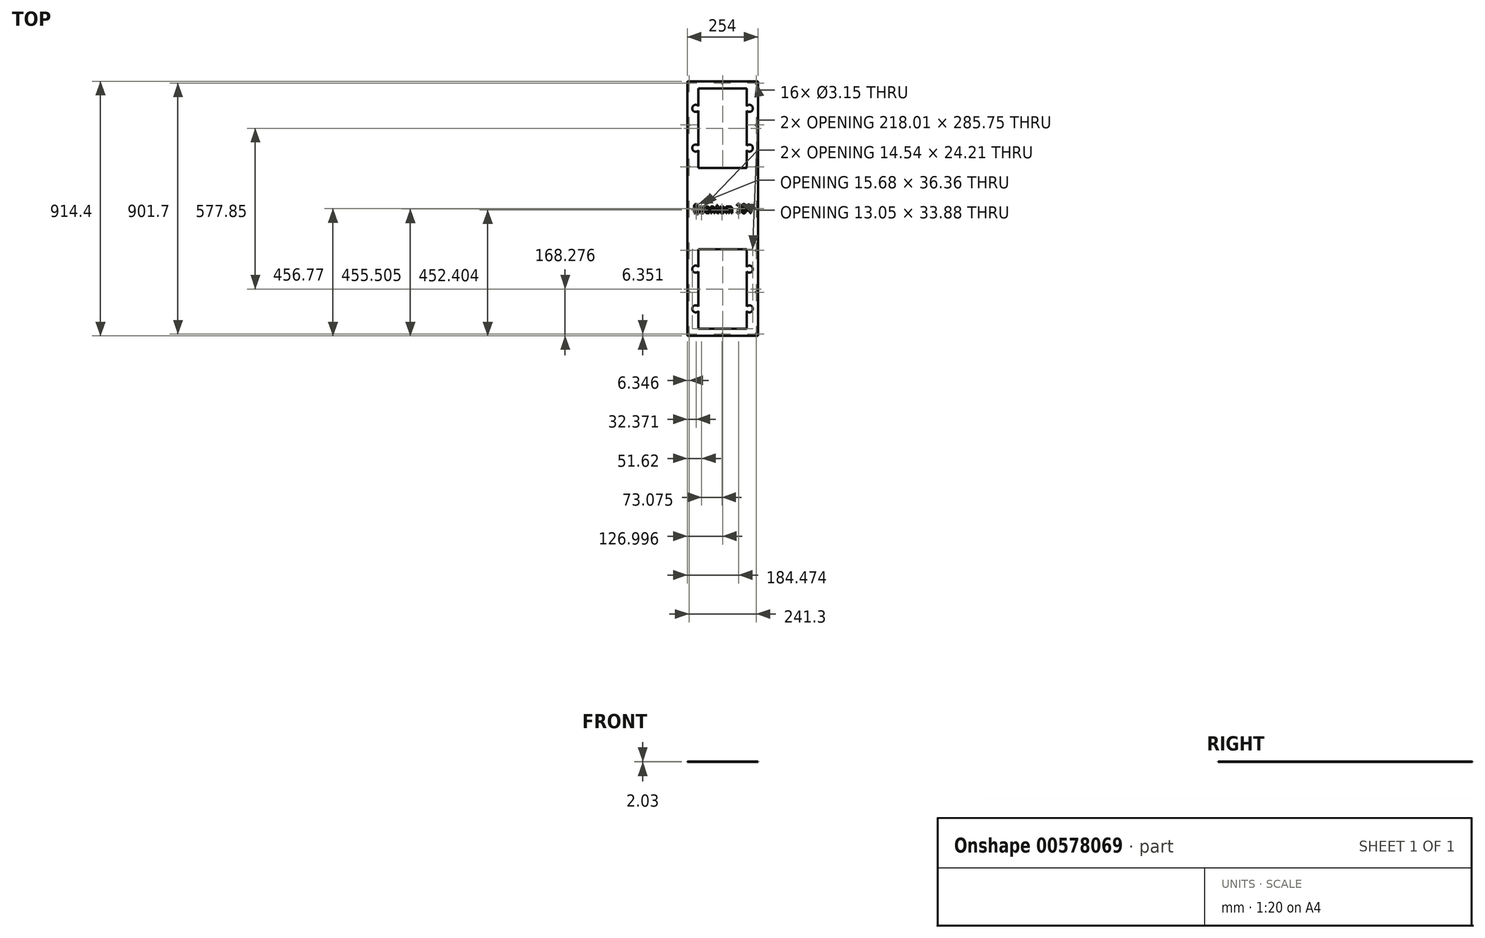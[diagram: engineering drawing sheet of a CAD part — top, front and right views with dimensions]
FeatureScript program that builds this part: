
annotation { "Feature Type Name" : "Feature", "Feature Type Description" : "" }
export const myFeature = defineFeature(function(context is Context, id is Id, definition is map)
    precondition{}
    {
        {
            var Q0;
            Q0=qCreatedBy(makeId("Top.planeOp"),FACE);
            var sketch = newSketch(context, id + "F0", { "sketchPlane" : qUnion([Q0])});
            skLineSegment(sketch, "E0.bottom", {"start": v(-485.77, 470.81) * mm, "end": v(-231.77, 470.81) * mm});
            skLineSegment(sketch, "E0.top", {"start": v(-485.77, -443.59) * mm, "end": v(-231.77, -443.59) * mm});
            skLineSegment(sketch, "E0.left", {"start": v(-485.77, 470.81) * mm, "end": v(-485.77, -443.59) * mm});
            skLineSegment(sketch, "E0.right", {"start": v(-231.77, 470.81) * mm, "end": v(-231.77, -443.59) * mm});
            skLineSegment(sketch, "E1.bottom", {"start": v(-445.55, 445.41) * mm, "end": v(-272, 445.41) * mm});
            skLineSegment(sketch, "E1.top", {"start": v(-445.55, 159.66) * mm, "end": v(-272, 159.66) * mm});
            skLineSegment(sketch, "E1.left", {"start": v(-445.55, 445.41) * mm, "end": v(-445.55, 382.37) * mm});
            skLineSegment(sketch, "E1.right", {"start": v(-272, 445.41) * mm, "end": v(-272, 382.37) * mm});
            skLineSegment(sketch, "E2.bottom", {"start": v(-445.55, -132.44) * mm, "end": v(-272, -132.44) * mm});
            skLineSegment(sketch, "E2.top", {"start": v(-445.55, -418.19) * mm, "end": v(-272, -418.19) * mm});
            skLineSegment(sketch, "E2.left", {"start": v(-445.55, -132.44) * mm, "end": v(-445.55, -195.48) * mm});
            skLineSegment(sketch, "E2.right", {"start": v(-272, -132.44) * mm, "end": v(-272, -195.48) * mm});
            skLineSegment(sketch, "E3", {"start": v(-358.77, 470.81) * mm, "end": v(-358.77, -443.59) * mm, "construction": true});
            skLineSegment(sketch, "E4.0", {"start": v(-479.42, 464.46) * mm, "end": v(-479.42, -437.24) * mm, "construction": true});
            skLineSegment(sketch, "E4.1", {"start": v(-479.42, 464.46) * mm, "end": v(-238.12, 464.46) * mm, "construction": true});
            skLineSegment(sketch, "E4.2", {"start": v(-238.12, 464.46) * mm, "end": v(-238.12, -437.24) * mm, "construction": true});
            skLineSegment(sketch, "E4.3", {"start": v(-479.42, -437.24) * mm, "end": v(-238.12, -437.24) * mm, "construction": true});
            skCircle(sketch, "E5", {"center": v(-479.42, 464.46) * mm, "radius": 1.57 * mm});
            skCircle(sketch, "E6", {"center": v(-479.42, -437.24) * mm, "radius": 1.57 * mm});
            skCircle(sketch, "E7", {"center": v(-238.12, -437.24) * mm, "radius": 1.57 * mm});
            skCircle(sketch, "E8", {"center": v(-238.12, 464.46) * mm, "radius": 1.57 * mm});
            skCircle(sketch, "E9", {"center": v(-358.77, 464.46) * mm, "radius": 1.57 * mm});
            skCircle(sketch, "E10", {"center": v(-358.77, -437.24) * mm, "radius": 1.57 * mm});
            skCircle(sketch, "E11", {"center": v(-479.42, 13.61) * mm, "radius": 1.57 * mm});
            skCircle(sketch, "E12", {"center": v(-238.12, 13.61) * mm, "radius": 1.57 * mm});
            skCircle(sketch, "E13", {"center": v(-479.42, 314.18) * mm, "radius": 1.57 * mm});
            skCircle(sketch, "E14", {"center": v(-479.42, 163.9) * mm, "radius": 1.57 * mm});
            skCircle(sketch, "E15", {"center": v(-238.12, 314.18) * mm, "radius": 1.57 * mm});
            skCircle(sketch, "E16", {"center": v(-238.12, 163.9) * mm, "radius": 1.57 * mm});
            skCircle(sketch, "E17.MirrorC", {"center": v(-479.42, -136.67) * mm, "radius": 1.57 * mm});
            skCircle(sketch, "E18.MirrorC", {"center": v(-238.12, -136.67) * mm, "radius": 1.57 * mm});
            skCircle(sketch, "E19.MirrorC", {"center": v(-238.12, -286.96) * mm, "radius": 1.57 * mm});
            skCircle(sketch, "E20.MirrorC", {"center": v(-479.42, -286.96) * mm, "radius": 1.57 * mm});
            skLineSegment(sketch, "E21.right", {"start": v(-485.77, 373.97) * mm, "end": v(-485.77, 373.97) * mm});
            skArc(sketch, "E22", {"start": v(-445.55, 382.37) * mm, "mid": v(-467.78, 373.97) * mm, "end": v(-445.55, 365.57) * mm});
            skArc(sketch, "E23", {"start": v(-272, 365.57) * mm, "mid": v(-249.77, 373.97) * mm, "end": v(-272, 382.37) * mm});
            skArc(sketch, "E24.MirrorC", {"start": v(-445.55, 222.7) * mm, "mid": v(-467.78, 231.1) * mm, "end": v(-445.55, 239.5) * mm});
            skArc(sketch, "E25.MirrorC", {"start": v(-272, 239.5) * mm, "mid": v(-249.77, 231.1) * mm, "end": v(-272, 222.7) * mm});
            skLineSegment(sketch, "E26.trimOffspring", {"start": v(-272, 365.57) * mm, "end": v(-272, 239.5) * mm});
            skLineSegment(sketch, "E27.trimOffspring", {"start": v(-445.55, 365.57) * mm, "end": v(-445.55, 239.5) * mm});
            skLineSegment(sketch, "E28.trimOffspring", {"start": v(-445.55, 222.7) * mm, "end": v(-445.55, 159.66) * mm});
            skLineSegment(sketch, "E29.trimOffspring", {"start": v(-272, 222.7) * mm, "end": v(-272, 159.66) * mm});
            skLineSegment(sketch, "E30", {"start": v(-485.77, 13.61) * mm, "end": v(-231.77, 13.61) * mm, "construction": true});
            skArc(sketch, "E31.MirrorCS", {"start": v(-445.55, -195.48) * mm, "mid": v(-467.78, -203.88) * mm, "end": v(-445.55, -212.28) * mm});
            skArc(sketch, "E32.MirrorCS", {"start": v(-445.55, -355.15) * mm, "mid": v(-467.78, -346.75) * mm, "end": v(-445.55, -338.35) * mm});
            skArc(sketch, "E33.MirrorCS", {"start": v(-272, -338.35) * mm, "mid": v(-249.77, -346.75) * mm, "end": v(-272, -355.15) * mm});
            skArc(sketch, "E34.MirrorCS", {"start": v(-272, -212.28) * mm, "mid": v(-249.77, -203.88) * mm, "end": v(-272, -195.48) * mm});
            skLineSegment(sketch, "E35.trimOffspring", {"start": v(-272, -212.28) * mm, "end": v(-272, -338.35) * mm});
            skLineSegment(sketch, "E36.trimOffspring", {"start": v(-272, -355.15) * mm, "end": v(-272, -418.19) * mm});
            skLineSegment(sketch, "E37.trimOffspring", {"start": v(-445.55, -355.15) * mm, "end": v(-445.55, -418.19) * mm});
            skLineSegment(sketch, "E38.trimOffspring", {"start": v(-445.55, -212.28) * mm, "end": v(-445.55, -338.35) * mm});
            skLineSegment(sketch, "E39", {"start": v(-461.21, 23.57) * mm, "end": v(-461.11, 24.3) * mm});
            skLineSegment(sketch, "E40", {"start": v(-461.11, 24.3) * mm, "end": v(-460.94, 24.96) * mm});
            skLineSegment(sketch, "E41", {"start": v(-460.94, 24.96) * mm, "end": v(-460.72, 25.63) * mm});
            skLineSegment(sketch, "E42", {"start": v(-460.72, 25.63) * mm, "end": v(-460.4, 26.25) * mm});
            skLineSegment(sketch, "E43", {"start": v(-460.4, 26.25) * mm, "end": v(-460.05, 26.85) * mm});
            skLineSegment(sketch, "E44", {"start": v(-460.05, 26.85) * mm, "end": v(-459.6, 27.42) * mm});
            skLineSegment(sketch, "E45", {"start": v(-459.6, 27.42) * mm, "end": v(-459.1, 27.96) * mm});
            skLineSegment(sketch, "E46", {"start": v(-459.1, 27.96) * mm, "end": v(-458.56, 28.46) * mm});
            skLineSegment(sketch, "E47", {"start": v(-458.56, 28.46) * mm, "end": v(-457.99, 28.9) * mm});
            skLineSegment(sketch, "E48", {"start": v(-457.99, 28.9) * mm, "end": v(-457.4, 29.25) * mm});
            skLineSegment(sketch, "E49", {"start": v(-457.4, 29.25) * mm, "end": v(-456.77, 29.58) * mm});
            skLineSegment(sketch, "E50", {"start": v(-456.77, 29.58) * mm, "end": v(-456.1, 29.8) * mm});
            skLineSegment(sketch, "E51", {"start": v(-456.1, 29.8) * mm, "end": v(-455.43, 29.97) * mm});
            skLineSegment(sketch, "E52", {"start": v(-455.43, 29.97) * mm, "end": v(-454.71, 30.07) * mm});
            skLineSegment(sketch, "E53", {"start": v(-454.71, 30.07) * mm, "end": v(-453.97, 30.1) * mm});
            skLineSegment(sketch, "E54", {"start": v(-453.97, 30.1) * mm, "end": v(-453.25, 30.07) * mm});
            skLineSegment(sketch, "E55", {"start": v(-453.25, 30.07) * mm, "end": v(-452.53, 29.97) * mm});
            skLineSegment(sketch, "E56", {"start": v(-452.53, 29.97) * mm, "end": v(-451.86, 29.8) * mm});
            skLineSegment(sketch, "E57", {"start": v(-451.86, 29.8) * mm, "end": v(-451.2, 29.58) * mm});
            skLineSegment(sketch, "E58", {"start": v(-451.2, 29.58) * mm, "end": v(-450.57, 29.25) * mm});
            skLineSegment(sketch, "E59", {"start": v(-450.57, 29.25) * mm, "end": v(-449.98, 28.9) * mm});
            skLineSegment(sketch, "E60", {"start": v(-449.98, 28.9) * mm, "end": v(-449.4, 28.46) * mm});
            skLineSegment(sketch, "E61", {"start": v(-449.4, 28.46) * mm, "end": v(-448.86, 27.96) * mm});
            skLineSegment(sketch, "E62", {"start": v(-448.86, 27.96) * mm, "end": v(-448.36, 27.42) * mm});
            skLineSegment(sketch, "E63", {"start": v(-448.36, 27.42) * mm, "end": v(-447.92, 26.85) * mm});
            skLineSegment(sketch, "E64", {"start": v(-447.92, 26.85) * mm, "end": v(-447.57, 26.25) * mm});
            skLineSegment(sketch, "E65", {"start": v(-447.57, 26.25) * mm, "end": v(-447.25, 25.63) * mm});
            skLineSegment(sketch, "E66", {"start": v(-447.25, 25.63) * mm, "end": v(-447.02, 24.96) * mm});
            skLineSegment(sketch, "E67", {"start": v(-447.02, 24.96) * mm, "end": v(-446.85, 24.3) * mm});
            skLineSegment(sketch, "E68", {"start": v(-446.85, 24.3) * mm, "end": v(-446.75, 23.57) * mm});
            skLineSegment(sketch, "E69", {"start": v(-446.75, 23.57) * mm, "end": v(-446.73, 22.85) * mm});
            skLineSegment(sketch, "E70", {"start": v(-446.73, 22.85) * mm, "end": v(-446.73, 3.5) * mm});
            skLineSegment(sketch, "E71", {"start": v(-446.73, 3.5) * mm, "end": v(-446.73, 3.28) * mm});
            skLineSegment(sketch, "E72", {"start": v(-446.73, 3.28) * mm, "end": v(-446.73, 3.06) * mm});
            skLineSegment(sketch, "E73", {"start": v(-446.73, 3.06) * mm, "end": v(-446.75, 2.84) * mm});
            skLineSegment(sketch, "E74", {"start": v(-446.75, 2.84) * mm, "end": v(-446.78, 2.61) * mm});
            skLineSegment(sketch, "E75", {"start": v(-446.78, 2.61) * mm, "end": v(-446.8, 2.41) * mm});
            skLineSegment(sketch, "E76", {"start": v(-446.8, 2.41) * mm, "end": v(-446.83, 2.2) * mm});
            skLineSegment(sketch, "E77", {"start": v(-446.83, 2.2) * mm, "end": v(-446.85, 2) * mm});
            skLineSegment(sketch, "E78", {"start": v(-446.85, 2) * mm, "end": v(-446.9, 1.77) * mm});
            skLineSegment(sketch, "E79", {"start": v(-446.9, 1.77) * mm, "end": v(-446.92, 1.65) * mm});
            skLineSegment(sketch, "E80", {"start": v(-446.92, 1.65) * mm, "end": v(-446.97, 1.5) * mm});
            skLineSegment(sketch, "E81", {"start": v(-446.97, 1.5) * mm, "end": v(-447.02, 1.37) * mm});
            skLineSegment(sketch, "E82", {"start": v(-447.02, 1.37) * mm, "end": v(-447.07, 1.25) * mm});
            skLineSegment(sketch, "E83", {"start": v(-447.07, 1.25) * mm, "end": v(-447.15, 1.15) * mm});
            skLineSegment(sketch, "E84", {"start": v(-447.15, 1.15) * mm, "end": v(-447.22, 1.03) * mm});
            skLineSegment(sketch, "E85", {"start": v(-447.22, 1.03) * mm, "end": v(-447.32, 0.93) * mm});
            skLineSegment(sketch, "E86", {"start": v(-447.32, 0.93) * mm, "end": v(-447.42, 0.8) * mm});
            skLineSegment(sketch, "E87", {"start": v(-447.42, 0.8) * mm, "end": v(-447.57, 0.68) * mm});
            skLineSegment(sketch, "E88", {"start": v(-447.57, 0.68) * mm, "end": v(-447.74, 0.55) * mm});
            skLineSegment(sketch, "E89", {"start": v(-447.74, 0.55) * mm, "end": v(-447.9, 0.46) * mm});
            skLineSegment(sketch, "E90", {"start": v(-447.9, 0.46) * mm, "end": v(-448.07, 0.38) * mm});
            skLineSegment(sketch, "E91", {"start": v(-448.07, 0.38) * mm, "end": v(-448.24, 0.3) * mm});
            skLineSegment(sketch, "E92", {"start": v(-448.24, 0.3) * mm, "end": v(-448.41, 0.26) * mm});
            skLineSegment(sketch, "E93", {"start": v(-448.41, 0.26) * mm, "end": v(-448.61, 0.23) * mm});
            skLineSegment(sketch, "E94", {"start": v(-448.61, 0.23) * mm, "end": v(-448.8, 0.23) * mm});
            skLineSegment(sketch, "E95", {"start": v(-448.8, 0.23) * mm, "end": v(-449, 0.23) * mm});
            skLineSegment(sketch, "E96", {"start": v(-449, 0.23) * mm, "end": v(-449.18, 0.26) * mm});
            skLineSegment(sketch, "E97", {"start": v(-449.18, 0.26) * mm, "end": v(-449.38, 0.3) * mm});
            skLineSegment(sketch, "E98", {"start": v(-449.38, 0.3) * mm, "end": v(-449.55, 0.38) * mm});
            skLineSegment(sketch, "E99", {"start": v(-449.55, 0.38) * mm, "end": v(-449.7, 0.46) * mm});
            skLineSegment(sketch, "E100", {"start": v(-449.7, 0.46) * mm, "end": v(-449.88, 0.55) * mm});
            skLineSegment(sketch, "E101", {"start": v(-449.88, 0.55) * mm, "end": v(-450.03, 0.65) * mm});
            skLineSegment(sketch, "E102", {"start": v(-450.03, 0.65) * mm, "end": v(-450.17, 0.8) * mm});
            skLineSegment(sketch, "E103", {"start": v(-450.17, 0.8) * mm, "end": v(-450.3, 0.95) * mm});
            skLineSegment(sketch, "E104", {"start": v(-450.3, 0.95) * mm, "end": v(-450.42, 1.1) * mm});
            skLineSegment(sketch, "E105", {"start": v(-450.42, 1.1) * mm, "end": v(-450.52, 1.25) * mm});
            skLineSegment(sketch, "E106", {"start": v(-450.52, 1.25) * mm, "end": v(-450.6, 1.42) * mm});
            skLineSegment(sketch, "E107", {"start": v(-450.6, 1.42) * mm, "end": v(-450.67, 1.6) * mm});
            skLineSegment(sketch, "E108", {"start": v(-450.67, 1.6) * mm, "end": v(-450.7, 1.77) * mm});
            skLineSegment(sketch, "E109", {"start": v(-450.7, 1.77) * mm, "end": v(-450.72, 1.97) * mm});
            skLineSegment(sketch, "E110", {"start": v(-450.72, 1.97) * mm, "end": v(-450.74, 2.17) * mm});
            skLineSegment(sketch, "E111", {"start": v(-450.74, 2.17) * mm, "end": v(-450.74, 2.22) * mm});
            skLineSegment(sketch, "E112", {"start": v(-450.74, 2.22) * mm, "end": v(-450.74, 2.27) * mm});
            skLineSegment(sketch, "E113", {"start": v(-450.74, 2.27) * mm, "end": v(-450.74, 2.32) * mm});
            skLineSegment(sketch, "E114", {"start": v(-450.74, 2.32) * mm, "end": v(-450.74, 2.36) * mm});
            skLineSegment(sketch, "E115", {"start": v(-450.74, 2.36) * mm, "end": v(-450.72, 2.41) * mm});
            skLineSegment(sketch, "E116", {"start": v(-450.72, 2.41) * mm, "end": v(-450.72, 2.49) * mm});
            skLineSegment(sketch, "E117", {"start": v(-450.72, 2.49) * mm, "end": v(-450.72, 2.54) * mm});
            skLineSegment(sketch, "E118", {"start": v(-450.72, 2.54) * mm, "end": v(-450.72, 2.59) * mm});
            skLineSegment(sketch, "E119", {"start": v(-450.72, 2.59) * mm, "end": v(-450.7, 2.71) * mm});
            skLineSegment(sketch, "E120", {"start": v(-450.7, 2.71) * mm, "end": v(-450.67, 2.81) * mm});
            skLineSegment(sketch, "E121", {"start": v(-450.67, 2.81) * mm, "end": v(-450.65, 2.94) * mm});
            skLineSegment(sketch, "E122", {"start": v(-450.65, 2.94) * mm, "end": v(-450.62, 3.03) * mm});
            skLineSegment(sketch, "E123", {"start": v(-450.62, 3.03) * mm, "end": v(-450.62, 3.16) * mm});
            skLineSegment(sketch, "E124", {"start": v(-450.62, 3.16) * mm, "end": v(-450.6, 3.26) * mm});
            skLineSegment(sketch, "E125", {"start": v(-450.6, 3.26) * mm, "end": v(-450.6, 3.38) * mm});
            skLineSegment(sketch, "E126", {"start": v(-450.6, 3.38) * mm, "end": v(-450.6, 3.5) * mm});
            skLineSegment(sketch, "E127", {"start": v(-450.6, 3.5) * mm, "end": v(-450.6, 22.85) * mm});
            skLineSegment(sketch, "E128", {"start": v(-450.6, 22.85) * mm, "end": v(-450.62, 23.18) * mm});
            skLineSegment(sketch, "E129", {"start": v(-450.62, 23.18) * mm, "end": v(-450.65, 23.52) * mm});
            skLineSegment(sketch, "E130", {"start": v(-450.65, 23.52) * mm, "end": v(-450.74, 23.85) * mm});
            skLineSegment(sketch, "E131", {"start": v(-450.74, 23.85) * mm, "end": v(-450.84, 24.14) * mm});
            skLineSegment(sketch, "E132", {"start": v(-450.84, 24.14) * mm, "end": v(-451, 24.44) * mm});
            skLineSegment(sketch, "E133", {"start": v(-451, 24.44) * mm, "end": v(-451.14, 24.71) * mm});
            skLineSegment(sketch, "E134", {"start": v(-451.14, 24.71) * mm, "end": v(-451.36, 24.99) * mm});
            skLineSegment(sketch, "E135", {"start": v(-451.36, 24.99) * mm, "end": v(-451.59, 25.23) * mm});
            skLineSegment(sketch, "E136", {"start": v(-451.59, 25.23) * mm, "end": v(-451.84, 25.46) * mm});
            skLineSegment(sketch, "E137", {"start": v(-451.84, 25.46) * mm, "end": v(-452.1, 25.68) * mm});
            skLineSegment(sketch, "E138", {"start": v(-452.1, 25.68) * mm, "end": v(-452.38, 25.83) * mm});
            skLineSegment(sketch, "E139", {"start": v(-452.38, 25.83) * mm, "end": v(-452.68, 25.98) * mm});
            skLineSegment(sketch, "E140", {"start": v(-452.68, 25.98) * mm, "end": v(-452.98, 26.08) * mm});
            skLineSegment(sketch, "E141", {"start": v(-452.98, 26.08) * mm, "end": v(-453.3, 26.18) * mm});
            skLineSegment(sketch, "E142", {"start": v(-453.3, 26.18) * mm, "end": v(-453.65, 26.2) * mm});
            skLineSegment(sketch, "E143", {"start": v(-453.65, 26.2) * mm, "end": v(-453.97, 26.23) * mm});
            skLineSegment(sketch, "E144", {"start": v(-453.97, 26.23) * mm, "end": v(-454.32, 26.2) * mm});
            skLineSegment(sketch, "E145", {"start": v(-454.32, 26.2) * mm, "end": v(-454.66, 26.18) * mm});
            skLineSegment(sketch, "E146", {"start": v(-454.66, 26.18) * mm, "end": v(-454.99, 26.08) * mm});
            skLineSegment(sketch, "E147", {"start": v(-454.99, 26.08) * mm, "end": v(-455.28, 25.98) * mm});
            skLineSegment(sketch, "E148", {"start": v(-455.28, 25.98) * mm, "end": v(-455.58, 25.83) * mm});
            skLineSegment(sketch, "E149", {"start": v(-455.58, 25.83) * mm, "end": v(-455.85, 25.68) * mm});
            skLineSegment(sketch, "E150", {"start": v(-455.85, 25.68) * mm, "end": v(-456.13, 25.46) * mm});
            skLineSegment(sketch, "E151", {"start": v(-456.13, 25.46) * mm, "end": v(-456.38, 25.23) * mm});
            skLineSegment(sketch, "E152", {"start": v(-456.38, 25.23) * mm, "end": v(-456.6, 24.99) * mm});
            skLineSegment(sketch, "E153", {"start": v(-456.6, 24.99) * mm, "end": v(-456.82, 24.71) * mm});
            skLineSegment(sketch, "E154", {"start": v(-456.82, 24.71) * mm, "end": v(-456.97, 24.44) * mm});
            skLineSegment(sketch, "E155", {"start": v(-456.97, 24.44) * mm, "end": v(-457.12, 24.14) * mm});
            skLineSegment(sketch, "E156", {"start": v(-457.12, 24.14) * mm, "end": v(-457.22, 23.85) * mm});
            skLineSegment(sketch, "E157", {"start": v(-457.22, 23.85) * mm, "end": v(-457.32, 23.52) * mm});
            skLineSegment(sketch, "E158", {"start": v(-457.32, 23.52) * mm, "end": v(-457.34, 23.18) * mm});
            skLineSegment(sketch, "E159", {"start": v(-457.34, 23.18) * mm, "end": v(-457.37, 22.85) * mm});
            skLineSegment(sketch, "E160", {"start": v(-457.37, 22.85) * mm, "end": v(-457.37, 3.5) * mm});
            skLineSegment(sketch, "E161", {"start": v(-457.37, 3.5) * mm, "end": v(-457.34, 3.16) * mm});
            skLineSegment(sketch, "E162", {"start": v(-457.34, 3.16) * mm, "end": v(-457.32, 2.84) * mm});
            skLineSegment(sketch, "E163", {"start": v(-457.32, 2.84) * mm, "end": v(-457.24, 2.54) * mm});
            skLineSegment(sketch, "E164", {"start": v(-457.24, 2.54) * mm, "end": v(-457.14, 2.24) * mm});
            skLineSegment(sketch, "E165", {"start": v(-457.14, 2.24) * mm, "end": v(-457, 1.97) * mm});
            skLineSegment(sketch, "E166", {"start": v(-457, 1.97) * mm, "end": v(-456.85, 1.72) * mm});
            skLineSegment(sketch, "E167", {"start": v(-456.85, 1.72) * mm, "end": v(-456.65, 1.47) * mm});
            skLineSegment(sketch, "E168", {"start": v(-456.65, 1.47) * mm, "end": v(-456.43, 1.25) * mm});
            skLineSegment(sketch, "E169", {"start": v(-456.43, 1.25) * mm, "end": v(-456.2, 1.05) * mm});
            skLineSegment(sketch, "E170", {"start": v(-456.2, 1.05) * mm, "end": v(-455.95, 0.85) * mm});
            skLineSegment(sketch, "E171", {"start": v(-455.95, 0.85) * mm, "end": v(-455.7, 0.68) * mm});
            skLineSegment(sketch, "E172", {"start": v(-455.7, 0.68) * mm, "end": v(-455.43, 0.53) * mm});
            skLineSegment(sketch, "E173", {"start": v(-455.43, 0.53) * mm, "end": v(-455.18, 0.4) * mm});
            skLineSegment(sketch, "E174", {"start": v(-455.18, 0.4) * mm, "end": v(-454.89, 0.28) * mm});
            skLineSegment(sketch, "E175", {"start": v(-454.89, 0.28) * mm, "end": v(-454.61, 0.18) * mm});
            skLineSegment(sketch, "E176", {"start": v(-454.61, 0.18) * mm, "end": v(-454.32, 0.08) * mm});
            skLineSegment(sketch, "E177", {"start": v(-454.32, 0.08) * mm, "end": v(-446.9, -2.5) * mm});
            skLineSegment(sketch, "E178", {"start": v(-446.9, -2.5) * mm, "end": v(-446.7, -2.57) * mm});
            skLineSegment(sketch, "E179", {"start": v(-446.7, -2.57) * mm, "end": v(-446.53, -2.67) * mm});
            skLineSegment(sketch, "E180", {"start": v(-446.53, -2.67) * mm, "end": v(-446.38, -2.77) * mm});
            skLineSegment(sketch, "E181", {"start": v(-446.38, -2.77) * mm, "end": v(-446.23, -2.9) * mm});
            skLineSegment(sketch, "E182", {"start": v(-446.23, -2.9) * mm, "end": v(-446.08, -3.02) * mm});
            skLineSegment(sketch, "E183", {"start": v(-446.08, -3.02) * mm, "end": v(-445.96, -3.17) * mm});
            skLineSegment(sketch, "E184", {"start": v(-445.96, -3.17) * mm, "end": v(-445.86, -3.32) * mm});
            skLineSegment(sketch, "E185", {"start": v(-445.86, -3.32) * mm, "end": v(-445.76, -3.49) * mm});
            skLineSegment(sketch, "E186", {"start": v(-445.76, -3.49) * mm, "end": v(-445.7, -3.61) * mm});
            skLineSegment(sketch, "E187", {"start": v(-445.7, -3.61) * mm, "end": v(-445.68, -3.71) * mm});
            skLineSegment(sketch, "E188", {"start": v(-445.68, -3.71) * mm, "end": v(-445.63, -3.81) * mm});
            skLineSegment(sketch, "E189", {"start": v(-445.63, -3.81) * mm, "end": v(-445.61, -3.94) * mm});
            skLineSegment(sketch, "E190", {"start": v(-445.61, -3.94) * mm, "end": v(-445.59, -4.03) * mm});
            skLineSegment(sketch, "E191", {"start": v(-445.59, -4.03) * mm, "end": v(-445.59, -4.13) * mm});
            skLineSegment(sketch, "E192", {"start": v(-445.59, -4.13) * mm, "end": v(-445.56, -4.23) * mm});
            skLineSegment(sketch, "E193", {"start": v(-445.56, -4.23) * mm, "end": v(-445.56, -4.33) * mm});
            skLineSegment(sketch, "E194", {"start": v(-445.56, -4.33) * mm, "end": v(-445.56, -4.4) * mm});
            skLineSegment(sketch, "E195", {"start": v(-445.56, -4.4) * mm, "end": v(-445.56, -4.48) * mm});
            skLineSegment(sketch, "E196", {"start": v(-445.56, -4.48) * mm, "end": v(-445.59, -4.56) * mm});
            skLineSegment(sketch, "E197", {"start": v(-445.59, -4.56) * mm, "end": v(-445.59, -4.63) * mm});
            skLineSegment(sketch, "E198", {"start": v(-445.59, -4.63) * mm, "end": v(-445.61, -4.7) * mm});
            skLineSegment(sketch, "E199", {"start": v(-445.61, -4.7) * mm, "end": v(-445.61, -4.78) * mm});
            skLineSegment(sketch, "E200", {"start": v(-445.61, -4.78) * mm, "end": v(-445.63, -4.88) * mm});
            skLineSegment(sketch, "E201", {"start": v(-445.63, -4.88) * mm, "end": v(-445.66, -4.95) * mm});
            skLineSegment(sketch, "E202", {"start": v(-445.66, -4.95) * mm, "end": v(-445.73, -5.13) * mm});
            skLineSegment(sketch, "E203", {"start": v(-445.73, -5.13) * mm, "end": v(-445.83, -5.3) * mm});
            skLineSegment(sketch, "E204", {"start": v(-445.83, -5.3) * mm, "end": v(-445.93, -5.47) * mm});
            skLineSegment(sketch, "E205", {"start": v(-445.93, -5.47) * mm, "end": v(-446.03, -5.62) * mm});
            skLineSegment(sketch, "E206", {"start": v(-446.03, -5.62) * mm, "end": v(-446.18, -5.75) * mm});
            skLineSegment(sketch, "E207", {"start": v(-446.18, -5.75) * mm, "end": v(-446.33, -5.87) * mm});
            skLineSegment(sketch, "E208", {"start": v(-446.33, -5.87) * mm, "end": v(-446.48, -6) * mm});
            skLineSegment(sketch, "E209", {"start": v(-446.48, -6) * mm, "end": v(-446.65, -6.1) * mm});
            skLineSegment(sketch, "E210", {"start": v(-446.65, -6.1) * mm, "end": v(-446.75, -6.12) * mm});
            skLineSegment(sketch, "E211", {"start": v(-446.75, -6.12) * mm, "end": v(-446.88, -6.17) * mm});
            skLineSegment(sketch, "E212", {"start": v(-446.88, -6.17) * mm, "end": v(-446.97, -6.2) * mm});
            skLineSegment(sketch, "E213", {"start": v(-446.97, -6.2) * mm, "end": v(-447.07, -6.22) * mm});
            skLineSegment(sketch, "E214", {"start": v(-447.07, -6.22) * mm, "end": v(-447.2, -6.24) * mm});
            skLineSegment(sketch, "E215", {"start": v(-447.2, -6.24) * mm, "end": v(-447.3, -6.27) * mm});
            skLineSegment(sketch, "E216", {"start": v(-447.3, -6.27) * mm, "end": v(-447.4, -6.27) * mm});
            skLineSegment(sketch, "E217", {"start": v(-447.4, -6.27) * mm, "end": v(-447.5, -6.27) * mm});
            skLineSegment(sketch, "E218", {"start": v(-447.5, -6.27) * mm, "end": v(-447.57, -6.27) * mm});
            skLineSegment(sketch, "E219", {"start": v(-447.57, -6.27) * mm, "end": v(-447.67, -6.27) * mm});
            skLineSegment(sketch, "E220", {"start": v(-447.67, -6.27) * mm, "end": v(-447.74, -6.27) * mm});
            skLineSegment(sketch, "E221", {"start": v(-447.74, -6.27) * mm, "end": v(-447.82, -6.24) * mm});
            skLineSegment(sketch, "E222", {"start": v(-447.82, -6.24) * mm, "end": v(-447.9, -6.24) * mm});
            skLineSegment(sketch, "E223", {"start": v(-447.9, -6.24) * mm, "end": v(-447.97, -6.22) * mm});
            skLineSegment(sketch, "E224", {"start": v(-447.97, -6.22) * mm, "end": v(-448.04, -6.2) * mm});
            skLineSegment(sketch, "E225", {"start": v(-448.04, -6.2) * mm, "end": v(-448.14, -6.17) * mm});
            skLineSegment(sketch, "E226", {"start": v(-448.14, -6.17) * mm, "end": v(-455.9, -3.51) * mm});
            skLineSegment(sketch, "E227", {"start": v(-455.9, -3.51) * mm, "end": v(-456.4, -3.34) * mm});
            skLineSegment(sketch, "E228", {"start": v(-456.4, -3.34) * mm, "end": v(-456.85, -3.14) * mm});
            skLineSegment(sketch, "E229", {"start": v(-456.85, -3.14) * mm, "end": v(-457.3, -2.92) * mm});
            skLineSegment(sketch, "E230", {"start": v(-457.3, -2.92) * mm, "end": v(-457.7, -2.7) * mm});
            skLineSegment(sketch, "E231", {"start": v(-457.7, -2.7) * mm, "end": v(-458.09, -2.45) * mm});
            skLineSegment(sketch, "E232", {"start": v(-458.09, -2.45) * mm, "end": v(-458.46, -2.2) * mm});
            skLineSegment(sketch, "E233", {"start": v(-458.46, -2.2) * mm, "end": v(-458.78, -1.93) * mm});
            skLineSegment(sketch, "E234", {"start": v(-458.78, -1.93) * mm, "end": v(-459.1, -1.63) * mm});
            skLineSegment(sketch, "E235", {"start": v(-459.1, -1.63) * mm, "end": v(-459.6, -1.08) * mm});
            skLineSegment(sketch, "E236", {"start": v(-459.6, -1.08) * mm, "end": v(-460.05, -0.51) * mm});
            skLineSegment(sketch, "E237", {"start": v(-460.05, -0.51) * mm, "end": v(-460.4, 0.08) * mm});
            skLineSegment(sketch, "E238", {"start": v(-460.4, 0.08) * mm, "end": v(-460.72, 0.7) * mm});
            skLineSegment(sketch, "E239", {"start": v(-460.72, 0.7) * mm, "end": v(-460.94, 1.37) * mm});
            skLineSegment(sketch, "E240", {"start": v(-460.94, 1.37) * mm, "end": v(-461.11, 2.04) * mm});
            skLineSegment(sketch, "E241", {"start": v(-461.11, 2.04) * mm, "end": v(-461.21, 2.76) * mm});
            skLineSegment(sketch, "E242", {"start": v(-461.21, 2.76) * mm, "end": v(-461.24, 3.5) * mm});
            skLineSegment(sketch, "E243", {"start": v(-461.24, 3.5) * mm, "end": v(-461.24, 22.85) * mm});
            skLineSegment(sketch, "E244", {"start": v(-461.24, 22.85) * mm, "end": v(-461.21, 23.57) * mm});
            skLineSegment(sketch, "E245", {"start": v(-441.37, 3.23) * mm, "end": v(-441.42, 3.98) * mm});
            skLineSegment(sketch, "E246", {"start": v(-441.42, 3.98) * mm, "end": v(-441.42, 18.98) * mm});
            skLineSegment(sketch, "E247", {"start": v(-441.42, 18.98) * mm, "end": v(-441.4, 19.16) * mm});
            skLineSegment(sketch, "E248", {"start": v(-441.4, 19.16) * mm, "end": v(-441.37, 19.36) * mm});
            skLineSegment(sketch, "E249", {"start": v(-441.37, 19.36) * mm, "end": v(-441.32, 19.53) * mm});
            skLineSegment(sketch, "E250", {"start": v(-441.32, 19.53) * mm, "end": v(-441.27, 19.7) * mm});
            skLineSegment(sketch, "E251", {"start": v(-441.27, 19.7) * mm, "end": v(-441.2, 19.88) * mm});
            skLineSegment(sketch, "E252", {"start": v(-441.2, 19.88) * mm, "end": v(-441.1, 20.05) * mm});
            skLineSegment(sketch, "E253", {"start": v(-441.1, 20.05) * mm, "end": v(-440.97, 20.2) * mm});
            skLineSegment(sketch, "E254", {"start": v(-440.97, 20.2) * mm, "end": v(-440.85, 20.35) * mm});
            skLineSegment(sketch, "E255", {"start": v(-440.85, 20.35) * mm, "end": v(-440.7, 20.47) * mm});
            skLineSegment(sketch, "E256", {"start": v(-440.7, 20.47) * mm, "end": v(-440.55, 20.6) * mm});
            skLineSegment(sketch, "E257", {"start": v(-440.55, 20.6) * mm, "end": v(-440.38, 20.7) * mm});
            skLineSegment(sketch, "E258", {"start": v(-440.38, 20.7) * mm, "end": v(-440.2, 20.77) * mm});
            skLineSegment(sketch, "E259", {"start": v(-440.2, 20.77) * mm, "end": v(-440.03, 20.82) * mm});
            skLineSegment(sketch, "E260", {"start": v(-440.03, 20.82) * mm, "end": v(-439.86, 20.87) * mm});
            skLineSegment(sketch, "E261", {"start": v(-439.86, 20.87) * mm, "end": v(-439.66, 20.9) * mm});
            skLineSegment(sketch, "E262", {"start": v(-439.66, 20.9) * mm, "end": v(-439.48, 20.92) * mm});
            skLineSegment(sketch, "E263", {"start": v(-439.48, 20.92) * mm, "end": v(-439.28, 20.9) * mm});
            skLineSegment(sketch, "E264", {"start": v(-439.28, 20.9) * mm, "end": v(-439.09, 20.87) * mm});
            skLineSegment(sketch, "E265", {"start": v(-439.09, 20.87) * mm, "end": v(-438.91, 20.82) * mm});
            skLineSegment(sketch, "E266", {"start": v(-438.91, 20.82) * mm, "end": v(-438.74, 20.77) * mm});
            skLineSegment(sketch, "E267", {"start": v(-438.74, 20.77) * mm, "end": v(-438.57, 20.7) * mm});
            skLineSegment(sketch, "E268", {"start": v(-438.57, 20.7) * mm, "end": v(-438.4, 20.6) * mm});
            skLineSegment(sketch, "E269", {"start": v(-438.4, 20.6) * mm, "end": v(-438.24, 20.47) * mm});
            skLineSegment(sketch, "E270", {"start": v(-438.24, 20.47) * mm, "end": v(-438.1, 20.35) * mm});
            skLineSegment(sketch, "E271", {"start": v(-438.1, 20.35) * mm, "end": v(-437.97, 20.2) * mm});
            skLineSegment(sketch, "E272", {"start": v(-437.97, 20.2) * mm, "end": v(-437.85, 20.05) * mm});
            skLineSegment(sketch, "E273", {"start": v(-437.85, 20.05) * mm, "end": v(-437.75, 19.88) * mm});
            skLineSegment(sketch, "E274", {"start": v(-437.75, 19.88) * mm, "end": v(-437.67, 19.7) * mm});
            skLineSegment(sketch, "E275", {"start": v(-437.67, 19.7) * mm, "end": v(-437.62, 19.53) * mm});
            skLineSegment(sketch, "E276", {"start": v(-437.62, 19.53) * mm, "end": v(-437.57, 19.36) * mm});
            skLineSegment(sketch, "E277", {"start": v(-437.57, 19.36) * mm, "end": v(-437.55, 19.16) * mm});
            skLineSegment(sketch, "E278", {"start": v(-437.55, 19.16) * mm, "end": v(-437.55, 18.98) * mm});
            skLineSegment(sketch, "E279", {"start": v(-437.55, 18.98) * mm, "end": v(-437.55, 3.98) * mm});
            skLineSegment(sketch, "E280", {"start": v(-437.55, 3.98) * mm, "end": v(-437.52, 3.63) * mm});
            skLineSegment(sketch, "E281", {"start": v(-437.52, 3.63) * mm, "end": v(-437.47, 3.3) * mm});
            skLineSegment(sketch, "E282", {"start": v(-437.47, 3.3) * mm, "end": v(-437.4, 2.99) * mm});
            skLineSegment(sketch, "E283", {"start": v(-437.4, 2.99) * mm, "end": v(-437.3, 2.69) * mm});
            skLineSegment(sketch, "E284", {"start": v(-437.3, 2.69) * mm, "end": v(-437.15, 2.39) * mm});
            skLineSegment(sketch, "E285", {"start": v(-437.15, 2.39) * mm, "end": v(-436.98, 2.12) * mm});
            skLineSegment(sketch, "E286", {"start": v(-436.98, 2.12) * mm, "end": v(-436.78, 1.84) * mm});
            skLineSegment(sketch, "E287", {"start": v(-436.78, 1.84) * mm, "end": v(-436.56, 1.57) * mm});
            skLineSegment(sketch, "E288", {"start": v(-436.56, 1.57) * mm, "end": v(-436.28, 1.35) * mm});
            skLineSegment(sketch, "E289", {"start": v(-436.28, 1.35) * mm, "end": v(-436.01, 1.15) * mm});
            skLineSegment(sketch, "E290", {"start": v(-436.01, 1.15) * mm, "end": v(-435.74, 0.98) * mm});
            skLineSegment(sketch, "E291", {"start": v(-435.74, 0.98) * mm, "end": v(-435.44, 0.83) * mm});
            skLineSegment(sketch, "E292", {"start": v(-435.44, 0.83) * mm, "end": v(-435.14, 0.73) * mm});
            skLineSegment(sketch, "E293", {"start": v(-435.14, 0.73) * mm, "end": v(-434.82, 0.65) * mm});
            skLineSegment(sketch, "E294", {"start": v(-434.82, 0.65) * mm, "end": v(-434.5, 0.6) * mm});
            skLineSegment(sketch, "E295", {"start": v(-434.5, 0.6) * mm, "end": v(-434.15, 0.58) * mm});
            skLineSegment(sketch, "E296", {"start": v(-434.15, 0.58) * mm, "end": v(-430.75, 0.58) * mm});
            skLineSegment(sketch, "E297", {"start": v(-430.75, 0.58) * mm, "end": v(-430.75, 18.98) * mm});
            skLineSegment(sketch, "E298", {"start": v(-430.75, 18.98) * mm, "end": v(-430.75, 19.16) * mm});
            skLineSegment(sketch, "E299", {"start": v(-430.75, 19.16) * mm, "end": v(-430.73, 19.36) * mm});
            skLineSegment(sketch, "E300", {"start": v(-430.73, 19.36) * mm, "end": v(-430.68, 19.53) * mm});
            skLineSegment(sketch, "E301", {"start": v(-430.68, 19.53) * mm, "end": v(-430.63, 19.7) * mm});
            skLineSegment(sketch, "E302", {"start": v(-430.63, 19.7) * mm, "end": v(-430.55, 19.88) * mm});
            skLineSegment(sketch, "E303", {"start": v(-430.55, 19.88) * mm, "end": v(-430.45, 20.05) * mm});
            skLineSegment(sketch, "E304", {"start": v(-430.45, 20.05) * mm, "end": v(-430.33, 20.2) * mm});
            skLineSegment(sketch, "E305", {"start": v(-430.33, 20.2) * mm, "end": v(-430.2, 20.35) * mm});
            skLineSegment(sketch, "E306", {"start": v(-430.2, 20.35) * mm, "end": v(-430.06, 20.47) * mm});
            skLineSegment(sketch, "E307", {"start": v(-430.06, 20.47) * mm, "end": v(-429.9, 20.6) * mm});
            skLineSegment(sketch, "E308", {"start": v(-429.9, 20.6) * mm, "end": v(-429.74, 20.7) * mm});
            skLineSegment(sketch, "E309", {"start": v(-429.74, 20.7) * mm, "end": v(-429.56, 20.77) * mm});
            skLineSegment(sketch, "E310", {"start": v(-429.56, 20.77) * mm, "end": v(-429.39, 20.82) * mm});
            skLineSegment(sketch, "E311", {"start": v(-429.39, 20.82) * mm, "end": v(-429.21, 20.87) * mm});
            skLineSegment(sketch, "E312", {"start": v(-429.21, 20.87) * mm, "end": v(-429.02, 20.9) * mm});
            skLineSegment(sketch, "E313", {"start": v(-429.02, 20.9) * mm, "end": v(-428.82, 20.92) * mm});
            skLineSegment(sketch, "E314", {"start": v(-428.82, 20.92) * mm, "end": v(-428.64, 20.9) * mm});
            skLineSegment(sketch, "E315", {"start": v(-428.64, 20.9) * mm, "end": v(-428.45, 20.87) * mm});
            skLineSegment(sketch, "E316", {"start": v(-428.45, 20.87) * mm, "end": v(-428.27, 20.82) * mm});
            skLineSegment(sketch, "E317", {"start": v(-428.27, 20.82) * mm, "end": v(-428.1, 20.77) * mm});
            skLineSegment(sketch, "E318", {"start": v(-428.1, 20.77) * mm, "end": v(-427.92, 20.7) * mm});
            skLineSegment(sketch, "E319", {"start": v(-427.92, 20.7) * mm, "end": v(-427.75, 20.6) * mm});
            skLineSegment(sketch, "E320", {"start": v(-427.75, 20.6) * mm, "end": v(-427.6, 20.47) * mm});
            skLineSegment(sketch, "E321", {"start": v(-427.6, 20.47) * mm, "end": v(-427.45, 20.35) * mm});
            skLineSegment(sketch, "E322", {"start": v(-427.45, 20.35) * mm, "end": v(-427.33, 20.2) * mm});
            skLineSegment(sketch, "E323", {"start": v(-427.33, 20.2) * mm, "end": v(-427.2, 20.05) * mm});
            skLineSegment(sketch, "E324", {"start": v(-427.2, 20.05) * mm, "end": v(-427.1, 19.88) * mm});
            skLineSegment(sketch, "E325", {"start": v(-427.1, 19.88) * mm, "end": v(-427.03, 19.7) * mm});
            skLineSegment(sketch, "E326", {"start": v(-427.03, 19.7) * mm, "end": v(-426.98, 19.53) * mm});
            skLineSegment(sketch, "E327", {"start": v(-426.98, 19.53) * mm, "end": v(-426.93, 19.36) * mm});
            skLineSegment(sketch, "E328", {"start": v(-426.93, 19.36) * mm, "end": v(-426.9, 19.16) * mm});
            skLineSegment(sketch, "E329", {"start": v(-426.9, 19.16) * mm, "end": v(-426.88, 18.98) * mm});
            skLineSegment(sketch, "E330", {"start": v(-426.88, 18.98) * mm, "end": v(-426.88, -1.36) * mm});
            skLineSegment(sketch, "E331", {"start": v(-426.88, -1.36) * mm, "end": v(-426.9, -1.53) * mm});
            skLineSegment(sketch, "E332", {"start": v(-426.9, -1.53) * mm, "end": v(-426.93, -1.73) * mm});
            skLineSegment(sketch, "E333", {"start": v(-426.93, -1.73) * mm, "end": v(-426.98, -1.9) * mm});
            skLineSegment(sketch, "E334", {"start": v(-426.98, -1.9) * mm, "end": v(-427.03, -2.08) * mm});
            skLineSegment(sketch, "E335", {"start": v(-427.03, -2.08) * mm, "end": v(-427.1, -2.25) * mm});
            skLineSegment(sketch, "E336", {"start": v(-427.1, -2.25) * mm, "end": v(-427.2, -2.42) * mm});
            skLineSegment(sketch, "E337", {"start": v(-427.2, -2.42) * mm, "end": v(-427.33, -2.57) * mm});
            skLineSegment(sketch, "E338", {"start": v(-427.33, -2.57) * mm, "end": v(-427.45, -2.72) * mm});
            skLineSegment(sketch, "E339", {"start": v(-427.45, -2.72) * mm, "end": v(-427.6, -2.84) * mm});
            skLineSegment(sketch, "E340", {"start": v(-427.6, -2.84) * mm, "end": v(-427.75, -2.97) * mm});
            skLineSegment(sketch, "E341", {"start": v(-427.75, -2.97) * mm, "end": v(-427.92, -3.07) * mm});
            skLineSegment(sketch, "E342", {"start": v(-427.92, -3.07) * mm, "end": v(-428.1, -3.14) * mm});
            skLineSegment(sketch, "E343", {"start": v(-428.1, -3.14) * mm, "end": v(-428.27, -3.2) * mm});
            skLineSegment(sketch, "E344", {"start": v(-428.27, -3.2) * mm, "end": v(-428.45, -3.24) * mm});
            skLineSegment(sketch, "E345", {"start": v(-428.45, -3.24) * mm, "end": v(-428.64, -3.27) * mm});
            skLineSegment(sketch, "E346", {"start": v(-428.64, -3.27) * mm, "end": v(-428.82, -3.3) * mm});
            skLineSegment(sketch, "E347", {"start": v(-428.82, -3.3) * mm, "end": v(-434.15, -3.3) * mm});
            skLineSegment(sketch, "E348", {"start": v(-434.15, -3.3) * mm, "end": v(-434.9, -3.24) * mm});
            skLineSegment(sketch, "E349", {"start": v(-434.9, -3.24) * mm, "end": v(-435.59, -3.14) * mm});
            skLineSegment(sketch, "E350", {"start": v(-435.59, -3.14) * mm, "end": v(-436.28, -2.97) * mm});
            skLineSegment(sketch, "E351", {"start": v(-436.28, -2.97) * mm, "end": v(-436.93, -2.74) * mm});
            skLineSegment(sketch, "E352", {"start": v(-436.93, -2.74) * mm, "end": v(-437.55, -2.45) * mm});
            skLineSegment(sketch, "E353", {"start": v(-437.55, -2.45) * mm, "end": v(-438.17, -2.08) * mm});
            skLineSegment(sketch, "E354", {"start": v(-438.17, -2.08) * mm, "end": v(-438.74, -1.65) * mm});
            skLineSegment(sketch, "E355", {"start": v(-438.74, -1.65) * mm, "end": v(-439.28, -1.16) * mm});
            skLineSegment(sketch, "E356", {"start": v(-439.28, -1.16) * mm, "end": v(-439.78, -0.61) * mm});
            skLineSegment(sketch, "E357", {"start": v(-439.78, -0.61) * mm, "end": v(-440.2, -0.04) * mm});
            skLineSegment(sketch, "E358", {"start": v(-440.2, -0.04) * mm, "end": v(-440.57, 0.58) * mm});
            skLineSegment(sketch, "E359", {"start": v(-440.57, 0.58) * mm, "end": v(-440.87, 1.2) * mm});
            skLineSegment(sketch, "E360", {"start": v(-440.87, 1.2) * mm, "end": v(-441.1, 1.84) * mm});
            skLineSegment(sketch, "E361", {"start": v(-441.1, 1.84) * mm, "end": v(-441.27, 2.54) * mm});
            skLineSegment(sketch, "E362", {"start": v(-441.27, 2.54) * mm, "end": v(-441.37, 3.23) * mm});
            skLineSegment(sketch, "E363", {"start": v(-421.05, 6.68) * mm, "end": v(-420.95, 7.38) * mm});
            skLineSegment(sketch, "E364", {"start": v(-420.95, 7.38) * mm, "end": v(-420.78, 8.07) * mm});
            skLineSegment(sketch, "E365", {"start": v(-420.78, 8.07) * mm, "end": v(-420.56, 8.71) * mm});
            skLineSegment(sketch, "E366", {"start": v(-420.56, 8.71) * mm, "end": v(-420.23, 9.34) * mm});
            skLineSegment(sketch, "E367", {"start": v(-420.23, 9.34) * mm, "end": v(-419.89, 9.96) * mm});
            skLineSegment(sketch, "E368", {"start": v(-419.89, 9.96) * mm, "end": v(-419.44, 10.53) * mm});
            skLineSegment(sketch, "E369", {"start": v(-419.44, 10.53) * mm, "end": v(-418.95, 11.07) * mm});
            skLineSegment(sketch, "E370", {"start": v(-418.95, 11.07) * mm, "end": v(-418.47, 11.52) * mm});
            skLineSegment(sketch, "E371", {"start": v(-418.47, 11.52) * mm, "end": v(-417.95, 11.89) * mm});
            skLineSegment(sketch, "E372", {"start": v(-417.95, 11.89) * mm, "end": v(-417.43, 12.24) * mm});
            skLineSegment(sketch, "E373", {"start": v(-417.43, 12.24) * mm, "end": v(-416.89, 12.53) * mm});
            skLineSegment(sketch, "E374", {"start": v(-416.89, 12.53) * mm, "end": v(-416.32, 12.76) * mm});
            skLineSegment(sketch, "E375", {"start": v(-416.32, 12.76) * mm, "end": v(-415.72, 12.96) * mm});
            skLineSegment(sketch, "E376", {"start": v(-415.72, 12.96) * mm, "end": v(-415.1, 13.08) * mm});
            skLineSegment(sketch, "E377", {"start": v(-415.1, 13.08) * mm, "end": v(-414.48, 13.18) * mm});
            skLineSegment(sketch, "E378", {"start": v(-414.48, 13.18) * mm, "end": v(-414.23, 13.16) * mm});
            skLineSegment(sketch, "E379", {"start": v(-414.23, 13.16) * mm, "end": v(-414, 13.13) * mm});
            skLineSegment(sketch, "E380", {"start": v(-414, 13.13) * mm, "end": v(-413.81, 13.08) * mm});
            skLineSegment(sketch, "E381", {"start": v(-413.81, 13.08) * mm, "end": v(-413.61, 13.03) * mm});
            skLineSegment(sketch, "E382", {"start": v(-413.61, 13.03) * mm, "end": v(-413.41, 12.93) * mm});
            skLineSegment(sketch, "E383", {"start": v(-413.41, 12.93) * mm, "end": v(-413.24, 12.83) * mm});
            skLineSegment(sketch, "E384", {"start": v(-413.24, 12.83) * mm, "end": v(-413.1, 12.73) * mm});
            skLineSegment(sketch, "E385", {"start": v(-413.1, 12.73) * mm, "end": v(-412.94, 12.58) * mm});
            skLineSegment(sketch, "E386", {"start": v(-412.94, 12.58) * mm, "end": v(-412.82, 12.44) * mm});
            skLineSegment(sketch, "E387", {"start": v(-412.82, 12.44) * mm, "end": v(-412.7, 12.29) * mm});
            skLineSegment(sketch, "E388", {"start": v(-412.7, 12.29) * mm, "end": v(-412.6, 12.11) * mm});
            skLineSegment(sketch, "E389", {"start": v(-412.6, 12.11) * mm, "end": v(-412.52, 11.96) * mm});
            skLineSegment(sketch, "E390", {"start": v(-412.52, 11.96) * mm, "end": v(-412.45, 11.8) * mm});
            skLineSegment(sketch, "E391", {"start": v(-412.45, 11.8) * mm, "end": v(-412.4, 11.62) * mm});
            skLineSegment(sketch, "E392", {"start": v(-412.4, 11.62) * mm, "end": v(-412.37, 11.42) * mm});
            skLineSegment(sketch, "E393", {"start": v(-412.37, 11.42) * mm, "end": v(-412.37, 11.25) * mm});
            skLineSegment(sketch, "E394", {"start": v(-412.37, 11.25) * mm, "end": v(-412.37, 11.05) * mm});
            skLineSegment(sketch, "E395", {"start": v(-412.37, 11.05) * mm, "end": v(-412.4, 10.85) * mm});
            skLineSegment(sketch, "E396", {"start": v(-412.4, 10.85) * mm, "end": v(-412.45, 10.67) * mm});
            skLineSegment(sketch, "E397", {"start": v(-412.45, 10.67) * mm, "end": v(-412.52, 10.5) * mm});
            skLineSegment(sketch, "E398", {"start": v(-412.52, 10.5) * mm, "end": v(-412.6, 10.33) * mm});
            skLineSegment(sketch, "E399", {"start": v(-412.6, 10.33) * mm, "end": v(-412.7, 10.18) * mm});
            skLineSegment(sketch, "E400", {"start": v(-412.7, 10.18) * mm, "end": v(-412.8, 10.03) * mm});
            skLineSegment(sketch, "E401", {"start": v(-412.8, 10.03) * mm, "end": v(-412.92, 9.88) * mm});
            skLineSegment(sketch, "E402", {"start": v(-412.92, 9.88) * mm, "end": v(-413.07, 9.76) * mm});
            skLineSegment(sketch, "E403", {"start": v(-413.07, 9.76) * mm, "end": v(-413.2, 9.66) * mm});
            skLineSegment(sketch, "E404", {"start": v(-413.2, 9.66) * mm, "end": v(-413.34, 9.56) * mm});
            skLineSegment(sketch, "E405", {"start": v(-413.34, 9.56) * mm, "end": v(-413.49, 9.48) * mm});
            skLineSegment(sketch, "E406", {"start": v(-413.49, 9.48) * mm, "end": v(-413.64, 9.4) * mm});
            skLineSegment(sketch, "E407", {"start": v(-413.64, 9.4) * mm, "end": v(-413.79, 9.36) * mm});
            skLineSegment(sketch, "E408", {"start": v(-413.79, 9.36) * mm, "end": v(-413.93, 9.34) * mm});
            skLineSegment(sketch, "E409", {"start": v(-413.93, 9.34) * mm, "end": v(-414.1, 9.31) * mm});
            skLineSegment(sketch, "E410", {"start": v(-414.1, 9.31) * mm, "end": v(-414.4, 9.26) * mm});
            skLineSegment(sketch, "E411", {"start": v(-414.4, 9.26) * mm, "end": v(-414.7, 9.21) * mm});
            skLineSegment(sketch, "E412", {"start": v(-414.7, 9.21) * mm, "end": v(-414.98, 9.14) * mm});
            skLineSegment(sketch, "E413", {"start": v(-414.98, 9.14) * mm, "end": v(-415.25, 9.01) * mm});
            skLineSegment(sketch, "E414", {"start": v(-415.25, 9.01) * mm, "end": v(-415.5, 8.89) * mm});
            skLineSegment(sketch, "E415", {"start": v(-415.5, 8.89) * mm, "end": v(-415.75, 8.71) * mm});
            skLineSegment(sketch, "E416", {"start": v(-415.75, 8.71) * mm, "end": v(-416, 8.54) * mm});
            skLineSegment(sketch, "E417", {"start": v(-416, 8.54) * mm, "end": v(-416.22, 8.32) * mm});
            skLineSegment(sketch, "E418", {"start": v(-416.22, 8.32) * mm, "end": v(-416.44, 8.07) * mm});
            skLineSegment(sketch, "E419", {"start": v(-416.44, 8.07) * mm, "end": v(-416.66, 7.8) * mm});
            skLineSegment(sketch, "E420", {"start": v(-416.66, 7.8) * mm, "end": v(-416.81, 7.52) * mm});
            skLineSegment(sketch, "E421", {"start": v(-416.81, 7.52) * mm, "end": v(-416.96, 7.23) * mm});
            skLineSegment(sketch, "E422", {"start": v(-416.96, 7.23) * mm, "end": v(-417.06, 6.93) * mm});
            skLineSegment(sketch, "E423", {"start": v(-417.06, 6.93) * mm, "end": v(-417.16, 6.6) * mm});
            skLineSegment(sketch, "E424", {"start": v(-417.16, 6.6) * mm, "end": v(-417.18, 6.28) * mm});
            skLineSegment(sketch, "E425", {"start": v(-417.18, 6.28) * mm, "end": v(-417.2, 5.94) * mm});
            skLineSegment(sketch, "E426", {"start": v(-417.2, 5.94) * mm, "end": v(-417.2, 3.98) * mm});
            skLineSegment(sketch, "E427", {"start": v(-417.2, 3.98) * mm, "end": v(-417.18, 3.63) * mm});
            skLineSegment(sketch, "E428", {"start": v(-417.18, 3.63) * mm, "end": v(-417.16, 3.3) * mm});
            skLineSegment(sketch, "E429", {"start": v(-417.16, 3.3) * mm, "end": v(-417.06, 2.99) * mm});
            skLineSegment(sketch, "E430", {"start": v(-417.06, 2.99) * mm, "end": v(-416.96, 2.69) * mm});
            skLineSegment(sketch, "E431", {"start": v(-416.96, 2.69) * mm, "end": v(-416.81, 2.39) * mm});
            skLineSegment(sketch, "E432", {"start": v(-416.81, 2.39) * mm, "end": v(-416.66, 2.12) * mm});
            skLineSegment(sketch, "E433", {"start": v(-416.66, 2.12) * mm, "end": v(-416.44, 1.84) * mm});
            skLineSegment(sketch, "E434", {"start": v(-416.44, 1.84) * mm, "end": v(-416.22, 1.57) * mm});
            skLineSegment(sketch, "E435", {"start": v(-416.22, 1.57) * mm, "end": v(-415.97, 1.35) * mm});
            skLineSegment(sketch, "E436", {"start": v(-415.97, 1.35) * mm, "end": v(-415.7, 1.15) * mm});
            skLineSegment(sketch, "E437", {"start": v(-415.7, 1.15) * mm, "end": v(-415.42, 0.98) * mm});
            skLineSegment(sketch, "E438", {"start": v(-415.42, 0.98) * mm, "end": v(-415.13, 0.83) * mm});
            skLineSegment(sketch, "E439", {"start": v(-415.13, 0.83) * mm, "end": v(-414.83, 0.73) * mm});
            skLineSegment(sketch, "E440", {"start": v(-414.83, 0.73) * mm, "end": v(-414.5, 0.65) * mm});
            skLineSegment(sketch, "E441", {"start": v(-414.5, 0.65) * mm, "end": v(-414.16, 0.6) * mm});
            skLineSegment(sketch, "E442", {"start": v(-414.16, 0.6) * mm, "end": v(-413.81, 0.58) * mm});
            skLineSegment(sketch, "E443", {"start": v(-413.81, 0.58) * mm, "end": v(-410.44, 0.58) * mm});
            skLineSegment(sketch, "E444", {"start": v(-410.44, 0.58) * mm, "end": v(-410.44, 14.12) * mm});
            skLineSegment(sketch, "E445", {"start": v(-410.44, 14.12) * mm, "end": v(-410.46, 14.44) * mm});
            skLineSegment(sketch, "E446", {"start": v(-410.46, 14.44) * mm, "end": v(-410.51, 14.8) * mm});
            skLineSegment(sketch, "E447", {"start": v(-410.51, 14.8) * mm, "end": v(-410.59, 15.11) * mm});
            skLineSegment(sketch, "E448", {"start": v(-410.59, 15.11) * mm, "end": v(-410.7, 15.41) * mm});
            skLineSegment(sketch, "E449", {"start": v(-410.7, 15.41) * mm, "end": v(-410.83, 15.7) * mm});
            skLineSegment(sketch, "E450", {"start": v(-410.83, 15.7) * mm, "end": v(-411, 15.98) * mm});
            skLineSegment(sketch, "E451", {"start": v(-411, 15.98) * mm, "end": v(-411.2, 16.26) * mm});
            skLineSegment(sketch, "E452", {"start": v(-411.2, 16.26) * mm, "end": v(-411.43, 16.5) * mm});
            skLineSegment(sketch, "E453", {"start": v(-411.43, 16.5) * mm, "end": v(-411.7, 16.73) * mm});
            skLineSegment(sketch, "E454", {"start": v(-411.7, 16.73) * mm, "end": v(-411.95, 16.95) * mm});
            skLineSegment(sketch, "E455", {"start": v(-411.95, 16.95) * mm, "end": v(-412.25, 17.1) * mm});
            skLineSegment(sketch, "E456", {"start": v(-412.25, 17.1) * mm, "end": v(-412.52, 17.25) * mm});
            skLineSegment(sketch, "E457", {"start": v(-412.52, 17.25) * mm, "end": v(-412.84, 17.35) * mm});
            skLineSegment(sketch, "E458", {"start": v(-412.84, 17.35) * mm, "end": v(-413.17, 17.45) * mm});
            skLineSegment(sketch, "E459", {"start": v(-413.17, 17.45) * mm, "end": v(-413.49, 17.47) * mm});
            skLineSegment(sketch, "E460", {"start": v(-413.49, 17.47) * mm, "end": v(-413.84, 17.5) * mm});
            skLineSegment(sketch, "E461", {"start": v(-413.84, 17.5) * mm, "end": v(-414.18, 17.47) * mm});
            skLineSegment(sketch, "E462", {"start": v(-414.18, 17.47) * mm, "end": v(-414.53, 17.42) * mm});
            skLineSegment(sketch, "E463", {"start": v(-414.53, 17.42) * mm, "end": v(-414.85, 17.35) * mm});
            skLineSegment(sketch, "E464", {"start": v(-414.85, 17.35) * mm, "end": v(-415.15, 17.25) * mm});
            skLineSegment(sketch, "E465", {"start": v(-415.15, 17.25) * mm, "end": v(-415.45, 17.1) * mm});
            skLineSegment(sketch, "E466", {"start": v(-415.45, 17.1) * mm, "end": v(-415.75, 16.93) * mm});
            skLineSegment(sketch, "E467", {"start": v(-415.75, 16.93) * mm, "end": v(-416.02, 16.73) * mm});
            skLineSegment(sketch, "E468", {"start": v(-416.02, 16.73) * mm, "end": v(-416.3, 16.48) * mm});
            skLineSegment(sketch, "E469", {"start": v(-416.3, 16.48) * mm, "end": v(-416.42, 16.35) * mm});
            skLineSegment(sketch, "E470", {"start": v(-416.42, 16.35) * mm, "end": v(-416.56, 16.23) * mm});
            skLineSegment(sketch, "E471", {"start": v(-416.56, 16.23) * mm, "end": v(-416.74, 16.13) * mm});
            skLineSegment(sketch, "E472", {"start": v(-416.74, 16.13) * mm, "end": v(-416.89, 16.06) * mm});
            skLineSegment(sketch, "E473", {"start": v(-416.89, 16.06) * mm, "end": v(-417.06, 15.98) * mm});
            skLineSegment(sketch, "E474", {"start": v(-417.06, 15.98) * mm, "end": v(-417.26, 15.93) * mm});
            skLineSegment(sketch, "E475", {"start": v(-417.26, 15.93) * mm, "end": v(-417.43, 15.9) * mm});
            skLineSegment(sketch, "E476", {"start": v(-417.43, 15.9) * mm, "end": v(-417.66, 15.9) * mm});
            skLineSegment(sketch, "E477", {"start": v(-417.66, 15.9) * mm, "end": v(-417.83, 15.9) * mm});
            skLineSegment(sketch, "E478", {"start": v(-417.83, 15.9) * mm, "end": v(-418.03, 15.93) * mm});
            skLineSegment(sketch, "E479", {"start": v(-418.03, 15.93) * mm, "end": v(-418.2, 15.98) * mm});
            skLineSegment(sketch, "E480", {"start": v(-418.2, 15.98) * mm, "end": v(-418.37, 16.03) * mm});
            skLineSegment(sketch, "E481", {"start": v(-418.37, 16.03) * mm, "end": v(-418.55, 16.13) * mm});
            skLineSegment(sketch, "E482", {"start": v(-418.55, 16.13) * mm, "end": v(-418.72, 16.23) * mm});
            skLineSegment(sketch, "E483", {"start": v(-418.72, 16.23) * mm, "end": v(-418.87, 16.33) * mm});
            skLineSegment(sketch, "E484", {"start": v(-418.87, 16.33) * mm, "end": v(-419.02, 16.48) * mm});
            skLineSegment(sketch, "E485", {"start": v(-419.02, 16.48) * mm, "end": v(-419.14, 16.6) * mm});
            skLineSegment(sketch, "E486", {"start": v(-419.14, 16.6) * mm, "end": v(-419.27, 16.78) * mm});
            skLineSegment(sketch, "E487", {"start": v(-419.27, 16.78) * mm, "end": v(-419.37, 16.93) * mm});
            skLineSegment(sketch, "E488", {"start": v(-419.37, 16.93) * mm, "end": v(-419.44, 17.1) * mm});
            skLineSegment(sketch, "E489", {"start": v(-419.44, 17.1) * mm, "end": v(-419.5, 17.27) * mm});
            skLineSegment(sketch, "E490", {"start": v(-419.5, 17.27) * mm, "end": v(-419.54, 17.45) * mm});
            skLineSegment(sketch, "E491", {"start": v(-419.54, 17.45) * mm, "end": v(-419.57, 17.64) * mm});
            skLineSegment(sketch, "E492", {"start": v(-419.57, 17.64) * mm, "end": v(-419.6, 17.84) * mm});
            skLineSegment(sketch, "E493", {"start": v(-419.6, 17.84) * mm, "end": v(-419.57, 18.02) * mm});
            skLineSegment(sketch, "E494", {"start": v(-419.57, 18.02) * mm, "end": v(-419.54, 18.22) * mm});
            skLineSegment(sketch, "E495", {"start": v(-419.54, 18.22) * mm, "end": v(-419.5, 18.39) * mm});
            skLineSegment(sketch, "E496", {"start": v(-419.5, 18.39) * mm, "end": v(-419.44, 18.56) * mm});
            skLineSegment(sketch, "E497", {"start": v(-419.44, 18.56) * mm, "end": v(-419.37, 18.74) * mm});
            skLineSegment(sketch, "E498", {"start": v(-419.37, 18.74) * mm, "end": v(-419.27, 18.88) * mm});
            skLineSegment(sketch, "E499", {"start": v(-419.27, 18.88) * mm, "end": v(-419.14, 19.03) * mm});
            skLineSegment(sketch, "E500", {"start": v(-419.14, 19.03) * mm, "end": v(-419.02, 19.18) * mm});
            skLineSegment(sketch, "E501", {"start": v(-419.02, 19.18) * mm, "end": v(-418.47, 19.7) * mm});
            skLineSegment(sketch, "E502", {"start": v(-418.47, 19.7) * mm, "end": v(-417.88, 20.15) * mm});
            skLineSegment(sketch, "E503", {"start": v(-417.88, 20.15) * mm, "end": v(-417.28, 20.52) * mm});
            skLineSegment(sketch, "E504", {"start": v(-417.28, 20.52) * mm, "end": v(-416.64, 20.84) * mm});
            skLineSegment(sketch, "E505", {"start": v(-416.64, 20.84) * mm, "end": v(-415.97, 21.1) * mm});
            skLineSegment(sketch, "E506", {"start": v(-415.97, 21.1) * mm, "end": v(-415.3, 21.24) * mm});
            skLineSegment(sketch, "E507", {"start": v(-415.3, 21.24) * mm, "end": v(-414.58, 21.37) * mm});
            skLineSegment(sketch, "E508", {"start": v(-414.58, 21.37) * mm, "end": v(-413.84, 21.4) * mm});
            skLineSegment(sketch, "E509", {"start": v(-413.84, 21.4) * mm, "end": v(-413.12, 21.37) * mm});
            skLineSegment(sketch, "E510", {"start": v(-413.12, 21.37) * mm, "end": v(-412.4, 21.27) * mm});
            skLineSegment(sketch, "E511", {"start": v(-412.4, 21.27) * mm, "end": v(-411.73, 21.1) * mm});
            skLineSegment(sketch, "E512", {"start": v(-411.73, 21.1) * mm, "end": v(-411.06, 20.87) * mm});
            skLineSegment(sketch, "E513", {"start": v(-411.06, 20.87) * mm, "end": v(-410.44, 20.55) * mm});
            skLineSegment(sketch, "E514", {"start": v(-410.44, 20.55) * mm, "end": v(-409.84, 20.2) * mm});
            skLineSegment(sketch, "E515", {"start": v(-409.84, 20.2) * mm, "end": v(-409.27, 19.75) * mm});
            skLineSegment(sketch, "E516", {"start": v(-409.27, 19.75) * mm, "end": v(-408.73, 19.26) * mm});
            skLineSegment(sketch, "E517", {"start": v(-408.73, 19.26) * mm, "end": v(-408.23, 18.71) * mm});
            skLineSegment(sketch, "E518", {"start": v(-408.23, 18.71) * mm, "end": v(-407.78, 18.14) * mm});
            skLineSegment(sketch, "E519", {"start": v(-407.78, 18.14) * mm, "end": v(-407.41, 17.55) * mm});
            skLineSegment(sketch, "E520", {"start": v(-407.41, 17.55) * mm, "end": v(-407.11, 16.9) * mm});
            skLineSegment(sketch, "E521", {"start": v(-407.11, 16.9) * mm, "end": v(-406.9, 16.26) * mm});
            skLineSegment(sketch, "E522", {"start": v(-406.9, 16.26) * mm, "end": v(-406.72, 15.56) * mm});
            skLineSegment(sketch, "E523", {"start": v(-406.72, 15.56) * mm, "end": v(-406.62, 14.84) * mm});
            skLineSegment(sketch, "E524", {"start": v(-406.62, 14.84) * mm, "end": v(-406.57, 14.12) * mm});
            skLineSegment(sketch, "E525", {"start": v(-406.57, 14.12) * mm, "end": v(-406.57, -1.36) * mm});
            skLineSegment(sketch, "E526", {"start": v(-406.57, -1.36) * mm, "end": v(-406.57, -1.53) * mm});
            skLineSegment(sketch, "E527", {"start": v(-406.57, -1.53) * mm, "end": v(-406.6, -1.73) * mm});
            skLineSegment(sketch, "E528", {"start": v(-406.6, -1.73) * mm, "end": v(-406.64, -1.9) * mm});
            skLineSegment(sketch, "E529", {"start": v(-406.64, -1.9) * mm, "end": v(-406.72, -2.08) * mm});
            skLineSegment(sketch, "E530", {"start": v(-406.72, -2.08) * mm, "end": v(-406.8, -2.25) * mm});
            skLineSegment(sketch, "E531", {"start": v(-406.8, -2.25) * mm, "end": v(-406.9, -2.42) * mm});
            skLineSegment(sketch, "E532", {"start": v(-406.9, -2.42) * mm, "end": v(-407.01, -2.57) * mm});
            skLineSegment(sketch, "E533", {"start": v(-407.01, -2.57) * mm, "end": v(-407.14, -2.72) * mm});
            skLineSegment(sketch, "E534", {"start": v(-407.14, -2.72) * mm, "end": v(-407.29, -2.84) * mm});
            skLineSegment(sketch, "E535", {"start": v(-407.29, -2.84) * mm, "end": v(-407.44, -2.97) * mm});
            skLineSegment(sketch, "E536", {"start": v(-407.44, -2.97) * mm, "end": v(-407.58, -3.07) * mm});
            skLineSegment(sketch, "E537", {"start": v(-407.58, -3.07) * mm, "end": v(-407.76, -3.14) * mm});
            skLineSegment(sketch, "E538", {"start": v(-407.76, -3.14) * mm, "end": v(-407.93, -3.2) * mm});
            skLineSegment(sketch, "E539", {"start": v(-407.93, -3.2) * mm, "end": v(-408.1, -3.24) * mm});
            skLineSegment(sketch, "E540", {"start": v(-408.1, -3.24) * mm, "end": v(-408.3, -3.27) * mm});
            skLineSegment(sketch, "E541", {"start": v(-408.3, -3.27) * mm, "end": v(-408.5, -3.3) * mm});
            skLineSegment(sketch, "E542", {"start": v(-408.5, -3.3) * mm, "end": v(-413.81, -3.3) * mm});
            skLineSegment(sketch, "E543", {"start": v(-413.81, -3.3) * mm, "end": v(-414.55, -3.24) * mm});
            skLineSegment(sketch, "E544", {"start": v(-414.55, -3.24) * mm, "end": v(-415.27, -3.14) * mm});
            skLineSegment(sketch, "E545", {"start": v(-415.27, -3.14) * mm, "end": v(-415.94, -2.97) * mm});
            skLineSegment(sketch, "E546", {"start": v(-415.94, -2.97) * mm, "end": v(-416.61, -2.74) * mm});
            skLineSegment(sketch, "E547", {"start": v(-416.61, -2.74) * mm, "end": v(-417.23, -2.45) * mm});
            skLineSegment(sketch, "E548", {"start": v(-417.23, -2.45) * mm, "end": v(-417.83, -2.08) * mm});
            skLineSegment(sketch, "E549", {"start": v(-417.83, -2.08) * mm, "end": v(-418.4, -1.65) * mm});
            skLineSegment(sketch, "E550", {"start": v(-418.4, -1.65) * mm, "end": v(-418.95, -1.16) * mm});
            skLineSegment(sketch, "E551", {"start": v(-418.95, -1.16) * mm, "end": v(-419.44, -0.61) * mm});
            skLineSegment(sketch, "E552", {"start": v(-419.44, -0.61) * mm, "end": v(-419.89, -0.04) * mm});
            skLineSegment(sketch, "E553", {"start": v(-419.89, -0.04) * mm, "end": v(-420.23, 0.58) * mm});
            skLineSegment(sketch, "E554", {"start": v(-420.23, 0.58) * mm, "end": v(-420.56, 1.2) * mm});
            skLineSegment(sketch, "E555", {"start": v(-420.56, 1.2) * mm, "end": v(-420.78, 1.84) * mm});
            skLineSegment(sketch, "E556", {"start": v(-420.78, 1.84) * mm, "end": v(-420.95, 2.54) * mm});
            skLineSegment(sketch, "E557", {"start": v(-420.95, 2.54) * mm, "end": v(-421.05, 3.23) * mm});
            skLineSegment(sketch, "E558", {"start": v(-421.05, 3.23) * mm, "end": v(-421.08, 3.98) * mm});
            skLineSegment(sketch, "E559", {"start": v(-421.08, 3.98) * mm, "end": v(-421.08, 5.94) * mm});
            skLineSegment(sketch, "E560", {"start": v(-421.08, 5.94) * mm, "end": v(-421.05, 6.68) * mm});
            skLineSegment(sketch, "E561", {"start": v(-401.2, -1.73) * mm, "end": v(-401.23, -1.53) * mm});
            skLineSegment(sketch, "E562", {"start": v(-401.23, -1.53) * mm, "end": v(-401.23, -1.36) * mm});
            skLineSegment(sketch, "E563", {"start": v(-401.23, -1.36) * mm, "end": v(-401.23, 18.98) * mm});
            skLineSegment(sketch, "E564", {"start": v(-401.23, 18.98) * mm, "end": v(-401.23, 19.16) * mm});
            skLineSegment(sketch, "E565", {"start": v(-401.23, 19.16) * mm, "end": v(-401.2, 19.36) * mm});
            skLineSegment(sketch, "E566", {"start": v(-401.2, 19.36) * mm, "end": v(-401.16, 19.53) * mm});
            skLineSegment(sketch, "E567", {"start": v(-401.16, 19.53) * mm, "end": v(-401.09, 19.7) * mm});
            skLineSegment(sketch, "E568", {"start": v(-401.09, 19.7) * mm, "end": v(-401.01, 19.88) * mm});
            skLineSegment(sketch, "E569", {"start": v(-401.01, 19.88) * mm, "end": v(-400.91, 20.05) * mm});
            skLineSegment(sketch, "E570", {"start": v(-400.91, 20.05) * mm, "end": v(-400.79, 20.2) * mm});
            skLineSegment(sketch, "E571", {"start": v(-400.79, 20.2) * mm, "end": v(-400.66, 20.35) * mm});
            skLineSegment(sketch, "E572", {"start": v(-400.66, 20.35) * mm, "end": v(-400.52, 20.47) * mm});
            skLineSegment(sketch, "E573", {"start": v(-400.52, 20.47) * mm, "end": v(-400.37, 20.6) * mm});
            skLineSegment(sketch, "E574", {"start": v(-400.37, 20.6) * mm, "end": v(-400.22, 20.7) * mm});
            skLineSegment(sketch, "E575", {"start": v(-400.22, 20.7) * mm, "end": v(-400.04, 20.77) * mm});
            skLineSegment(sketch, "E576", {"start": v(-400.04, 20.77) * mm, "end": v(-399.87, 20.82) * mm});
            skLineSegment(sketch, "E577", {"start": v(-399.87, 20.82) * mm, "end": v(-399.7, 20.87) * mm});
            skLineSegment(sketch, "E578", {"start": v(-399.7, 20.87) * mm, "end": v(-399.5, 20.9) * mm});
            skLineSegment(sketch, "E579", {"start": v(-399.5, 20.9) * mm, "end": v(-399.3, 20.92) * mm});
            skLineSegment(sketch, "E580", {"start": v(-399.3, 20.92) * mm, "end": v(-394, 20.92) * mm});
            skLineSegment(sketch, "E581", {"start": v(-394, 20.92) * mm, "end": v(-393.25, 20.87) * mm});
            skLineSegment(sketch, "E582", {"start": v(-393.25, 20.87) * mm, "end": v(-392.53, 20.77) * mm});
            skLineSegment(sketch, "E583", {"start": v(-392.53, 20.77) * mm, "end": v(-391.86, 20.6) * mm});
            skLineSegment(sketch, "E584", {"start": v(-391.86, 20.6) * mm, "end": v(-391.19, 20.37) * mm});
            skLineSegment(sketch, "E585", {"start": v(-391.19, 20.37) * mm, "end": v(-390.57, 20.08) * mm});
            skLineSegment(sketch, "E586", {"start": v(-390.57, 20.08) * mm, "end": v(-389.97, 19.7) * mm});
            skLineSegment(sketch, "E587", {"start": v(-389.97, 19.7) * mm, "end": v(-389.4, 19.28) * mm});
            skLineSegment(sketch, "E588", {"start": v(-389.4, 19.28) * mm, "end": v(-388.86, 18.79) * mm});
            skLineSegment(sketch, "E589", {"start": v(-388.86, 18.79) * mm, "end": v(-388.36, 18.24) * mm});
            skLineSegment(sketch, "E590", {"start": v(-388.36, 18.24) * mm, "end": v(-387.91, 17.67) * mm});
            skLineSegment(sketch, "E591", {"start": v(-387.91, 17.67) * mm, "end": v(-387.57, 17.05) * mm});
            skLineSegment(sketch, "E592", {"start": v(-387.57, 17.05) * mm, "end": v(-387.24, 16.43) * mm});
            skLineSegment(sketch, "E593", {"start": v(-387.24, 16.43) * mm, "end": v(-387.02, 15.78) * mm});
            skLineSegment(sketch, "E594", {"start": v(-387.02, 15.78) * mm, "end": v(-386.85, 15.09) * mm});
            skLineSegment(sketch, "E595", {"start": v(-386.85, 15.09) * mm, "end": v(-386.75, 14.4) * mm});
            skLineSegment(sketch, "E596", {"start": v(-386.75, 14.4) * mm, "end": v(-386.72, 13.65) * mm});
            skLineSegment(sketch, "E597", {"start": v(-386.72, 13.65) * mm, "end": v(-386.72, -1.36) * mm});
            skLineSegment(sketch, "E598", {"start": v(-386.72, -1.36) * mm, "end": v(-386.72, -1.53) * mm});
            skLineSegment(sketch, "E599", {"start": v(-386.72, -1.53) * mm, "end": v(-386.75, -1.73) * mm});
            skLineSegment(sketch, "E600", {"start": v(-386.75, -1.73) * mm, "end": v(-386.8, -1.9) * mm});
            skLineSegment(sketch, "E601", {"start": v(-386.8, -1.9) * mm, "end": v(-386.87, -2.08) * mm});
            skLineSegment(sketch, "E602", {"start": v(-386.87, -2.08) * mm, "end": v(-386.95, -2.25) * mm});
            skLineSegment(sketch, "E603", {"start": v(-386.95, -2.25) * mm, "end": v(-387.05, -2.42) * mm});
            skLineSegment(sketch, "E604", {"start": v(-387.05, -2.42) * mm, "end": v(-387.17, -2.57) * mm});
            skLineSegment(sketch, "E605", {"start": v(-387.17, -2.57) * mm, "end": v(-387.3, -2.72) * mm});
            skLineSegment(sketch, "E606", {"start": v(-387.3, -2.72) * mm, "end": v(-387.44, -2.84) * mm});
            skLineSegment(sketch, "E607", {"start": v(-387.44, -2.84) * mm, "end": v(-387.6, -2.97) * mm});
            skLineSegment(sketch, "E608", {"start": v(-387.6, -2.97) * mm, "end": v(-387.74, -3.07) * mm});
            skLineSegment(sketch, "E609", {"start": v(-387.74, -3.07) * mm, "end": v(-387.91, -3.14) * mm});
            skLineSegment(sketch, "E610", {"start": v(-387.91, -3.14) * mm, "end": v(-388.09, -3.2) * mm});
            skLineSegment(sketch, "E611", {"start": v(-388.09, -3.2) * mm, "end": v(-388.26, -3.24) * mm});
            skLineSegment(sketch, "E612", {"start": v(-388.26, -3.24) * mm, "end": v(-388.46, -3.27) * mm});
            skLineSegment(sketch, "E613", {"start": v(-388.46, -3.27) * mm, "end": v(-388.66, -3.3) * mm});
            skLineSegment(sketch, "E614", {"start": v(-388.66, -3.3) * mm, "end": v(-388.86, -3.27) * mm});
            skLineSegment(sketch, "E615", {"start": v(-388.86, -3.27) * mm, "end": v(-389.06, -3.24) * mm});
            skLineSegment(sketch, "E616", {"start": v(-389.06, -3.24) * mm, "end": v(-389.23, -3.2) * mm});
            skLineSegment(sketch, "E617", {"start": v(-389.23, -3.2) * mm, "end": v(-389.4, -3.14) * mm});
            skLineSegment(sketch, "E618", {"start": v(-389.4, -3.14) * mm, "end": v(-389.58, -3.07) * mm});
            skLineSegment(sketch, "E619", {"start": v(-389.58, -3.07) * mm, "end": v(-389.73, -2.97) * mm});
            skLineSegment(sketch, "E620", {"start": v(-389.73, -2.97) * mm, "end": v(-389.87, -2.84) * mm});
            skLineSegment(sketch, "E621", {"start": v(-389.87, -2.84) * mm, "end": v(-390.02, -2.72) * mm});
            skLineSegment(sketch, "E622", {"start": v(-390.02, -2.72) * mm, "end": v(-390.15, -2.57) * mm});
            skLineSegment(sketch, "E623", {"start": v(-390.15, -2.57) * mm, "end": v(-390.27, -2.42) * mm});
            skLineSegment(sketch, "E624", {"start": v(-390.27, -2.42) * mm, "end": v(-390.37, -2.25) * mm});
            skLineSegment(sketch, "E625", {"start": v(-390.37, -2.25) * mm, "end": v(-390.44, -2.08) * mm});
            skLineSegment(sketch, "E626", {"start": v(-390.44, -2.08) * mm, "end": v(-390.52, -1.9) * mm});
            skLineSegment(sketch, "E627", {"start": v(-390.52, -1.9) * mm, "end": v(-390.57, -1.73) * mm});
            skLineSegment(sketch, "E628", {"start": v(-390.57, -1.73) * mm, "end": v(-390.6, -1.53) * mm});
            skLineSegment(sketch, "E629", {"start": v(-390.6, -1.53) * mm, "end": v(-390.6, -1.36) * mm});
            skLineSegment(sketch, "E630", {"start": v(-390.6, -1.36) * mm, "end": v(-390.6, 13.65) * mm});
            skLineSegment(sketch, "E631", {"start": v(-390.6, 13.65) * mm, "end": v(-390.62, 14) * mm});
            skLineSegment(sketch, "E632", {"start": v(-390.62, 14) * mm, "end": v(-390.64, 14.32) * mm});
            skLineSegment(sketch, "E633", {"start": v(-390.64, 14.32) * mm, "end": v(-390.74, 14.64) * mm});
            skLineSegment(sketch, "E634", {"start": v(-390.74, 14.64) * mm, "end": v(-390.84, 14.94) * mm});
            skLineSegment(sketch, "E635", {"start": v(-390.84, 14.94) * mm, "end": v(-391, 15.24) * mm});
            skLineSegment(sketch, "E636", {"start": v(-391, 15.24) * mm, "end": v(-391.14, 15.51) * mm});
            skLineSegment(sketch, "E637", {"start": v(-391.14, 15.51) * mm, "end": v(-391.36, 15.78) * mm});
            skLineSegment(sketch, "E638", {"start": v(-391.36, 15.78) * mm, "end": v(-391.59, 16.06) * mm});
            skLineSegment(sketch, "E639", {"start": v(-391.59, 16.06) * mm, "end": v(-391.83, 16.28) * mm});
            skLineSegment(sketch, "E640", {"start": v(-391.83, 16.28) * mm, "end": v(-392.1, 16.48) * mm});
            skLineSegment(sketch, "E641", {"start": v(-392.1, 16.48) * mm, "end": v(-392.38, 16.65) * mm});
            skLineSegment(sketch, "E642", {"start": v(-392.38, 16.65) * mm, "end": v(-392.68, 16.8) * mm});
            skLineSegment(sketch, "E643", {"start": v(-392.68, 16.8) * mm, "end": v(-392.97, 16.9) * mm});
            skLineSegment(sketch, "E644", {"start": v(-392.97, 16.9) * mm, "end": v(-393.3, 16.97) * mm});
            skLineSegment(sketch, "E645", {"start": v(-393.3, 16.97) * mm, "end": v(-393.64, 17.02) * mm});
            skLineSegment(sketch, "E646", {"start": v(-393.64, 17.02) * mm, "end": v(-394, 17.05) * mm});
            skLineSegment(sketch, "E647", {"start": v(-394, 17.05) * mm, "end": v(-397.37, 17.05) * mm});
            skLineSegment(sketch, "E648", {"start": v(-397.37, 17.05) * mm, "end": v(-397.37, -1.36) * mm});
            skLineSegment(sketch, "E649", {"start": v(-397.37, -1.36) * mm, "end": v(-397.37, -1.53) * mm});
            skLineSegment(sketch, "E650", {"start": v(-397.37, -1.53) * mm, "end": v(-397.39, -1.73) * mm});
            skLineSegment(sketch, "E651", {"start": v(-397.39, -1.73) * mm, "end": v(-397.44, -1.9) * mm});
            skLineSegment(sketch, "E652", {"start": v(-397.44, -1.9) * mm, "end": v(-397.51, -2.08) * mm});
            skLineSegment(sketch, "E653", {"start": v(-397.51, -2.08) * mm, "end": v(-397.59, -2.25) * mm});
            skLineSegment(sketch, "E654", {"start": v(-397.59, -2.25) * mm, "end": v(-397.69, -2.42) * mm});
            skLineSegment(sketch, "E655", {"start": v(-397.69, -2.42) * mm, "end": v(-397.81, -2.57) * mm});
            skLineSegment(sketch, "E656", {"start": v(-397.81, -2.57) * mm, "end": v(-397.94, -2.72) * mm});
            skLineSegment(sketch, "E657", {"start": v(-397.94, -2.72) * mm, "end": v(-398.08, -2.84) * mm});
            skLineSegment(sketch, "E658", {"start": v(-398.08, -2.84) * mm, "end": v(-398.23, -2.97) * mm});
            skLineSegment(sketch, "E659", {"start": v(-398.23, -2.97) * mm, "end": v(-398.38, -3.07) * mm});
            skLineSegment(sketch, "E660", {"start": v(-398.38, -3.07) * mm, "end": v(-398.56, -3.14) * mm});
            skLineSegment(sketch, "E661", {"start": v(-398.56, -3.14) * mm, "end": v(-398.73, -3.2) * mm});
            skLineSegment(sketch, "E662", {"start": v(-398.73, -3.2) * mm, "end": v(-398.9, -3.24) * mm});
            skLineSegment(sketch, "E663", {"start": v(-398.9, -3.24) * mm, "end": v(-399.1, -3.27) * mm});
            skLineSegment(sketch, "E664", {"start": v(-399.1, -3.27) * mm, "end": v(-399.3, -3.3) * mm});
            skLineSegment(sketch, "E665", {"start": v(-399.3, -3.3) * mm, "end": v(-399.5, -3.27) * mm});
            skLineSegment(sketch, "E666", {"start": v(-399.5, -3.27) * mm, "end": v(-399.7, -3.24) * mm});
            skLineSegment(sketch, "E667", {"start": v(-399.7, -3.24) * mm, "end": v(-399.87, -3.2) * mm});
            skLineSegment(sketch, "E668", {"start": v(-399.87, -3.2) * mm, "end": v(-400.04, -3.14) * mm});
            skLineSegment(sketch, "E669", {"start": v(-400.04, -3.14) * mm, "end": v(-400.22, -3.07) * mm});
            skLineSegment(sketch, "E670", {"start": v(-400.22, -3.07) * mm, "end": v(-400.37, -2.97) * mm});
            skLineSegment(sketch, "E671", {"start": v(-400.37, -2.97) * mm, "end": v(-400.52, -2.84) * mm});
            skLineSegment(sketch, "E672", {"start": v(-400.52, -2.84) * mm, "end": v(-400.66, -2.72) * mm});
            skLineSegment(sketch, "E673", {"start": v(-400.66, -2.72) * mm, "end": v(-400.79, -2.57) * mm});
            skLineSegment(sketch, "E674", {"start": v(-400.79, -2.57) * mm, "end": v(-400.91, -2.42) * mm});
            skLineSegment(sketch, "E675", {"start": v(-400.91, -2.42) * mm, "end": v(-401.01, -2.25) * mm});
            skLineSegment(sketch, "E676", {"start": v(-401.01, -2.25) * mm, "end": v(-401.09, -2.08) * mm});
            skLineSegment(sketch, "E677", {"start": v(-401.09, -2.08) * mm, "end": v(-401.16, -1.9) * mm});
            skLineSegment(sketch, "E678", {"start": v(-401.16, -1.9) * mm, "end": v(-401.2, -1.73) * mm});
            skLineSegment(sketch, "E679", {"start": v(-381.86, 18.59) * mm, "end": v(-381.89, 18.79) * mm});
            skLineSegment(sketch, "E680", {"start": v(-381.89, 18.79) * mm, "end": v(-381.89, 18.98) * mm});
            skLineSegment(sketch, "E681", {"start": v(-381.89, 18.98) * mm, "end": v(-381.89, 19.16) * mm});
            skLineSegment(sketch, "E682", {"start": v(-381.89, 19.16) * mm, "end": v(-381.86, 19.36) * mm});
            skLineSegment(sketch, "E683", {"start": v(-381.86, 19.36) * mm, "end": v(-381.81, 19.53) * mm});
            skLineSegment(sketch, "E684", {"start": v(-381.81, 19.53) * mm, "end": v(-381.76, 19.7) * mm});
            skLineSegment(sketch, "E685", {"start": v(-381.76, 19.7) * mm, "end": v(-381.66, 19.88) * mm});
            skLineSegment(sketch, "E686", {"start": v(-381.66, 19.88) * mm, "end": v(-381.56, 20.05) * mm});
            skLineSegment(sketch, "E687", {"start": v(-381.56, 20.05) * mm, "end": v(-381.47, 20.2) * mm});
            skLineSegment(sketch, "E688", {"start": v(-381.47, 20.2) * mm, "end": v(-381.32, 20.35) * mm});
            skLineSegment(sketch, "E689", {"start": v(-381.32, 20.35) * mm, "end": v(-381.22, 20.45) * mm});
            skLineSegment(sketch, "E690", {"start": v(-381.22, 20.45) * mm, "end": v(-381.12, 20.52) * mm});
            skLineSegment(sketch, "E691", {"start": v(-381.12, 20.52) * mm, "end": v(-381.02, 20.6) * mm});
            skLineSegment(sketch, "E692", {"start": v(-381.02, 20.6) * mm, "end": v(-380.9, 20.67) * mm});
            skLineSegment(sketch, "E693", {"start": v(-380.9, 20.67) * mm, "end": v(-380.8, 20.72) * mm});
            skLineSegment(sketch, "E694", {"start": v(-380.8, 20.72) * mm, "end": v(-380.67, 20.77) * mm});
            skLineSegment(sketch, "E695", {"start": v(-380.67, 20.77) * mm, "end": v(-380.55, 20.82) * mm});
            skLineSegment(sketch, "E696", {"start": v(-380.55, 20.82) * mm, "end": v(-380.42, 20.87) * mm});
            skLineSegment(sketch, "E697", {"start": v(-380.42, 20.87) * mm, "end": v(-380.42, 24.76) * mm});
            skLineSegment(sketch, "E698", {"start": v(-380.42, 24.76) * mm, "end": v(-380.42, 24.94) * mm});
            skLineSegment(sketch, "E699", {"start": v(-380.42, 24.94) * mm, "end": v(-380.4, 25.14) * mm});
            skLineSegment(sketch, "E700", {"start": v(-380.4, 25.14) * mm, "end": v(-380.35, 25.3) * mm});
            skLineSegment(sketch, "E701", {"start": v(-380.35, 25.3) * mm, "end": v(-380.27, 25.48) * mm});
            skLineSegment(sketch, "E702", {"start": v(-380.27, 25.48) * mm, "end": v(-380.2, 25.66) * mm});
            skLineSegment(sketch, "E703", {"start": v(-380.2, 25.66) * mm, "end": v(-380.1, 25.83) * mm});
            skLineSegment(sketch, "E704", {"start": v(-380.1, 25.83) * mm, "end": v(-379.98, 25.98) * mm});
            skLineSegment(sketch, "E705", {"start": v(-379.98, 25.98) * mm, "end": v(-379.85, 26.13) * mm});
            skLineSegment(sketch, "E706", {"start": v(-379.85, 26.13) * mm, "end": v(-379.7, 26.25) * mm});
            skLineSegment(sketch, "E707", {"start": v(-379.7, 26.25) * mm, "end": v(-379.53, 26.38) * mm});
            skLineSegment(sketch, "E708", {"start": v(-379.53, 26.38) * mm, "end": v(-379.38, 26.48) * mm});
            skLineSegment(sketch, "E709", {"start": v(-379.38, 26.48) * mm, "end": v(-379.2, 26.55) * mm});
            skLineSegment(sketch, "E710", {"start": v(-379.2, 26.55) * mm, "end": v(-379.03, 26.6) * mm});
            skLineSegment(sketch, "E711", {"start": v(-379.03, 26.6) * mm, "end": v(-378.86, 26.65) * mm});
            skLineSegment(sketch, "E712", {"start": v(-378.86, 26.65) * mm, "end": v(-378.69, 26.67) * mm});
            skLineSegment(sketch, "E713", {"start": v(-378.69, 26.67) * mm, "end": v(-378.49, 26.7) * mm});
            skLineSegment(sketch, "E714", {"start": v(-378.49, 26.7) * mm, "end": v(-378.3, 26.67) * mm});
            skLineSegment(sketch, "E715", {"start": v(-378.3, 26.67) * mm, "end": v(-378.1, 26.65) * mm});
            skLineSegment(sketch, "E716", {"start": v(-378.1, 26.65) * mm, "end": v(-377.92, 26.6) * mm});
            skLineSegment(sketch, "E717", {"start": v(-377.92, 26.6) * mm, "end": v(-377.74, 26.55) * mm});
            skLineSegment(sketch, "E718", {"start": v(-377.74, 26.55) * mm, "end": v(-377.57, 26.48) * mm});
            skLineSegment(sketch, "E719", {"start": v(-377.57, 26.48) * mm, "end": v(-377.42, 26.38) * mm});
            skLineSegment(sketch, "E720", {"start": v(-377.42, 26.38) * mm, "end": v(-377.27, 26.25) * mm});
            skLineSegment(sketch, "E721", {"start": v(-377.27, 26.25) * mm, "end": v(-377.12, 26.13) * mm});
            skLineSegment(sketch, "E722", {"start": v(-377.12, 26.13) * mm, "end": v(-377, 25.98) * mm});
            skLineSegment(sketch, "E723", {"start": v(-377, 25.98) * mm, "end": v(-376.88, 25.83) * mm});
            skLineSegment(sketch, "E724", {"start": v(-376.88, 25.83) * mm, "end": v(-376.78, 25.66) * mm});
            skLineSegment(sketch, "E725", {"start": v(-376.78, 25.66) * mm, "end": v(-376.7, 25.48) * mm});
            skLineSegment(sketch, "E726", {"start": v(-376.7, 25.48) * mm, "end": v(-376.63, 25.3) * mm});
            skLineSegment(sketch, "E727", {"start": v(-376.63, 25.3) * mm, "end": v(-376.58, 25.14) * mm});
            skLineSegment(sketch, "E728", {"start": v(-376.58, 25.14) * mm, "end": v(-376.55, 24.94) * mm});
            skLineSegment(sketch, "E729", {"start": v(-376.55, 24.94) * mm, "end": v(-376.55, 24.76) * mm});
            skLineSegment(sketch, "E730", {"start": v(-376.55, 24.76) * mm, "end": v(-376.55, 20.92) * mm});
            skLineSegment(sketch, "E731", {"start": v(-376.55, 20.92) * mm, "end": v(-374.12, 20.92) * mm});
            skLineSegment(sketch, "E732", {"start": v(-374.12, 20.92) * mm, "end": v(-373.95, 20.9) * mm});
            skLineSegment(sketch, "E733", {"start": v(-373.95, 20.9) * mm, "end": v(-373.75, 20.87) * mm});
            skLineSegment(sketch, "E734", {"start": v(-373.75, 20.87) * mm, "end": v(-373.58, 20.82) * mm});
            skLineSegment(sketch, "E735", {"start": v(-373.58, 20.82) * mm, "end": v(-373.4, 20.77) * mm});
            skLineSegment(sketch, "E736", {"start": v(-373.4, 20.77) * mm, "end": v(-373.23, 20.7) * mm});
            skLineSegment(sketch, "E737", {"start": v(-373.23, 20.7) * mm, "end": v(-373.06, 20.6) * mm});
            skLineSegment(sketch, "E738", {"start": v(-373.06, 20.6) * mm, "end": v(-372.9, 20.47) * mm});
            skLineSegment(sketch, "E739", {"start": v(-372.9, 20.47) * mm, "end": v(-372.76, 20.35) * mm});
            skLineSegment(sketch, "E740", {"start": v(-372.76, 20.35) * mm, "end": v(-372.63, 20.2) * mm});
            skLineSegment(sketch, "E741", {"start": v(-372.63, 20.2) * mm, "end": v(-372.51, 20.05) * mm});
            skLineSegment(sketch, "E742", {"start": v(-372.51, 20.05) * mm, "end": v(-372.41, 19.88) * mm});
            skLineSegment(sketch, "E743", {"start": v(-372.41, 19.88) * mm, "end": v(-372.34, 19.7) * mm});
            skLineSegment(sketch, "E744", {"start": v(-372.34, 19.7) * mm, "end": v(-372.29, 19.53) * mm});
            skLineSegment(sketch, "E745", {"start": v(-372.29, 19.53) * mm, "end": v(-372.24, 19.36) * mm});
            skLineSegment(sketch, "E746", {"start": v(-372.24, 19.36) * mm, "end": v(-372.21, 19.16) * mm});
            skLineSegment(sketch, "E747", {"start": v(-372.21, 19.16) * mm, "end": v(-372.19, 18.98) * mm});
            skLineSegment(sketch, "E748", {"start": v(-372.19, 18.98) * mm, "end": v(-372.21, 18.79) * mm});
            skLineSegment(sketch, "E749", {"start": v(-372.21, 18.79) * mm, "end": v(-372.24, 18.59) * mm});
            skLineSegment(sketch, "E750", {"start": v(-372.24, 18.59) * mm, "end": v(-372.29, 18.41) * mm});
            skLineSegment(sketch, "E751", {"start": v(-372.29, 18.41) * mm, "end": v(-372.34, 18.24) * mm});
            skLineSegment(sketch, "E752", {"start": v(-372.34, 18.24) * mm, "end": v(-372.41, 18.07) * mm});
            skLineSegment(sketch, "E753", {"start": v(-372.41, 18.07) * mm, "end": v(-372.51, 17.9) * mm});
            skLineSegment(sketch, "E754", {"start": v(-372.51, 17.9) * mm, "end": v(-372.63, 17.74) * mm});
            skLineSegment(sketch, "E755", {"start": v(-372.63, 17.74) * mm, "end": v(-372.76, 17.6) * mm});
            skLineSegment(sketch, "E756", {"start": v(-372.76, 17.6) * mm, "end": v(-372.9, 17.47) * mm});
            skLineSegment(sketch, "E757", {"start": v(-372.9, 17.47) * mm, "end": v(-373.06, 17.35) * mm});
            skLineSegment(sketch, "E758", {"start": v(-373.06, 17.35) * mm, "end": v(-373.23, 17.25) * mm});
            skLineSegment(sketch, "E759", {"start": v(-373.23, 17.25) * mm, "end": v(-373.4, 17.17) * mm});
            skLineSegment(sketch, "E760", {"start": v(-373.4, 17.17) * mm, "end": v(-373.58, 17.12) * mm});
            skLineSegment(sketch, "E761", {"start": v(-373.58, 17.12) * mm, "end": v(-373.75, 17.07) * mm});
            skLineSegment(sketch, "E762", {"start": v(-373.75, 17.07) * mm, "end": v(-373.95, 17.05) * mm});
            skLineSegment(sketch, "E763", {"start": v(-373.95, 17.05) * mm, "end": v(-374.12, 17.05) * mm});
            skLineSegment(sketch, "E764", {"start": v(-374.12, 17.05) * mm, "end": v(-376.55, 17.05) * mm});
            skLineSegment(sketch, "E765", {"start": v(-376.55, 17.05) * mm, "end": v(-376.55, 3) * mm});
            skLineSegment(sketch, "E766", {"start": v(-376.55, 3) * mm, "end": v(-376.55, 2.76) * mm});
            skLineSegment(sketch, "E767", {"start": v(-376.55, 2.76) * mm, "end": v(-376.5, 2.51) * mm});
            skLineSegment(sketch, "E768", {"start": v(-376.5, 2.51) * mm, "end": v(-376.45, 2.3) * mm});
            skLineSegment(sketch, "E769", {"start": v(-376.45, 2.3) * mm, "end": v(-376.38, 2.07) * mm});
            skLineSegment(sketch, "E770", {"start": v(-376.38, 2.07) * mm, "end": v(-376.28, 1.87) * mm});
            skLineSegment(sketch, "E771", {"start": v(-376.28, 1.87) * mm, "end": v(-376.16, 1.67) * mm});
            skLineSegment(sketch, "E772", {"start": v(-376.16, 1.67) * mm, "end": v(-376, 1.47) * mm});
            skLineSegment(sketch, "E773", {"start": v(-376, 1.47) * mm, "end": v(-375.86, 1.3) * mm});
            skLineSegment(sketch, "E774", {"start": v(-375.86, 1.3) * mm, "end": v(-375.66, 1.12) * mm});
            skLineSegment(sketch, "E775", {"start": v(-375.66, 1.12) * mm, "end": v(-375.49, 0.98) * mm});
            skLineSegment(sketch, "E776", {"start": v(-375.49, 0.98) * mm, "end": v(-375.29, 0.88) * mm});
            skLineSegment(sketch, "E777", {"start": v(-375.29, 0.88) * mm, "end": v(-375.07, 0.78) * mm});
            skLineSegment(sketch, "E778", {"start": v(-375.07, 0.78) * mm, "end": v(-374.84, 0.68) * mm});
            skLineSegment(sketch, "E779", {"start": v(-374.84, 0.68) * mm, "end": v(-374.62, 0.63) * mm});
            skLineSegment(sketch, "E780", {"start": v(-374.62, 0.63) * mm, "end": v(-374.4, 0.6) * mm});
            skLineSegment(sketch, "E781", {"start": v(-374.4, 0.6) * mm, "end": v(-374.12, 0.58) * mm});
            skLineSegment(sketch, "E782", {"start": v(-374.12, 0.58) * mm, "end": v(-373.92, 0.58) * mm});
            skLineSegment(sketch, "E783", {"start": v(-373.92, 0.58) * mm, "end": v(-373.75, 0.55) * mm});
            skLineSegment(sketch, "E784", {"start": v(-373.75, 0.55) * mm, "end": v(-373.55, 0.5) * mm});
            skLineSegment(sketch, "E785", {"start": v(-373.55, 0.5) * mm, "end": v(-373.38, 0.46) * mm});
            skLineSegment(sketch, "E786", {"start": v(-373.38, 0.46) * mm, "end": v(-373.2, 0.36) * mm});
            skLineSegment(sketch, "E787", {"start": v(-373.2, 0.36) * mm, "end": v(-373.06, 0.26) * mm});
            skLineSegment(sketch, "E788", {"start": v(-373.06, 0.26) * mm, "end": v(-372.88, 0.16) * mm});
            skLineSegment(sketch, "E789", {"start": v(-372.88, 0.16) * mm, "end": v(-372.73, 0) * mm});
            skLineSegment(sketch, "E790", {"start": v(-372.73, 0) * mm, "end": v(-372.6, -0.14) * mm});
            skLineSegment(sketch, "E791", {"start": v(-372.6, -0.14) * mm, "end": v(-372.49, -0.29) * mm});
            skLineSegment(sketch, "E792", {"start": v(-372.49, -0.29) * mm, "end": v(-372.39, -0.46) * mm});
            skLineSegment(sketch, "E793", {"start": v(-372.39, -0.46) * mm, "end": v(-372.31, -0.61) * mm});
            skLineSegment(sketch, "E794", {"start": v(-372.31, -0.61) * mm, "end": v(-372.26, -0.79) * mm});
            skLineSegment(sketch, "E795", {"start": v(-372.26, -0.79) * mm, "end": v(-372.21, -0.96) * mm});
            skLineSegment(sketch, "E796", {"start": v(-372.21, -0.96) * mm, "end": v(-372.19, -1.16) * mm});
            skLineSegment(sketch, "E797", {"start": v(-372.19, -1.16) * mm, "end": v(-372.19, -1.36) * mm});
            skLineSegment(sketch, "E798", {"start": v(-372.19, -1.36) * mm, "end": v(-372.19, -1.53) * mm});
            skLineSegment(sketch, "E799", {"start": v(-372.19, -1.53) * mm, "end": v(-372.21, -1.73) * mm});
            skLineSegment(sketch, "E800", {"start": v(-372.21, -1.73) * mm, "end": v(-372.26, -1.9) * mm});
            skLineSegment(sketch, "E801", {"start": v(-372.26, -1.9) * mm, "end": v(-372.31, -2.08) * mm});
            skLineSegment(sketch, "E802", {"start": v(-372.31, -2.08) * mm, "end": v(-372.39, -2.25) * mm});
            skLineSegment(sketch, "E803", {"start": v(-372.39, -2.25) * mm, "end": v(-372.49, -2.42) * mm});
            skLineSegment(sketch, "E804", {"start": v(-372.49, -2.42) * mm, "end": v(-372.6, -2.57) * mm});
            skLineSegment(sketch, "E805", {"start": v(-372.6, -2.57) * mm, "end": v(-372.73, -2.72) * mm});
            skLineSegment(sketch, "E806", {"start": v(-372.73, -2.72) * mm, "end": v(-372.88, -2.84) * mm});
            skLineSegment(sketch, "E807", {"start": v(-372.88, -2.84) * mm, "end": v(-373.06, -2.97) * mm});
            skLineSegment(sketch, "E808", {"start": v(-373.06, -2.97) * mm, "end": v(-373.2, -3.07) * mm});
            skLineSegment(sketch, "E809", {"start": v(-373.2, -3.07) * mm, "end": v(-373.38, -3.14) * mm});
            skLineSegment(sketch, "E810", {"start": v(-373.38, -3.14) * mm, "end": v(-373.55, -3.2) * mm});
            skLineSegment(sketch, "E811", {"start": v(-373.55, -3.2) * mm, "end": v(-373.75, -3.24) * mm});
            skLineSegment(sketch, "E812", {"start": v(-373.75, -3.24) * mm, "end": v(-373.92, -3.27) * mm});
            skLineSegment(sketch, "E813", {"start": v(-373.92, -3.27) * mm, "end": v(-374.12, -3.3) * mm});
            skLineSegment(sketch, "E814", {"start": v(-374.12, -3.3) * mm, "end": v(-374.77, -3.24) * mm});
            skLineSegment(sketch, "E815", {"start": v(-374.77, -3.24) * mm, "end": v(-375.39, -3.17) * mm});
            skLineSegment(sketch, "E816", {"start": v(-375.39, -3.17) * mm, "end": v(-375.98, -3.02) * mm});
            skLineSegment(sketch, "E817", {"start": v(-375.98, -3.02) * mm, "end": v(-376.53, -2.82) * mm});
            skLineSegment(sketch, "E818", {"start": v(-376.53, -2.82) * mm, "end": v(-377.07, -2.55) * mm});
            skLineSegment(sketch, "E819", {"start": v(-377.07, -2.55) * mm, "end": v(-377.6, -2.25) * mm});
            skLineSegment(sketch, "E820", {"start": v(-377.6, -2.25) * mm, "end": v(-378.1, -1.85) * mm});
            skLineSegment(sketch, "E821", {"start": v(-378.1, -1.85) * mm, "end": v(-378.56, -1.43) * mm});
            skLineSegment(sketch, "E822", {"start": v(-378.56, -1.43) * mm, "end": v(-379, -0.96) * mm});
            skLineSegment(sketch, "E823", {"start": v(-379, -0.96) * mm, "end": v(-379.38, -0.46) * mm});
            skLineSegment(sketch, "E824", {"start": v(-379.38, -0.46) * mm, "end": v(-379.7, 0.06) * mm});
            skLineSegment(sketch, "E825", {"start": v(-379.7, 0.06) * mm, "end": v(-379.95, 0.6) * mm});
            skLineSegment(sketch, "E826", {"start": v(-379.95, 0.6) * mm, "end": v(-380.18, 1.17) * mm});
            skLineSegment(sketch, "E827", {"start": v(-380.18, 1.17) * mm, "end": v(-380.3, 1.77) * mm});
            skLineSegment(sketch, "E828", {"start": v(-380.3, 1.77) * mm, "end": v(-380.4, 2.36) * mm});
            skLineSegment(sketch, "E829", {"start": v(-380.4, 2.36) * mm, "end": v(-380.42, 3) * mm});
            skLineSegment(sketch, "E830", {"start": v(-380.42, 3) * mm, "end": v(-380.42, 17.07) * mm});
            skLineSegment(sketch, "E831", {"start": v(-380.42, 17.07) * mm, "end": v(-380.55, 17.12) * mm});
            skLineSegment(sketch, "E832", {"start": v(-380.55, 17.12) * mm, "end": v(-380.67, 17.17) * mm});
            skLineSegment(sketch, "E833", {"start": v(-380.67, 17.17) * mm, "end": v(-380.8, 17.22) * mm});
            skLineSegment(sketch, "E834", {"start": v(-380.8, 17.22) * mm, "end": v(-380.9, 17.27) * mm});
            skLineSegment(sketch, "E835", {"start": v(-380.9, 17.27) * mm, "end": v(-381.02, 17.35) * mm});
            skLineSegment(sketch, "E836", {"start": v(-381.02, 17.35) * mm, "end": v(-381.12, 17.42) * mm});
            skLineSegment(sketch, "E837", {"start": v(-381.12, 17.42) * mm, "end": v(-381.22, 17.52) * mm});
            skLineSegment(sketch, "E838", {"start": v(-381.22, 17.52) * mm, "end": v(-381.32, 17.62) * mm});
            skLineSegment(sketch, "E839", {"start": v(-381.32, 17.62) * mm, "end": v(-381.47, 17.77) * mm});
            skLineSegment(sketch, "E840", {"start": v(-381.47, 17.77) * mm, "end": v(-381.56, 17.92) * mm});
            skLineSegment(sketch, "E841", {"start": v(-381.56, 17.92) * mm, "end": v(-381.66, 18.1) * mm});
            skLineSegment(sketch, "E842", {"start": v(-381.66, 18.1) * mm, "end": v(-381.76, 18.24) * mm});
            skLineSegment(sketch, "E843", {"start": v(-381.76, 18.24) * mm, "end": v(-381.81, 18.41) * mm});
            skLineSegment(sketch, "E844", {"start": v(-381.81, 18.41) * mm, "end": v(-381.86, 18.59) * mm});
            skLineSegment(sketch, "E845", {"start": v(-368.3, 3.23) * mm, "end": v(-368.34, 3.98) * mm});
            skLineSegment(sketch, "E846", {"start": v(-368.34, 3.98) * mm, "end": v(-368.34, 18.98) * mm});
            skLineSegment(sketch, "E847", {"start": v(-368.34, 18.98) * mm, "end": v(-368.32, 19.16) * mm});
            skLineSegment(sketch, "E848", {"start": v(-368.32, 19.16) * mm, "end": v(-368.3, 19.36) * mm});
            skLineSegment(sketch, "E849", {"start": v(-368.3, 19.36) * mm, "end": v(-368.24, 19.53) * mm});
            skLineSegment(sketch, "E850", {"start": v(-368.24, 19.53) * mm, "end": v(-368.2, 19.7) * mm});
            skLineSegment(sketch, "E851", {"start": v(-368.2, 19.7) * mm, "end": v(-368.12, 19.88) * mm});
            skLineSegment(sketch, "E852", {"start": v(-368.12, 19.88) * mm, "end": v(-368.02, 20.05) * mm});
            skLineSegment(sketch, "E853", {"start": v(-368.02, 20.05) * mm, "end": v(-367.9, 20.2) * mm});
            skLineSegment(sketch, "E854", {"start": v(-367.9, 20.2) * mm, "end": v(-367.77, 20.35) * mm});
            skLineSegment(sketch, "E855", {"start": v(-367.77, 20.35) * mm, "end": v(-367.62, 20.47) * mm});
            skLineSegment(sketch, "E856", {"start": v(-367.62, 20.47) * mm, "end": v(-367.48, 20.6) * mm});
            skLineSegment(sketch, "E857", {"start": v(-367.48, 20.6) * mm, "end": v(-367.3, 20.7) * mm});
            skLineSegment(sketch, "E858", {"start": v(-367.3, 20.7) * mm, "end": v(-367.13, 20.77) * mm});
            skLineSegment(sketch, "E859", {"start": v(-367.13, 20.77) * mm, "end": v(-366.95, 20.82) * mm});
            skLineSegment(sketch, "E860", {"start": v(-366.95, 20.82) * mm, "end": v(-366.78, 20.87) * mm});
            skLineSegment(sketch, "E861", {"start": v(-366.78, 20.87) * mm, "end": v(-366.58, 20.9) * mm});
            skLineSegment(sketch, "E862", {"start": v(-366.58, 20.9) * mm, "end": v(-366.4, 20.92) * mm});
            skLineSegment(sketch, "E863", {"start": v(-366.4, 20.92) * mm, "end": v(-366.21, 20.9) * mm});
            skLineSegment(sketch, "E864", {"start": v(-366.21, 20.9) * mm, "end": v(-366.01, 20.87) * mm});
            skLineSegment(sketch, "E865", {"start": v(-366.01, 20.87) * mm, "end": v(-365.84, 20.82) * mm});
            skLineSegment(sketch, "E866", {"start": v(-365.84, 20.82) * mm, "end": v(-365.66, 20.77) * mm});
            skLineSegment(sketch, "E867", {"start": v(-365.66, 20.77) * mm, "end": v(-365.5, 20.7) * mm});
            skLineSegment(sketch, "E868", {"start": v(-365.5, 20.7) * mm, "end": v(-365.32, 20.6) * mm});
            skLineSegment(sketch, "E869", {"start": v(-365.32, 20.6) * mm, "end": v(-365.17, 20.47) * mm});
            skLineSegment(sketch, "E870", {"start": v(-365.17, 20.47) * mm, "end": v(-365.02, 20.35) * mm});
            skLineSegment(sketch, "E871", {"start": v(-365.02, 20.35) * mm, "end": v(-364.9, 20.2) * mm});
            skLineSegment(sketch, "E872", {"start": v(-364.9, 20.2) * mm, "end": v(-364.77, 20.05) * mm});
            skLineSegment(sketch, "E873", {"start": v(-364.77, 20.05) * mm, "end": v(-364.67, 19.88) * mm});
            skLineSegment(sketch, "E874", {"start": v(-364.67, 19.88) * mm, "end": v(-364.6, 19.7) * mm});
            skLineSegment(sketch, "E875", {"start": v(-364.6, 19.7) * mm, "end": v(-364.55, 19.53) * mm});
            skLineSegment(sketch, "E876", {"start": v(-364.55, 19.53) * mm, "end": v(-364.5, 19.36) * mm});
            skLineSegment(sketch, "E877", {"start": v(-364.5, 19.36) * mm, "end": v(-364.47, 19.16) * mm});
            skLineSegment(sketch, "E878", {"start": v(-364.47, 19.16) * mm, "end": v(-364.47, 18.98) * mm});
            skLineSegment(sketch, "E879", {"start": v(-364.47, 18.98) * mm, "end": v(-364.47, 3.98) * mm});
            skLineSegment(sketch, "E880", {"start": v(-364.47, 3.98) * mm, "end": v(-364.45, 3.63) * mm});
            skLineSegment(sketch, "E881", {"start": v(-364.45, 3.63) * mm, "end": v(-364.4, 3.3) * mm});
            skLineSegment(sketch, "E882", {"start": v(-364.4, 3.3) * mm, "end": v(-364.33, 2.99) * mm});
            skLineSegment(sketch, "E883", {"start": v(-364.33, 2.99) * mm, "end": v(-364.23, 2.69) * mm});
            skLineSegment(sketch, "E884", {"start": v(-364.23, 2.69) * mm, "end": v(-364.08, 2.39) * mm});
            skLineSegment(sketch, "E885", {"start": v(-364.08, 2.39) * mm, "end": v(-363.9, 2.12) * mm});
            skLineSegment(sketch, "E886", {"start": v(-363.9, 2.12) * mm, "end": v(-363.7, 1.84) * mm});
            skLineSegment(sketch, "E887", {"start": v(-363.7, 1.84) * mm, "end": v(-363.48, 1.57) * mm});
            skLineSegment(sketch, "E888", {"start": v(-363.48, 1.57) * mm, "end": v(-363.2, 1.35) * mm});
            skLineSegment(sketch, "E889", {"start": v(-363.2, 1.35) * mm, "end": v(-362.94, 1.15) * mm});
            skLineSegment(sketch, "E890", {"start": v(-362.94, 1.15) * mm, "end": v(-362.66, 0.98) * mm});
            skLineSegment(sketch, "E891", {"start": v(-362.66, 0.98) * mm, "end": v(-362.37, 0.83) * mm});
            skLineSegment(sketch, "E892", {"start": v(-362.37, 0.83) * mm, "end": v(-362.07, 0.73) * mm});
            skLineSegment(sketch, "E893", {"start": v(-362.07, 0.73) * mm, "end": v(-361.75, 0.65) * mm});
            skLineSegment(sketch, "E894", {"start": v(-361.75, 0.65) * mm, "end": v(-361.42, 0.6) * mm});
            skLineSegment(sketch, "E895", {"start": v(-361.42, 0.6) * mm, "end": v(-361.08, 0.58) * mm});
            skLineSegment(sketch, "E896", {"start": v(-361.08, 0.58) * mm, "end": v(-357.68, 0.58) * mm});
            skLineSegment(sketch, "E897", {"start": v(-357.68, 0.58) * mm, "end": v(-357.68, 18.98) * mm});
            skLineSegment(sketch, "E898", {"start": v(-357.68, 18.98) * mm, "end": v(-357.68, 19.16) * mm});
            skLineSegment(sketch, "E899", {"start": v(-357.68, 19.16) * mm, "end": v(-357.65, 19.36) * mm});
            skLineSegment(sketch, "E900", {"start": v(-357.65, 19.36) * mm, "end": v(-357.6, 19.53) * mm});
            skLineSegment(sketch, "E901", {"start": v(-357.6, 19.53) * mm, "end": v(-357.55, 19.7) * mm});
            skLineSegment(sketch, "E902", {"start": v(-357.55, 19.7) * mm, "end": v(-357.48, 19.88) * mm});
            skLineSegment(sketch, "E903", {"start": v(-357.48, 19.88) * mm, "end": v(-357.38, 20.05) * mm});
            skLineSegment(sketch, "E904", {"start": v(-357.38, 20.05) * mm, "end": v(-357.26, 20.2) * mm});
            skLineSegment(sketch, "E905", {"start": v(-357.26, 20.2) * mm, "end": v(-357.13, 20.35) * mm});
            skLineSegment(sketch, "E906", {"start": v(-357.13, 20.35) * mm, "end": v(-356.98, 20.47) * mm});
            skLineSegment(sketch, "E907", {"start": v(-356.98, 20.47) * mm, "end": v(-356.83, 20.6) * mm});
            skLineSegment(sketch, "E908", {"start": v(-356.83, 20.6) * mm, "end": v(-356.66, 20.7) * mm});
            skLineSegment(sketch, "E909", {"start": v(-356.66, 20.7) * mm, "end": v(-356.49, 20.77) * mm});
            skLineSegment(sketch, "E910", {"start": v(-356.49, 20.77) * mm, "end": v(-356.31, 20.82) * mm});
            skLineSegment(sketch, "E911", {"start": v(-356.31, 20.82) * mm, "end": v(-356.14, 20.87) * mm});
            skLineSegment(sketch, "E912", {"start": v(-356.14, 20.87) * mm, "end": v(-355.94, 20.9) * mm});
            skLineSegment(sketch, "E913", {"start": v(-355.94, 20.9) * mm, "end": v(-355.74, 20.92) * mm});
            skLineSegment(sketch, "E914", {"start": v(-355.74, 20.92) * mm, "end": v(-355.57, 20.9) * mm});
            skLineSegment(sketch, "E915", {"start": v(-355.57, 20.9) * mm, "end": v(-355.37, 20.87) * mm});
            skLineSegment(sketch, "E916", {"start": v(-355.37, 20.87) * mm, "end": v(-355.2, 20.82) * mm});
            skLineSegment(sketch, "E917", {"start": v(-355.2, 20.82) * mm, "end": v(-355.02, 20.77) * mm});
            skLineSegment(sketch, "E918", {"start": v(-355.02, 20.77) * mm, "end": v(-354.85, 20.7) * mm});
            skLineSegment(sketch, "E919", {"start": v(-354.85, 20.7) * mm, "end": v(-354.68, 20.6) * mm});
            skLineSegment(sketch, "E920", {"start": v(-354.68, 20.6) * mm, "end": v(-354.53, 20.47) * mm});
            skLineSegment(sketch, "E921", {"start": v(-354.53, 20.47) * mm, "end": v(-354.38, 20.35) * mm});
            skLineSegment(sketch, "E922", {"start": v(-354.38, 20.35) * mm, "end": v(-354.25, 20.2) * mm});
            skLineSegment(sketch, "E923", {"start": v(-354.25, 20.2) * mm, "end": v(-354.13, 20.05) * mm});
            skLineSegment(sketch, "E924", {"start": v(-354.13, 20.05) * mm, "end": v(-354.03, 19.88) * mm});
            skLineSegment(sketch, "E925", {"start": v(-354.03, 19.88) * mm, "end": v(-353.96, 19.7) * mm});
            skLineSegment(sketch, "E926", {"start": v(-353.96, 19.7) * mm, "end": v(-353.9, 19.53) * mm});
            skLineSegment(sketch, "E927", {"start": v(-353.9, 19.53) * mm, "end": v(-353.86, 19.36) * mm});
            skLineSegment(sketch, "E928", {"start": v(-353.86, 19.36) * mm, "end": v(-353.83, 19.16) * mm});
            skLineSegment(sketch, "E929", {"start": v(-353.83, 19.16) * mm, "end": v(-353.8, 18.98) * mm});
            skLineSegment(sketch, "E930", {"start": v(-353.8, 18.98) * mm, "end": v(-353.8, -1.36) * mm});
            skLineSegment(sketch, "E931", {"start": v(-353.8, -1.36) * mm, "end": v(-353.83, -1.53) * mm});
            skLineSegment(sketch, "E932", {"start": v(-353.83, -1.53) * mm, "end": v(-353.86, -1.73) * mm});
            skLineSegment(sketch, "E933", {"start": v(-353.86, -1.73) * mm, "end": v(-353.9, -1.9) * mm});
            skLineSegment(sketch, "E934", {"start": v(-353.9, -1.9) * mm, "end": v(-353.96, -2.08) * mm});
            skLineSegment(sketch, "E935", {"start": v(-353.96, -2.08) * mm, "end": v(-354.03, -2.25) * mm});
            skLineSegment(sketch, "E936", {"start": v(-354.03, -2.25) * mm, "end": v(-354.13, -2.42) * mm});
            skLineSegment(sketch, "E937", {"start": v(-354.13, -2.42) * mm, "end": v(-354.25, -2.57) * mm});
            skLineSegment(sketch, "E938", {"start": v(-354.25, -2.57) * mm, "end": v(-354.38, -2.72) * mm});
            skLineSegment(sketch, "E939", {"start": v(-354.38, -2.72) * mm, "end": v(-354.53, -2.84) * mm});
            skLineSegment(sketch, "E940", {"start": v(-354.53, -2.84) * mm, "end": v(-354.68, -2.97) * mm});
            skLineSegment(sketch, "E941", {"start": v(-354.68, -2.97) * mm, "end": v(-354.85, -3.07) * mm});
            skLineSegment(sketch, "E942", {"start": v(-354.85, -3.07) * mm, "end": v(-355.02, -3.14) * mm});
            skLineSegment(sketch, "E943", {"start": v(-355.02, -3.14) * mm, "end": v(-355.2, -3.2) * mm});
            skLineSegment(sketch, "E944", {"start": v(-355.2, -3.2) * mm, "end": v(-355.37, -3.24) * mm});
            skLineSegment(sketch, "E945", {"start": v(-355.37, -3.24) * mm, "end": v(-355.57, -3.27) * mm});
            skLineSegment(sketch, "E946", {"start": v(-355.57, -3.27) * mm, "end": v(-355.74, -3.3) * mm});
            skLineSegment(sketch, "E947", {"start": v(-355.74, -3.3) * mm, "end": v(-361.08, -3.3) * mm});
            skLineSegment(sketch, "E948", {"start": v(-361.08, -3.3) * mm, "end": v(-361.82, -3.24) * mm});
            skLineSegment(sketch, "E949", {"start": v(-361.82, -3.24) * mm, "end": v(-362.51, -3.14) * mm});
            skLineSegment(sketch, "E950", {"start": v(-362.51, -3.14) * mm, "end": v(-363.2, -2.97) * mm});
            skLineSegment(sketch, "E951", {"start": v(-363.2, -2.97) * mm, "end": v(-363.85, -2.74) * mm});
            skLineSegment(sketch, "E952", {"start": v(-363.85, -2.74) * mm, "end": v(-364.47, -2.45) * mm});
            skLineSegment(sketch, "E953", {"start": v(-364.47, -2.45) * mm, "end": v(-365.1, -2.08) * mm});
            skLineSegment(sketch, "E954", {"start": v(-365.1, -2.08) * mm, "end": v(-365.66, -1.65) * mm});
            skLineSegment(sketch, "E955", {"start": v(-365.66, -1.65) * mm, "end": v(-366.21, -1.16) * mm});
            skLineSegment(sketch, "E956", {"start": v(-366.21, -1.16) * mm, "end": v(-366.7, -0.61) * mm});
            skLineSegment(sketch, "E957", {"start": v(-366.7, -0.61) * mm, "end": v(-367.13, -0.04) * mm});
            skLineSegment(sketch, "E958", {"start": v(-367.13, -0.04) * mm, "end": v(-367.5, 0.58) * mm});
            skLineSegment(sketch, "E959", {"start": v(-367.5, 0.58) * mm, "end": v(-367.8, 1.2) * mm});
            skLineSegment(sketch, "E960", {"start": v(-367.8, 1.2) * mm, "end": v(-368.02, 1.84) * mm});
            skLineSegment(sketch, "E961", {"start": v(-368.02, 1.84) * mm, "end": v(-368.2, 2.54) * mm});
            skLineSegment(sketch, "E962", {"start": v(-368.2, 2.54) * mm, "end": v(-368.3, 3.23) * mm});
            skLineSegment(sketch, "E963", {"start": v(-347.01, -1.73) * mm, "end": v(-347.04, -1.53) * mm});
            skLineSegment(sketch, "E964", {"start": v(-347.04, -1.53) * mm, "end": v(-347.04, -1.36) * mm});
            skLineSegment(sketch, "E965", {"start": v(-347.04, -1.36) * mm, "end": v(-347.04, 18.98) * mm});
            skLineSegment(sketch, "E966", {"start": v(-347.04, 18.98) * mm, "end": v(-347.04, 19.16) * mm});
            skLineSegment(sketch, "E967", {"start": v(-347.04, 19.16) * mm, "end": v(-347.01, 19.36) * mm});
            skLineSegment(sketch, "E968", {"start": v(-347.01, 19.36) * mm, "end": v(-346.96, 19.53) * mm});
            skLineSegment(sketch, "E969", {"start": v(-346.96, 19.53) * mm, "end": v(-346.89, 19.7) * mm});
            skLineSegment(sketch, "E970", {"start": v(-346.89, 19.7) * mm, "end": v(-346.81, 19.88) * mm});
            skLineSegment(sketch, "E971", {"start": v(-346.81, 19.88) * mm, "end": v(-346.71, 20.05) * mm});
            skLineSegment(sketch, "E972", {"start": v(-346.71, 20.05) * mm, "end": v(-346.59, 20.2) * mm});
            skLineSegment(sketch, "E973", {"start": v(-346.59, 20.2) * mm, "end": v(-346.47, 20.35) * mm});
            skLineSegment(sketch, "E974", {"start": v(-346.47, 20.35) * mm, "end": v(-346.32, 20.47) * mm});
            skLineSegment(sketch, "E975", {"start": v(-346.32, 20.47) * mm, "end": v(-346.17, 20.6) * mm});
            skLineSegment(sketch, "E976", {"start": v(-346.17, 20.6) * mm, "end": v(-346.02, 20.7) * mm});
            skLineSegment(sketch, "E977", {"start": v(-346.02, 20.7) * mm, "end": v(-345.85, 20.77) * mm});
            skLineSegment(sketch, "E978", {"start": v(-345.85, 20.77) * mm, "end": v(-345.67, 20.82) * mm});
            skLineSegment(sketch, "E979", {"start": v(-345.67, 20.82) * mm, "end": v(-345.5, 20.87) * mm});
            skLineSegment(sketch, "E980", {"start": v(-345.5, 20.87) * mm, "end": v(-345.3, 20.9) * mm});
            skLineSegment(sketch, "E981", {"start": v(-345.3, 20.9) * mm, "end": v(-345.1, 20.92) * mm});
            skLineSegment(sketch, "E982", {"start": v(-345.1, 20.92) * mm, "end": v(-331.06, 20.92) * mm});
            skLineSegment(sketch, "E983", {"start": v(-331.06, 20.92) * mm, "end": v(-330.34, 20.87) * mm});
            skLineSegment(sketch, "E984", {"start": v(-330.34, 20.87) * mm, "end": v(-329.62, 20.77) * mm});
            skLineSegment(sketch, "E985", {"start": v(-329.62, 20.77) * mm, "end": v(-328.95, 20.6) * mm});
            skLineSegment(sketch, "E986", {"start": v(-328.95, 20.6) * mm, "end": v(-328.28, 20.37) * mm});
            skLineSegment(sketch, "E987", {"start": v(-328.28, 20.37) * mm, "end": v(-327.66, 20.08) * mm});
            skLineSegment(sketch, "E988", {"start": v(-327.66, 20.08) * mm, "end": v(-327.07, 19.7) * mm});
            skLineSegment(sketch, "E989", {"start": v(-327.07, 19.7) * mm, "end": v(-326.5, 19.28) * mm});
            skLineSegment(sketch, "E990", {"start": v(-326.5, 19.28) * mm, "end": v(-325.95, 18.79) * mm});
            skLineSegment(sketch, "E991", {"start": v(-325.95, 18.79) * mm, "end": v(-325.46, 18.24) * mm});
            skLineSegment(sketch, "E992", {"start": v(-325.46, 18.24) * mm, "end": v(-325, 17.67) * mm});
            skLineSegment(sketch, "E993", {"start": v(-325, 17.67) * mm, "end": v(-324.66, 17.05) * mm});
            skLineSegment(sketch, "E994", {"start": v(-324.66, 17.05) * mm, "end": v(-324.34, 16.43) * mm});
            skLineSegment(sketch, "E995", {"start": v(-324.34, 16.43) * mm, "end": v(-324.12, 15.78) * mm});
            skLineSegment(sketch, "E996", {"start": v(-324.12, 15.78) * mm, "end": v(-323.94, 15.09) * mm});
            skLineSegment(sketch, "E997", {"start": v(-323.94, 15.09) * mm, "end": v(-323.84, 14.4) * mm});
            skLineSegment(sketch, "E998", {"start": v(-323.84, 14.4) * mm, "end": v(-323.82, 13.65) * mm});
            skLineSegment(sketch, "E999", {"start": v(-323.82, 13.65) * mm, "end": v(-323.82, -1.36) * mm});
            skLineSegment(sketch, "E1000", {"start": v(-323.82, -1.36) * mm, "end": v(-323.82, -1.53) * mm});
            skLineSegment(sketch, "E1001", {"start": v(-323.82, -1.53) * mm, "end": v(-323.84, -1.73) * mm});
            skLineSegment(sketch, "E1002", {"start": v(-323.84, -1.73) * mm, "end": v(-323.9, -1.9) * mm});
            skLineSegment(sketch, "E1003", {"start": v(-323.9, -1.9) * mm, "end": v(-323.97, -2.08) * mm});
            skLineSegment(sketch, "E1004", {"start": v(-323.97, -2.08) * mm, "end": v(-324.04, -2.25) * mm});
            skLineSegment(sketch, "E1005", {"start": v(-324.04, -2.25) * mm, "end": v(-324.14, -2.42) * mm});
            skLineSegment(sketch, "E1006", {"start": v(-324.14, -2.42) * mm, "end": v(-324.27, -2.57) * mm});
            skLineSegment(sketch, "E1007", {"start": v(-324.27, -2.57) * mm, "end": v(-324.39, -2.72) * mm});
            skLineSegment(sketch, "E1008", {"start": v(-324.39, -2.72) * mm, "end": v(-324.54, -2.84) * mm});
            skLineSegment(sketch, "E1009", {"start": v(-324.54, -2.84) * mm, "end": v(-324.69, -2.97) * mm});
            skLineSegment(sketch, "E1010", {"start": v(-324.69, -2.97) * mm, "end": v(-324.84, -3.07) * mm});
            skLineSegment(sketch, "E1011", {"start": v(-324.84, -3.07) * mm, "end": v(-325, -3.14) * mm});
            skLineSegment(sketch, "E1012", {"start": v(-325, -3.14) * mm, "end": v(-325.18, -3.2) * mm});
            skLineSegment(sketch, "E1013", {"start": v(-325.18, -3.2) * mm, "end": v(-325.36, -3.24) * mm});
            skLineSegment(sketch, "E1014", {"start": v(-325.36, -3.24) * mm, "end": v(-325.56, -3.27) * mm});
            skLineSegment(sketch, "E1015", {"start": v(-325.56, -3.27) * mm, "end": v(-325.75, -3.3) * mm});
            skLineSegment(sketch, "E1016", {"start": v(-325.75, -3.3) * mm, "end": v(-325.95, -3.27) * mm});
            skLineSegment(sketch, "E1017", {"start": v(-325.95, -3.27) * mm, "end": v(-326.15, -3.24) * mm});
            skLineSegment(sketch, "E1018", {"start": v(-326.15, -3.24) * mm, "end": v(-326.32, -3.2) * mm});
            skLineSegment(sketch, "E1019", {"start": v(-326.32, -3.2) * mm, "end": v(-326.5, -3.14) * mm});
            skLineSegment(sketch, "E1020", {"start": v(-326.5, -3.14) * mm, "end": v(-326.67, -3.07) * mm});
            skLineSegment(sketch, "E1021", {"start": v(-326.67, -3.07) * mm, "end": v(-326.82, -2.97) * mm});
            skLineSegment(sketch, "E1022", {"start": v(-326.82, -2.97) * mm, "end": v(-326.97, -2.84) * mm});
            skLineSegment(sketch, "E1023", {"start": v(-326.97, -2.84) * mm, "end": v(-327.12, -2.72) * mm});
            skLineSegment(sketch, "E1024", {"start": v(-327.12, -2.72) * mm, "end": v(-327.24, -2.57) * mm});
            skLineSegment(sketch, "E1025", {"start": v(-327.24, -2.57) * mm, "end": v(-327.37, -2.42) * mm});
            skLineSegment(sketch, "E1026", {"start": v(-327.37, -2.42) * mm, "end": v(-327.47, -2.25) * mm});
            skLineSegment(sketch, "E1027", {"start": v(-327.47, -2.25) * mm, "end": v(-327.54, -2.08) * mm});
            skLineSegment(sketch, "E1028", {"start": v(-327.54, -2.08) * mm, "end": v(-327.61, -1.9) * mm});
            skLineSegment(sketch, "E1029", {"start": v(-327.61, -1.9) * mm, "end": v(-327.66, -1.73) * mm});
            skLineSegment(sketch, "E1030", {"start": v(-327.66, -1.73) * mm, "end": v(-327.69, -1.53) * mm});
            skLineSegment(sketch, "E1031", {"start": v(-327.69, -1.53) * mm, "end": v(-327.69, -1.36) * mm});
            skLineSegment(sketch, "E1032", {"start": v(-327.69, -1.36) * mm, "end": v(-327.69, 13.65) * mm});
            skLineSegment(sketch, "E1033", {"start": v(-327.69, 13.65) * mm, "end": v(-327.71, 14) * mm});
            skLineSegment(sketch, "E1034", {"start": v(-327.71, 14) * mm, "end": v(-327.74, 14.32) * mm});
            skLineSegment(sketch, "E1035", {"start": v(-327.74, 14.32) * mm, "end": v(-327.84, 14.64) * mm});
            skLineSegment(sketch, "E1036", {"start": v(-327.84, 14.64) * mm, "end": v(-327.94, 14.94) * mm});
            skLineSegment(sketch, "E1037", {"start": v(-327.94, 14.94) * mm, "end": v(-328.09, 15.24) * mm});
            skLineSegment(sketch, "E1038", {"start": v(-328.09, 15.24) * mm, "end": v(-328.23, 15.51) * mm});
            skLineSegment(sketch, "E1039", {"start": v(-328.23, 15.51) * mm, "end": v(-328.46, 15.78) * mm});
            skLineSegment(sketch, "E1040", {"start": v(-328.46, 15.78) * mm, "end": v(-328.68, 16.06) * mm});
            skLineSegment(sketch, "E1041", {"start": v(-328.68, 16.06) * mm, "end": v(-328.93, 16.28) * mm});
            skLineSegment(sketch, "E1042", {"start": v(-328.93, 16.28) * mm, "end": v(-329.2, 16.48) * mm});
            skLineSegment(sketch, "E1043", {"start": v(-329.2, 16.48) * mm, "end": v(-329.47, 16.65) * mm});
            skLineSegment(sketch, "E1044", {"start": v(-329.47, 16.65) * mm, "end": v(-329.77, 16.8) * mm});
            skLineSegment(sketch, "E1045", {"start": v(-329.77, 16.8) * mm, "end": v(-330.07, 16.9) * mm});
            skLineSegment(sketch, "E1046", {"start": v(-330.07, 16.9) * mm, "end": v(-330.4, 16.97) * mm});
            skLineSegment(sketch, "E1047", {"start": v(-330.4, 16.97) * mm, "end": v(-330.74, 17.02) * mm});
            skLineSegment(sketch, "E1048", {"start": v(-330.74, 17.02) * mm, "end": v(-331.06, 17.05) * mm});
            skLineSegment(sketch, "E1049", {"start": v(-331.06, 17.05) * mm, "end": v(-333.5, 17.05) * mm});
            skLineSegment(sketch, "E1050", {"start": v(-333.5, 17.05) * mm, "end": v(-333.5, -1.36) * mm});
            skLineSegment(sketch, "E1051", {"start": v(-333.5, -1.36) * mm, "end": v(-333.5, -1.53) * mm});
            skLineSegment(sketch, "E1052", {"start": v(-333.5, -1.53) * mm, "end": v(-333.52, -1.73) * mm});
            skLineSegment(sketch, "E1053", {"start": v(-333.52, -1.73) * mm, "end": v(-333.57, -1.9) * mm});
            skLineSegment(sketch, "E1054", {"start": v(-333.57, -1.9) * mm, "end": v(-333.64, -2.08) * mm});
            skLineSegment(sketch, "E1055", {"start": v(-333.64, -2.08) * mm, "end": v(-333.72, -2.25) * mm});
            skLineSegment(sketch, "E1056", {"start": v(-333.72, -2.25) * mm, "end": v(-333.82, -2.42) * mm});
            skLineSegment(sketch, "E1057", {"start": v(-333.82, -2.42) * mm, "end": v(-333.94, -2.57) * mm});
            skLineSegment(sketch, "E1058", {"start": v(-333.94, -2.57) * mm, "end": v(-334.06, -2.72) * mm});
            skLineSegment(sketch, "E1059", {"start": v(-334.06, -2.72) * mm, "end": v(-334.21, -2.84) * mm});
            skLineSegment(sketch, "E1060", {"start": v(-334.21, -2.84) * mm, "end": v(-334.36, -2.97) * mm});
            skLineSegment(sketch, "E1061", {"start": v(-334.36, -2.97) * mm, "end": v(-334.5, -3.07) * mm});
            skLineSegment(sketch, "E1062", {"start": v(-334.5, -3.07) * mm, "end": v(-334.68, -3.14) * mm});
            skLineSegment(sketch, "E1063", {"start": v(-334.68, -3.14) * mm, "end": v(-334.86, -3.2) * mm});
            skLineSegment(sketch, "E1064", {"start": v(-334.86, -3.2) * mm, "end": v(-335.03, -3.24) * mm});
            skLineSegment(sketch, "E1065", {"start": v(-335.03, -3.24) * mm, "end": v(-335.23, -3.27) * mm});
            skLineSegment(sketch, "E1066", {"start": v(-335.23, -3.27) * mm, "end": v(-335.43, -3.3) * mm});
            skLineSegment(sketch, "E1067", {"start": v(-335.43, -3.3) * mm, "end": v(-335.63, -3.27) * mm});
            skLineSegment(sketch, "E1068", {"start": v(-335.63, -3.27) * mm, "end": v(-335.82, -3.24) * mm});
            skLineSegment(sketch, "E1069", {"start": v(-335.82, -3.24) * mm, "end": v(-336, -3.2) * mm});
            skLineSegment(sketch, "E1070", {"start": v(-336, -3.2) * mm, "end": v(-336.17, -3.14) * mm});
            skLineSegment(sketch, "E1071", {"start": v(-336.17, -3.14) * mm, "end": v(-336.35, -3.07) * mm});
            skLineSegment(sketch, "E1072", {"start": v(-336.35, -3.07) * mm, "end": v(-336.5, -2.97) * mm});
            skLineSegment(sketch, "E1073", {"start": v(-336.5, -2.97) * mm, "end": v(-336.64, -2.84) * mm});
            skLineSegment(sketch, "E1074", {"start": v(-336.64, -2.84) * mm, "end": v(-336.8, -2.72) * mm});
            skLineSegment(sketch, "E1075", {"start": v(-336.8, -2.72) * mm, "end": v(-336.92, -2.57) * mm});
            skLineSegment(sketch, "E1076", {"start": v(-336.92, -2.57) * mm, "end": v(-337.04, -2.42) * mm});
            skLineSegment(sketch, "E1077", {"start": v(-337.04, -2.42) * mm, "end": v(-337.14, -2.25) * mm});
            skLineSegment(sketch, "E1078", {"start": v(-337.14, -2.25) * mm, "end": v(-337.21, -2.08) * mm});
            skLineSegment(sketch, "E1079", {"start": v(-337.21, -2.08) * mm, "end": v(-337.29, -1.9) * mm});
            skLineSegment(sketch, "E1080", {"start": v(-337.29, -1.9) * mm, "end": v(-337.34, -1.73) * mm});
            skLineSegment(sketch, "E1081", {"start": v(-337.34, -1.73) * mm, "end": v(-337.36, -1.53) * mm});
            skLineSegment(sketch, "E1082", {"start": v(-337.36, -1.53) * mm, "end": v(-337.36, -1.36) * mm});
            skLineSegment(sketch, "E1083", {"start": v(-337.36, -1.36) * mm, "end": v(-337.36, 17.05) * mm});
            skLineSegment(sketch, "E1084", {"start": v(-337.36, 17.05) * mm, "end": v(-343.17, 17.05) * mm});
            skLineSegment(sketch, "E1085", {"start": v(-343.17, 17.05) * mm, "end": v(-343.17, -1.36) * mm});
            skLineSegment(sketch, "E1086", {"start": v(-343.17, -1.36) * mm, "end": v(-343.17, -1.53) * mm});
            skLineSegment(sketch, "E1087", {"start": v(-343.17, -1.53) * mm, "end": v(-343.2, -1.73) * mm});
            skLineSegment(sketch, "E1088", {"start": v(-343.2, -1.73) * mm, "end": v(-343.24, -1.9) * mm});
            skLineSegment(sketch, "E1089", {"start": v(-343.24, -1.9) * mm, "end": v(-343.32, -2.08) * mm});
            skLineSegment(sketch, "E1090", {"start": v(-343.32, -2.08) * mm, "end": v(-343.4, -2.25) * mm});
            skLineSegment(sketch, "E1091", {"start": v(-343.4, -2.25) * mm, "end": v(-343.49, -2.42) * mm});
            skLineSegment(sketch, "E1092", {"start": v(-343.49, -2.42) * mm, "end": v(-343.61, -2.57) * mm});
            skLineSegment(sketch, "E1093", {"start": v(-343.61, -2.57) * mm, "end": v(-343.74, -2.72) * mm});
            skLineSegment(sketch, "E1094", {"start": v(-343.74, -2.72) * mm, "end": v(-343.89, -2.84) * mm});
            skLineSegment(sketch, "E1095", {"start": v(-343.89, -2.84) * mm, "end": v(-344.03, -2.97) * mm});
            skLineSegment(sketch, "E1096", {"start": v(-344.03, -2.97) * mm, "end": v(-344.18, -3.07) * mm});
            skLineSegment(sketch, "E1097", {"start": v(-344.18, -3.07) * mm, "end": v(-344.36, -3.14) * mm});
            skLineSegment(sketch, "E1098", {"start": v(-344.36, -3.14) * mm, "end": v(-344.53, -3.2) * mm});
            skLineSegment(sketch, "E1099", {"start": v(-344.53, -3.2) * mm, "end": v(-344.7, -3.24) * mm});
            skLineSegment(sketch, "E1100", {"start": v(-344.7, -3.24) * mm, "end": v(-344.9, -3.27) * mm});
            skLineSegment(sketch, "E1101", {"start": v(-344.9, -3.27) * mm, "end": v(-345.1, -3.3) * mm});
            skLineSegment(sketch, "E1102", {"start": v(-345.1, -3.3) * mm, "end": v(-345.3, -3.27) * mm});
            skLineSegment(sketch, "E1103", {"start": v(-345.3, -3.27) * mm, "end": v(-345.5, -3.24) * mm});
            skLineSegment(sketch, "E1104", {"start": v(-345.5, -3.24) * mm, "end": v(-345.67, -3.2) * mm});
            skLineSegment(sketch, "E1105", {"start": v(-345.67, -3.2) * mm, "end": v(-345.85, -3.14) * mm});
            skLineSegment(sketch, "E1106", {"start": v(-345.85, -3.14) * mm, "end": v(-346.02, -3.07) * mm});
            skLineSegment(sketch, "E1107", {"start": v(-346.02, -3.07) * mm, "end": v(-346.17, -2.97) * mm});
            skLineSegment(sketch, "E1108", {"start": v(-346.17, -2.97) * mm, "end": v(-346.32, -2.84) * mm});
            skLineSegment(sketch, "E1109", {"start": v(-346.32, -2.84) * mm, "end": v(-346.47, -2.72) * mm});
            skLineSegment(sketch, "E1110", {"start": v(-346.47, -2.72) * mm, "end": v(-346.59, -2.57) * mm});
            skLineSegment(sketch, "E1111", {"start": v(-346.59, -2.57) * mm, "end": v(-346.71, -2.42) * mm});
            skLineSegment(sketch, "E1112", {"start": v(-346.71, -2.42) * mm, "end": v(-346.81, -2.25) * mm});
            skLineSegment(sketch, "E1113", {"start": v(-346.81, -2.25) * mm, "end": v(-346.89, -2.08) * mm});
            skLineSegment(sketch, "E1114", {"start": v(-346.89, -2.08) * mm, "end": v(-346.96, -1.9) * mm});
            skLineSegment(sketch, "E1115", {"start": v(-346.96, -1.9) * mm, "end": v(-347.01, -1.73) * mm});
            skLineSegment(sketch, "E1116", {"start": v(-307.8, -0.36) * mm, "end": v(-307.82, -0.19) * mm});
            skLineSegment(sketch, "E1117", {"start": v(-307.82, -0.19) * mm, "end": v(-307.8, 0) * mm});
            skLineSegment(sketch, "E1118", {"start": v(-307.8, 0) * mm, "end": v(-307.77, 0.2) * mm});
            skLineSegment(sketch, "E1119", {"start": v(-307.77, 0.2) * mm, "end": v(-307.72, 0.38) * mm});
            skLineSegment(sketch, "E1120", {"start": v(-307.72, 0.38) * mm, "end": v(-307.67, 0.55) * mm});
            skLineSegment(sketch, "E1121", {"start": v(-307.67, 0.55) * mm, "end": v(-307.6, 0.73) * mm});
            skLineSegment(sketch, "E1122", {"start": v(-307.6, 0.73) * mm, "end": v(-307.5, 0.88) * mm});
            skLineSegment(sketch, "E1123", {"start": v(-307.5, 0.88) * mm, "end": v(-307.37, 1.05) * mm});
            skLineSegment(sketch, "E1124", {"start": v(-307.37, 1.05) * mm, "end": v(-307.25, 1.17) * mm});
            skLineSegment(sketch, "E1125", {"start": v(-307.25, 1.17) * mm, "end": v(-307.1, 1.32) * mm});
            skLineSegment(sketch, "E1126", {"start": v(-307.1, 1.32) * mm, "end": v(-306.95, 1.42) * mm});
            skLineSegment(sketch, "E1127", {"start": v(-306.95, 1.42) * mm, "end": v(-306.78, 1.52) * mm});
            skLineSegment(sketch, "E1128", {"start": v(-306.78, 1.52) * mm, "end": v(-306.6, 1.62) * mm});
            skLineSegment(sketch, "E1129", {"start": v(-306.6, 1.62) * mm, "end": v(-306.43, 1.67) * mm});
            skLineSegment(sketch, "E1130", {"start": v(-306.43, 1.67) * mm, "end": v(-306.26, 1.72) * mm});
            skLineSegment(sketch, "E1131", {"start": v(-306.26, 1.72) * mm, "end": v(-306.06, 1.74) * mm});
            skLineSegment(sketch, "E1132", {"start": v(-306.06, 1.74) * mm, "end": v(-305.89, 1.74) * mm});
            skLineSegment(sketch, "E1133", {"start": v(-305.89, 1.74) * mm, "end": v(-305.69, 1.74) * mm});
            skLineSegment(sketch, "E1134", {"start": v(-305.69, 1.74) * mm, "end": v(-305.49, 1.72) * mm});
            skLineSegment(sketch, "E1135", {"start": v(-305.49, 1.72) * mm, "end": v(-305.31, 1.67) * mm});
            skLineSegment(sketch, "E1136", {"start": v(-305.31, 1.67) * mm, "end": v(-305.14, 1.62) * mm});
            skLineSegment(sketch, "E1137", {"start": v(-305.14, 1.62) * mm, "end": v(-304.97, 1.55) * mm});
            skLineSegment(sketch, "E1138", {"start": v(-304.97, 1.55) * mm, "end": v(-304.8, 1.45) * mm});
            skLineSegment(sketch, "E1139", {"start": v(-304.8, 1.45) * mm, "end": v(-304.65, 1.32) * mm});
            skLineSegment(sketch, "E1140", {"start": v(-304.65, 1.32) * mm, "end": v(-304.5, 1.2) * mm});
            skLineSegment(sketch, "E1141", {"start": v(-304.5, 1.2) * mm, "end": v(-304.22, 0.95) * mm});
            skLineSegment(sketch, "E1142", {"start": v(-304.22, 0.95) * mm, "end": v(-303.95, 0.73) * mm});
            skLineSegment(sketch, "E1143", {"start": v(-303.95, 0.73) * mm, "end": v(-303.65, 0.55) * mm});
            skLineSegment(sketch, "E1144", {"start": v(-303.65, 0.55) * mm, "end": v(-303.36, 0.4) * mm});
            skLineSegment(sketch, "E1145", {"start": v(-303.36, 0.4) * mm, "end": v(-303.03, 0.28) * mm});
            skLineSegment(sketch, "E1146", {"start": v(-303.03, 0.28) * mm, "end": v(-302.71, 0.2) * mm});
            skLineSegment(sketch, "E1147", {"start": v(-302.71, 0.2) * mm, "end": v(-302.36, 0.16) * mm});
            skLineSegment(sketch, "E1148", {"start": v(-302.36, 0.16) * mm, "end": v(-302.04, 0.13) * mm});
            skLineSegment(sketch, "E1149", {"start": v(-302.04, 0.13) * mm, "end": v(-301.67, 0.16) * mm});
            skLineSegment(sketch, "E1150", {"start": v(-301.67, 0.16) * mm, "end": v(-301.35, 0.18) * mm});
            skLineSegment(sketch, "E1151", {"start": v(-301.35, 0.18) * mm, "end": v(-301.02, 0.28) * mm});
            skLineSegment(sketch, "E1152", {"start": v(-301.02, 0.28) * mm, "end": v(-300.73, 0.38) * mm});
            skLineSegment(sketch, "E1153", {"start": v(-300.73, 0.38) * mm, "end": v(-300.43, 0.53) * mm});
            skLineSegment(sketch, "E1154", {"start": v(-300.43, 0.53) * mm, "end": v(-300.13, 0.68) * mm});
            skLineSegment(sketch, "E1155", {"start": v(-300.13, 0.68) * mm, "end": v(-299.88, 0.9) * mm});
            skLineSegment(sketch, "E1156", {"start": v(-299.88, 0.9) * mm, "end": v(-299.63, 1.12) * mm});
            skLineSegment(sketch, "E1157", {"start": v(-299.63, 1.12) * mm, "end": v(-299.39, 1.37) * mm});
            skLineSegment(sketch, "E1158", {"start": v(-299.39, 1.37) * mm, "end": v(-299.19, 1.65) * mm});
            skLineSegment(sketch, "E1159", {"start": v(-299.19, 1.65) * mm, "end": v(-299.01, 1.92) * mm});
            skLineSegment(sketch, "E1160", {"start": v(-299.01, 1.92) * mm, "end": v(-298.9, 2.22) * mm});
            skLineSegment(sketch, "E1161", {"start": v(-298.9, 2.22) * mm, "end": v(-298.8, 2.51) * mm});
            skLineSegment(sketch, "E1162", {"start": v(-298.8, 2.51) * mm, "end": v(-298.7, 2.84) * mm});
            skLineSegment(sketch, "E1163", {"start": v(-298.7, 2.84) * mm, "end": v(-298.67, 3.16) * mm});
            skLineSegment(sketch, "E1164", {"start": v(-298.67, 3.16) * mm, "end": v(-298.64, 3.5) * mm});
            skLineSegment(sketch, "E1165", {"start": v(-298.64, 3.5) * mm, "end": v(-298.64, 8.84) * mm});
            skLineSegment(sketch, "E1166", {"start": v(-298.64, 8.84) * mm, "end": v(-298.64, 9.09) * mm});
            skLineSegment(sketch, "E1167", {"start": v(-298.64, 9.09) * mm, "end": v(-298.7, 9.34) * mm});
            skLineSegment(sketch, "E1168", {"start": v(-298.7, 9.34) * mm, "end": v(-298.74, 9.56) * mm});
            skLineSegment(sketch, "E1169", {"start": v(-298.74, 9.56) * mm, "end": v(-298.82, 9.78) * mm});
            skLineSegment(sketch, "E1170", {"start": v(-298.82, 9.78) * mm, "end": v(-298.92, 9.98) * mm});
            skLineSegment(sketch, "E1171", {"start": v(-298.92, 9.98) * mm, "end": v(-299.04, 10.18) * mm});
            skLineSegment(sketch, "E1172", {"start": v(-299.04, 10.18) * mm, "end": v(-299.16, 10.38) * mm});
            skLineSegment(sketch, "E1173", {"start": v(-299.16, 10.38) * mm, "end": v(-299.34, 10.55) * mm});
            skLineSegment(sketch, "E1174", {"start": v(-299.34, 10.55) * mm, "end": v(-299.51, 10.72) * mm});
            skLineSegment(sketch, "E1175", {"start": v(-299.51, 10.72) * mm, "end": v(-299.7, 10.87) * mm});
            skLineSegment(sketch, "E1176", {"start": v(-299.7, 10.87) * mm, "end": v(-299.9, 10.97) * mm});
            skLineSegment(sketch, "E1177", {"start": v(-299.9, 10.97) * mm, "end": v(-300.1, 11.07) * mm});
            skLineSegment(sketch, "E1178", {"start": v(-300.1, 11.07) * mm, "end": v(-300.33, 11.15) * mm});
            skLineSegment(sketch, "E1179", {"start": v(-300.33, 11.15) * mm, "end": v(-300.55, 11.22) * mm});
            skLineSegment(sketch, "E1180", {"start": v(-300.55, 11.22) * mm, "end": v(-300.8, 11.25) * mm});
            skLineSegment(sketch, "E1181", {"start": v(-300.8, 11.25) * mm, "end": v(-301.05, 11.25) * mm});
            skLineSegment(sketch, "E1182", {"start": v(-301.05, 11.25) * mm, "end": v(-301.07, 11.25) * mm});
            skLineSegment(sketch, "E1183", {"start": v(-301.07, 11.25) * mm, "end": v(-301.25, 11.27) * mm});
            skLineSegment(sketch, "E1184", {"start": v(-301.25, 11.27) * mm, "end": v(-301.45, 11.3) * mm});
            skLineSegment(sketch, "E1185", {"start": v(-301.45, 11.3) * mm, "end": v(-301.62, 11.34) * mm});
            skLineSegment(sketch, "E1186", {"start": v(-301.62, 11.34) * mm, "end": v(-301.8, 11.4) * mm});
            skLineSegment(sketch, "E1187", {"start": v(-301.8, 11.4) * mm, "end": v(-301.97, 11.5) * mm});
            skLineSegment(sketch, "E1188", {"start": v(-301.97, 11.5) * mm, "end": v(-302.14, 11.6) * mm});
            skLineSegment(sketch, "E1189", {"start": v(-302.14, 11.6) * mm, "end": v(-302.29, 11.7) * mm});
            skLineSegment(sketch, "E1190", {"start": v(-302.29, 11.7) * mm, "end": v(-302.44, 11.84) * mm});
            skLineSegment(sketch, "E1191", {"start": v(-302.44, 11.84) * mm, "end": v(-302.56, 11.99) * mm});
            skLineSegment(sketch, "E1192", {"start": v(-302.56, 11.99) * mm, "end": v(-302.69, 12.14) * mm});
            skLineSegment(sketch, "E1193", {"start": v(-302.69, 12.14) * mm, "end": v(-302.78, 12.31) * mm});
            skLineSegment(sketch, "E1194", {"start": v(-302.78, 12.31) * mm, "end": v(-302.86, 12.46) * mm});
            skLineSegment(sketch, "E1195", {"start": v(-302.86, 12.46) * mm, "end": v(-302.9, 12.63) * mm});
            skLineSegment(sketch, "E1196", {"start": v(-302.9, 12.63) * mm, "end": v(-302.96, 12.8) * mm});
            skLineSegment(sketch, "E1197", {"start": v(-302.96, 12.8) * mm, "end": v(-302.98, 13) * mm});
            skLineSegment(sketch, "E1198", {"start": v(-302.98, 13) * mm, "end": v(-303, 13.18) * mm});
            skLineSegment(sketch, "E1199", {"start": v(-303, 13.18) * mm, "end": v(-302.98, 13.38) * mm});
            skLineSegment(sketch, "E1200", {"start": v(-302.98, 13.38) * mm, "end": v(-302.96, 13.58) * mm});
            skLineSegment(sketch, "E1201", {"start": v(-302.96, 13.58) * mm, "end": v(-302.9, 13.75) * mm});
            skLineSegment(sketch, "E1202", {"start": v(-302.9, 13.75) * mm, "end": v(-302.86, 13.92) * mm});
            skLineSegment(sketch, "E1203", {"start": v(-302.86, 13.92) * mm, "end": v(-302.78, 14.1) * mm});
            skLineSegment(sketch, "E1204", {"start": v(-302.78, 14.1) * mm, "end": v(-302.69, 14.27) * mm});
            skLineSegment(sketch, "E1205", {"start": v(-302.69, 14.27) * mm, "end": v(-302.56, 14.42) * mm});
            skLineSegment(sketch, "E1206", {"start": v(-302.56, 14.42) * mm, "end": v(-302.44, 14.57) * mm});
            skLineSegment(sketch, "E1207", {"start": v(-302.44, 14.57) * mm, "end": v(-302.29, 14.7) * mm});
            skLineSegment(sketch, "E1208", {"start": v(-302.29, 14.7) * mm, "end": v(-302.14, 14.82) * mm});
            skLineSegment(sketch, "E1209", {"start": v(-302.14, 14.82) * mm, "end": v(-301.97, 14.92) * mm});
            skLineSegment(sketch, "E1210", {"start": v(-301.97, 14.92) * mm, "end": v(-301.8, 15) * mm});
            skLineSegment(sketch, "E1211", {"start": v(-301.8, 15) * mm, "end": v(-301.62, 15.04) * mm});
            skLineSegment(sketch, "E1212", {"start": v(-301.62, 15.04) * mm, "end": v(-301.45, 15.09) * mm});
            skLineSegment(sketch, "E1213", {"start": v(-301.45, 15.09) * mm, "end": v(-301.25, 15.11) * mm});
            skLineSegment(sketch, "E1214", {"start": v(-301.25, 15.11) * mm, "end": v(-301.07, 15.11) * mm});
            skLineSegment(sketch, "E1215", {"start": v(-301.07, 15.11) * mm, "end": v(-301.05, 15.11) * mm});
            skLineSegment(sketch, "E1216", {"start": v(-301.05, 15.11) * mm, "end": v(-300.8, 15.14) * mm});
            skLineSegment(sketch, "E1217", {"start": v(-300.8, 15.14) * mm, "end": v(-300.55, 15.16) * mm});
            skLineSegment(sketch, "E1218", {"start": v(-300.55, 15.16) * mm, "end": v(-300.33, 15.21) * mm});
            skLineSegment(sketch, "E1219", {"start": v(-300.33, 15.21) * mm, "end": v(-300.1, 15.31) * mm});
            skLineSegment(sketch, "E1220", {"start": v(-300.1, 15.31) * mm, "end": v(-299.9, 15.41) * mm});
            skLineSegment(sketch, "E1221", {"start": v(-299.9, 15.41) * mm, "end": v(-299.7, 15.51) * mm});
            skLineSegment(sketch, "E1222", {"start": v(-299.7, 15.51) * mm, "end": v(-299.51, 15.66) * mm});
            skLineSegment(sketch, "E1223", {"start": v(-299.51, 15.66) * mm, "end": v(-299.34, 15.83) * mm});
            skLineSegment(sketch, "E1224", {"start": v(-299.34, 15.83) * mm, "end": v(-299.16, 16) * mm});
            skLineSegment(sketch, "E1225", {"start": v(-299.16, 16) * mm, "end": v(-299.04, 16.2) * mm});
            skLineSegment(sketch, "E1226", {"start": v(-299.04, 16.2) * mm, "end": v(-298.92, 16.4) * mm});
            skLineSegment(sketch, "E1227", {"start": v(-298.92, 16.4) * mm, "end": v(-298.82, 16.6) * mm});
            skLineSegment(sketch, "E1228", {"start": v(-298.82, 16.6) * mm, "end": v(-298.74, 16.83) * mm});
            skLineSegment(sketch, "E1229", {"start": v(-298.74, 16.83) * mm, "end": v(-298.7, 17.05) * mm});
            skLineSegment(sketch, "E1230", {"start": v(-298.7, 17.05) * mm, "end": v(-298.64, 17.3) * mm});
            skLineSegment(sketch, "E1231", {"start": v(-298.64, 17.3) * mm, "end": v(-298.64, 17.55) * mm});
            skLineSegment(sketch, "E1232", {"start": v(-298.64, 17.55) * mm, "end": v(-298.64, 22.85) * mm});
            skLineSegment(sketch, "E1233", {"start": v(-298.64, 22.85) * mm, "end": v(-298.67, 23.2) * mm});
            skLineSegment(sketch, "E1234", {"start": v(-298.67, 23.2) * mm, "end": v(-298.7, 23.52) * mm});
            skLineSegment(sketch, "E1235", {"start": v(-298.7, 23.52) * mm, "end": v(-298.8, 23.85) * mm});
            skLineSegment(sketch, "E1236", {"start": v(-298.8, 23.85) * mm, "end": v(-298.9, 24.14) * mm});
            skLineSegment(sketch, "E1237", {"start": v(-298.9, 24.14) * mm, "end": v(-299.01, 24.44) * mm});
            skLineSegment(sketch, "E1238", {"start": v(-299.01, 24.44) * mm, "end": v(-299.19, 24.71) * mm});
            skLineSegment(sketch, "E1239", {"start": v(-299.19, 24.71) * mm, "end": v(-299.39, 24.99) * mm});
            skLineSegment(sketch, "E1240", {"start": v(-299.39, 24.99) * mm, "end": v(-299.63, 25.23) * mm});
            skLineSegment(sketch, "E1241", {"start": v(-299.63, 25.23) * mm, "end": v(-299.88, 25.46) * mm});
            skLineSegment(sketch, "E1242", {"start": v(-299.88, 25.46) * mm, "end": v(-300.13, 25.68) * mm});
            skLineSegment(sketch, "E1243", {"start": v(-300.13, 25.68) * mm, "end": v(-300.43, 25.83) * mm});
            skLineSegment(sketch, "E1244", {"start": v(-300.43, 25.83) * mm, "end": v(-300.73, 25.98) * mm});
            skLineSegment(sketch, "E1245", {"start": v(-300.73, 25.98) * mm, "end": v(-301.02, 26.08) * mm});
            skLineSegment(sketch, "E1246", {"start": v(-301.02, 26.08) * mm, "end": v(-301.35, 26.18) * mm});
            skLineSegment(sketch, "E1247", {"start": v(-301.35, 26.18) * mm, "end": v(-301.67, 26.2) * mm});
            skLineSegment(sketch, "E1248", {"start": v(-301.67, 26.2) * mm, "end": v(-302.04, 26.23) * mm});
            skLineSegment(sketch, "E1249", {"start": v(-302.04, 26.23) * mm, "end": v(-302.36, 26.2) * mm});
            skLineSegment(sketch, "E1250", {"start": v(-302.36, 26.2) * mm, "end": v(-302.71, 26.15) * mm});
            skLineSegment(sketch, "E1251", {"start": v(-302.71, 26.15) * mm, "end": v(-303.03, 26.08) * mm});
            skLineSegment(sketch, "E1252", {"start": v(-303.03, 26.08) * mm, "end": v(-303.33, 25.98) * mm});
            skLineSegment(sketch, "E1253", {"start": v(-303.33, 25.98) * mm, "end": v(-303.63, 25.83) * mm});
            skLineSegment(sketch, "E1254", {"start": v(-303.63, 25.83) * mm, "end": v(-303.93, 25.63) * mm});
            skLineSegment(sketch, "E1255", {"start": v(-303.93, 25.63) * mm, "end": v(-304.22, 25.43) * mm});
            skLineSegment(sketch, "E1256", {"start": v(-304.22, 25.43) * mm, "end": v(-304.5, 25.19) * mm});
            skLineSegment(sketch, "E1257", {"start": v(-304.5, 25.19) * mm, "end": v(-304.65, 25.06) * mm});
            skLineSegment(sketch, "E1258", {"start": v(-304.65, 25.06) * mm, "end": v(-304.8, 24.94) * mm});
            skLineSegment(sketch, "E1259", {"start": v(-304.8, 24.94) * mm, "end": v(-304.97, 24.84) * mm});
            skLineSegment(sketch, "E1260", {"start": v(-304.97, 24.84) * mm, "end": v(-305.14, 24.76) * mm});
            skLineSegment(sketch, "E1261", {"start": v(-305.14, 24.76) * mm, "end": v(-305.31, 24.69) * mm});
            skLineSegment(sketch, "E1262", {"start": v(-305.31, 24.69) * mm, "end": v(-305.49, 24.64) * mm});
            skLineSegment(sketch, "E1263", {"start": v(-305.49, 24.64) * mm, "end": v(-305.69, 24.61) * mm});
            skLineSegment(sketch, "E1264", {"start": v(-305.69, 24.61) * mm, "end": v(-305.89, 24.61) * mm});
            skLineSegment(sketch, "E1265", {"start": v(-305.89, 24.61) * mm, "end": v(-306.06, 24.61) * mm});
            skLineSegment(sketch, "E1266", {"start": v(-306.06, 24.61) * mm, "end": v(-306.26, 24.64) * mm});
            skLineSegment(sketch, "E1267", {"start": v(-306.26, 24.64) * mm, "end": v(-306.43, 24.69) * mm});
            skLineSegment(sketch, "E1268", {"start": v(-306.43, 24.69) * mm, "end": v(-306.6, 24.74) * mm});
            skLineSegment(sketch, "E1269", {"start": v(-306.6, 24.74) * mm, "end": v(-306.78, 24.84) * mm});
            skLineSegment(sketch, "E1270", {"start": v(-306.78, 24.84) * mm, "end": v(-306.95, 24.94) * mm});
            skLineSegment(sketch, "E1271", {"start": v(-306.95, 24.94) * mm, "end": v(-307.1, 25.04) * mm});
            skLineSegment(sketch, "E1272", {"start": v(-307.1, 25.04) * mm, "end": v(-307.25, 25.19) * mm});
            skLineSegment(sketch, "E1273", {"start": v(-307.25, 25.19) * mm, "end": v(-307.37, 25.3) * mm});
            skLineSegment(sketch, "E1274", {"start": v(-307.37, 25.3) * mm, "end": v(-307.5, 25.48) * mm});
            skLineSegment(sketch, "E1275", {"start": v(-307.5, 25.48) * mm, "end": v(-307.6, 25.63) * mm});
            skLineSegment(sketch, "E1276", {"start": v(-307.6, 25.63) * mm, "end": v(-307.67, 25.8) * mm});
            skLineSegment(sketch, "E1277", {"start": v(-307.67, 25.8) * mm, "end": v(-307.72, 25.98) * mm});
            skLineSegment(sketch, "E1278", {"start": v(-307.72, 25.98) * mm, "end": v(-307.77, 26.15) * mm});
            skLineSegment(sketch, "E1279", {"start": v(-307.77, 26.15) * mm, "end": v(-307.8, 26.35) * mm});
            skLineSegment(sketch, "E1280", {"start": v(-307.8, 26.35) * mm, "end": v(-307.82, 26.55) * mm});
            skLineSegment(sketch, "E1281", {"start": v(-307.82, 26.55) * mm, "end": v(-307.8, 26.72) * mm});
            skLineSegment(sketch, "E1282", {"start": v(-307.8, 26.72) * mm, "end": v(-307.77, 26.92) * mm});
            skLineSegment(sketch, "E1283", {"start": v(-307.77, 26.92) * mm, "end": v(-307.72, 27.1) * mm});
            skLineSegment(sketch, "E1284", {"start": v(-307.72, 27.1) * mm, "end": v(-307.67, 27.27) * mm});
            skLineSegment(sketch, "E1285", {"start": v(-307.67, 27.27) * mm, "end": v(-307.57, 27.44) * mm});
            skLineSegment(sketch, "E1286", {"start": v(-307.57, 27.44) * mm, "end": v(-307.47, 27.6) * mm});
            skLineSegment(sketch, "E1287", {"start": v(-307.47, 27.6) * mm, "end": v(-307.37, 27.74) * mm});
            skLineSegment(sketch, "E1288", {"start": v(-307.37, 27.74) * mm, "end": v(-307.22, 27.89) * mm});
            skLineSegment(sketch, "E1289", {"start": v(-307.22, 27.89) * mm, "end": v(-306.65, 28.4) * mm});
            skLineSegment(sketch, "E1290", {"start": v(-306.65, 28.4) * mm, "end": v(-306.08, 28.88) * mm});
            skLineSegment(sketch, "E1291", {"start": v(-306.08, 28.88) * mm, "end": v(-305.46, 29.25) * mm});
            skLineSegment(sketch, "E1292", {"start": v(-305.46, 29.25) * mm, "end": v(-304.82, 29.58) * mm});
            skLineSegment(sketch, "E1293", {"start": v(-304.82, 29.58) * mm, "end": v(-304.17, 29.8) * mm});
            skLineSegment(sketch, "E1294", {"start": v(-304.17, 29.8) * mm, "end": v(-303.48, 29.97) * mm});
            skLineSegment(sketch, "E1295", {"start": v(-303.48, 29.97) * mm, "end": v(-302.76, 30.1) * mm});
            skLineSegment(sketch, "E1296", {"start": v(-302.76, 30.1) * mm, "end": v(-302.04, 30.12) * mm});
            skLineSegment(sketch, "E1297", {"start": v(-302.04, 30.12) * mm, "end": v(-301.3, 30.1) * mm});
            skLineSegment(sketch, "E1298", {"start": v(-301.3, 30.1) * mm, "end": v(-300.58, 30) * mm});
            skLineSegment(sketch, "E1299", {"start": v(-300.58, 30) * mm, "end": v(-299.9, 29.82) * mm});
            skLineSegment(sketch, "E1300", {"start": v(-299.9, 29.82) * mm, "end": v(-299.24, 29.6) * mm});
            skLineSegment(sketch, "E1301", {"start": v(-299.24, 29.6) * mm, "end": v(-298.62, 29.28) * mm});
            skLineSegment(sketch, "E1302", {"start": v(-298.62, 29.28) * mm, "end": v(-298.02, 28.93) * mm});
            skLineSegment(sketch, "E1303", {"start": v(-298.02, 28.93) * mm, "end": v(-297.45, 28.48) * mm});
            skLineSegment(sketch, "E1304", {"start": v(-297.45, 28.48) * mm, "end": v(-296.9, 27.99) * mm});
            skLineSegment(sketch, "E1305", {"start": v(-296.9, 27.99) * mm, "end": v(-296.4, 27.44) * mm});
            skLineSegment(sketch, "E1306", {"start": v(-296.4, 27.44) * mm, "end": v(-295.96, 26.87) * mm});
            skLineSegment(sketch, "E1307", {"start": v(-295.96, 26.87) * mm, "end": v(-295.62, 26.28) * mm});
            skLineSegment(sketch, "E1308", {"start": v(-295.62, 26.28) * mm, "end": v(-295.3, 25.66) * mm});
            skLineSegment(sketch, "E1309", {"start": v(-295.3, 25.66) * mm, "end": v(-295.07, 24.99) * mm});
            skLineSegment(sketch, "E1310", {"start": v(-295.07, 24.99) * mm, "end": v(-294.9, 24.32) * mm});
            skLineSegment(sketch, "E1311", {"start": v(-294.9, 24.32) * mm, "end": v(-294.8, 23.6) * mm});
            skLineSegment(sketch, "E1312", {"start": v(-294.8, 23.6) * mm, "end": v(-294.77, 22.85) * mm});
            skLineSegment(sketch, "E1313", {"start": v(-294.77, 22.85) * mm, "end": v(-294.77, 17.55) * mm});
            skLineSegment(sketch, "E1314", {"start": v(-294.77, 17.55) * mm, "end": v(-294.8, 16.9) * mm});
            skLineSegment(sketch, "E1315", {"start": v(-294.8, 16.9) * mm, "end": v(-294.87, 16.3) * mm});
            skLineSegment(sketch, "E1316", {"start": v(-294.87, 16.3) * mm, "end": v(-295.02, 15.7) * mm});
            skLineSegment(sketch, "E1317", {"start": v(-295.02, 15.7) * mm, "end": v(-295.22, 15.16) * mm});
            skLineSegment(sketch, "E1318", {"start": v(-295.22, 15.16) * mm, "end": v(-295.47, 14.64) * mm});
            skLineSegment(sketch, "E1319", {"start": v(-295.47, 14.64) * mm, "end": v(-295.77, 14.12) * mm});
            skLineSegment(sketch, "E1320", {"start": v(-295.77, 14.12) * mm, "end": v(-296.14, 13.65) * mm});
            skLineSegment(sketch, "E1321", {"start": v(-296.14, 13.65) * mm, "end": v(-296.53, 13.18) * mm});
            skLineSegment(sketch, "E1322", {"start": v(-296.53, 13.18) * mm, "end": v(-296.14, 12.73) * mm});
            skLineSegment(sketch, "E1323", {"start": v(-296.14, 12.73) * mm, "end": v(-295.77, 12.26) * mm});
            skLineSegment(sketch, "E1324", {"start": v(-295.77, 12.26) * mm, "end": v(-295.47, 11.74) * mm});
            skLineSegment(sketch, "E1325", {"start": v(-295.47, 11.74) * mm, "end": v(-295.22, 11.22) * mm});
            skLineSegment(sketch, "E1326", {"start": v(-295.22, 11.22) * mm, "end": v(-295.02, 10.67) * mm});
            skLineSegment(sketch, "E1327", {"start": v(-295.02, 10.67) * mm, "end": v(-294.87, 10.08) * mm});
            skLineSegment(sketch, "E1328", {"start": v(-294.87, 10.08) * mm, "end": v(-294.8, 9.48) * mm});
            skLineSegment(sketch, "E1329", {"start": v(-294.8, 9.48) * mm, "end": v(-294.77, 8.84) * mm});
            skLineSegment(sketch, "E1330", {"start": v(-294.77, 8.84) * mm, "end": v(-294.77, 3.5) * mm});
            skLineSegment(sketch, "E1331", {"start": v(-294.77, 3.5) * mm, "end": v(-294.8, 2.76) * mm});
            skLineSegment(sketch, "E1332", {"start": v(-294.8, 2.76) * mm, "end": v(-294.9, 2.04) * mm});
            skLineSegment(sketch, "E1333", {"start": v(-294.9, 2.04) * mm, "end": v(-295.07, 1.37) * mm});
            skLineSegment(sketch, "E1334", {"start": v(-295.07, 1.37) * mm, "end": v(-295.3, 0.7) * mm});
            skLineSegment(sketch, "E1335", {"start": v(-295.3, 0.7) * mm, "end": v(-295.62, 0.08) * mm});
            skLineSegment(sketch, "E1336", {"start": v(-295.62, 0.08) * mm, "end": v(-295.96, -0.51) * mm});
            skLineSegment(sketch, "E1337", {"start": v(-295.96, -0.51) * mm, "end": v(-296.4, -1.08) * mm});
            skLineSegment(sketch, "E1338", {"start": v(-296.4, -1.08) * mm, "end": v(-296.9, -1.63) * mm});
            skLineSegment(sketch, "E1339", {"start": v(-296.9, -1.63) * mm, "end": v(-297.45, -2.12) * mm});
            skLineSegment(sketch, "E1340", {"start": v(-297.45, -2.12) * mm, "end": v(-298.02, -2.57) * mm});
            skLineSegment(sketch, "E1341", {"start": v(-298.02, -2.57) * mm, "end": v(-298.62, -2.92) * mm});
            skLineSegment(sketch, "E1342", {"start": v(-298.62, -2.92) * mm, "end": v(-299.24, -3.24) * mm});
            skLineSegment(sketch, "E1343", {"start": v(-299.24, -3.24) * mm, "end": v(-299.9, -3.46) * mm});
            skLineSegment(sketch, "E1344", {"start": v(-299.9, -3.46) * mm, "end": v(-300.58, -3.64) * mm});
            skLineSegment(sketch, "E1345", {"start": v(-300.58, -3.64) * mm, "end": v(-301.3, -3.74) * mm});
            skLineSegment(sketch, "E1346", {"start": v(-301.3, -3.74) * mm, "end": v(-302.04, -3.76) * mm});
            skLineSegment(sketch, "E1347", {"start": v(-302.04, -3.76) * mm, "end": v(-302.76, -3.74) * mm});
            skLineSegment(sketch, "E1348", {"start": v(-302.76, -3.74) * mm, "end": v(-303.48, -3.61) * mm});
            skLineSegment(sketch, "E1349", {"start": v(-303.48, -3.61) * mm, "end": v(-304.17, -3.44) * mm});
            skLineSegment(sketch, "E1350", {"start": v(-304.17, -3.44) * mm, "end": v(-304.82, -3.22) * mm});
            skLineSegment(sketch, "E1351", {"start": v(-304.82, -3.22) * mm, "end": v(-305.46, -2.9) * mm});
            skLineSegment(sketch, "E1352", {"start": v(-305.46, -2.9) * mm, "end": v(-306.08, -2.52) * mm});
            skLineSegment(sketch, "E1353", {"start": v(-306.08, -2.52) * mm, "end": v(-306.65, -2.05) * mm});
            skLineSegment(sketch, "E1354", {"start": v(-306.65, -2.05) * mm, "end": v(-307.22, -1.53) * mm});
            skLineSegment(sketch, "E1355", {"start": v(-307.22, -1.53) * mm, "end": v(-307.37, -1.38) * mm});
            skLineSegment(sketch, "E1356", {"start": v(-307.37, -1.38) * mm, "end": v(-307.47, -1.23) * mm});
            skLineSegment(sketch, "E1357", {"start": v(-307.47, -1.23) * mm, "end": v(-307.57, -1.08) * mm});
            skLineSegment(sketch, "E1358", {"start": v(-307.57, -1.08) * mm, "end": v(-307.67, -0.9) * mm});
            skLineSegment(sketch, "E1359", {"start": v(-307.67, -0.9) * mm, "end": v(-307.72, -0.74) * mm});
            skLineSegment(sketch, "E1360", {"start": v(-307.72, -0.74) * mm, "end": v(-307.77, -0.56) * mm});
            skLineSegment(sketch, "E1361", {"start": v(-307.77, -0.56) * mm, "end": v(-307.8, -0.36) * mm});
            skLineSegment(sketch, "E1362", {"start": v(-289.44, 2.76) * mm, "end": v(-289.49, 3.5) * mm});
            skLineSegment(sketch, "E1363", {"start": v(-289.49, 3.5) * mm, "end": v(-289.49, 10.25) * mm});
            skLineSegment(sketch, "E1364", {"start": v(-289.49, 10.25) * mm, "end": v(-289.46, 10.43) * mm});
            skLineSegment(sketch, "E1365", {"start": v(-289.46, 10.43) * mm, "end": v(-289.44, 10.62) * mm});
            skLineSegment(sketch, "E1366", {"start": v(-289.44, 10.62) * mm, "end": v(-289.4, 10.8) * mm});
            skLineSegment(sketch, "E1367", {"start": v(-289.4, 10.8) * mm, "end": v(-289.34, 10.97) * mm});
            skLineSegment(sketch, "E1368", {"start": v(-289.34, 10.97) * mm, "end": v(-289.27, 11.15) * mm});
            skLineSegment(sketch, "E1369", {"start": v(-289.27, 11.15) * mm, "end": v(-289.17, 11.32) * mm});
            skLineSegment(sketch, "E1370", {"start": v(-289.17, 11.32) * mm, "end": v(-289.04, 11.47) * mm});
            skLineSegment(sketch, "E1371", {"start": v(-289.04, 11.47) * mm, "end": v(-288.92, 11.62) * mm});
            skLineSegment(sketch, "E1372", {"start": v(-288.92, 11.62) * mm, "end": v(-288.77, 11.74) * mm});
            skLineSegment(sketch, "E1373", {"start": v(-288.77, 11.74) * mm, "end": v(-288.62, 11.87) * mm});
            skLineSegment(sketch, "E1374", {"start": v(-288.62, 11.87) * mm, "end": v(-288.45, 11.96) * mm});
            skLineSegment(sketch, "E1375", {"start": v(-288.45, 11.96) * mm, "end": v(-288.27, 12.04) * mm});
            skLineSegment(sketch, "E1376", {"start": v(-288.27, 12.04) * mm, "end": v(-288.1, 12.09) * mm});
            skLineSegment(sketch, "E1377", {"start": v(-288.1, 12.09) * mm, "end": v(-287.93, 12.14) * mm});
            skLineSegment(sketch, "E1378", {"start": v(-287.93, 12.14) * mm, "end": v(-287.73, 12.16) * mm});
            skLineSegment(sketch, "E1379", {"start": v(-287.73, 12.16) * mm, "end": v(-287.55, 12.19) * mm});
            skLineSegment(sketch, "E1380", {"start": v(-287.55, 12.19) * mm, "end": v(-287.36, 12.16) * mm});
            skLineSegment(sketch, "E1381", {"start": v(-287.36, 12.16) * mm, "end": v(-287.16, 12.14) * mm});
            skLineSegment(sketch, "E1382", {"start": v(-287.16, 12.14) * mm, "end": v(-286.98, 12.09) * mm});
            skLineSegment(sketch, "E1383", {"start": v(-286.98, 12.09) * mm, "end": v(-286.81, 12.04) * mm});
            skLineSegment(sketch, "E1384", {"start": v(-286.81, 12.04) * mm, "end": v(-286.64, 11.96) * mm});
            skLineSegment(sketch, "E1385", {"start": v(-286.64, 11.96) * mm, "end": v(-286.46, 11.87) * mm});
            skLineSegment(sketch, "E1386", {"start": v(-286.46, 11.87) * mm, "end": v(-286.31, 11.74) * mm});
            skLineSegment(sketch, "E1387", {"start": v(-286.31, 11.74) * mm, "end": v(-286.17, 11.62) * mm});
            skLineSegment(sketch, "E1388", {"start": v(-286.17, 11.62) * mm, "end": v(-286.04, 11.47) * mm});
            skLineSegment(sketch, "E1389", {"start": v(-286.04, 11.47) * mm, "end": v(-285.92, 11.32) * mm});
            skLineSegment(sketch, "E1390", {"start": v(-285.92, 11.32) * mm, "end": v(-285.82, 11.15) * mm});
            skLineSegment(sketch, "E1391", {"start": v(-285.82, 11.15) * mm, "end": v(-285.74, 10.97) * mm});
            skLineSegment(sketch, "E1392", {"start": v(-285.74, 10.97) * mm, "end": v(-285.7, 10.8) * mm});
            skLineSegment(sketch, "E1393", {"start": v(-285.7, 10.8) * mm, "end": v(-285.64, 10.62) * mm});
            skLineSegment(sketch, "E1394", {"start": v(-285.64, 10.62) * mm, "end": v(-285.62, 10.43) * mm});
            skLineSegment(sketch, "E1395", {"start": v(-285.62, 10.43) * mm, "end": v(-285.62, 10.25) * mm});
            skLineSegment(sketch, "E1396", {"start": v(-285.62, 10.25) * mm, "end": v(-285.62, 3.5) * mm});
            skLineSegment(sketch, "E1397", {"start": v(-285.62, 3.5) * mm, "end": v(-285.6, 3.16) * mm});
            skLineSegment(sketch, "E1398", {"start": v(-285.6, 3.16) * mm, "end": v(-285.55, 2.81) * mm});
            skLineSegment(sketch, "E1399", {"start": v(-285.55, 2.81) * mm, "end": v(-285.47, 2.49) * mm});
            skLineSegment(sketch, "E1400", {"start": v(-285.47, 2.49) * mm, "end": v(-285.37, 2.2) * mm});
            skLineSegment(sketch, "E1401", {"start": v(-285.37, 2.2) * mm, "end": v(-285.22, 1.9) * mm});
            skLineSegment(sketch, "E1402", {"start": v(-285.22, 1.9) * mm, "end": v(-285.05, 1.62) * mm});
            skLineSegment(sketch, "E1403", {"start": v(-285.05, 1.62) * mm, "end": v(-284.85, 1.35) * mm});
            skLineSegment(sketch, "E1404", {"start": v(-284.85, 1.35) * mm, "end": v(-284.63, 1.1) * mm});
            skLineSegment(sketch, "E1405", {"start": v(-284.63, 1.1) * mm, "end": v(-284.35, 0.88) * mm});
            skLineSegment(sketch, "E1406", {"start": v(-284.35, 0.88) * mm, "end": v(-284.08, 0.65) * mm});
            skLineSegment(sketch, "E1407", {"start": v(-284.08, 0.65) * mm, "end": v(-283.8, 0.5) * mm});
            skLineSegment(sketch, "E1408", {"start": v(-283.8, 0.5) * mm, "end": v(-283.51, 0.36) * mm});
            skLineSegment(sketch, "E1409", {"start": v(-283.51, 0.36) * mm, "end": v(-283.21, 0.26) * mm});
            skLineSegment(sketch, "E1410", {"start": v(-283.21, 0.26) * mm, "end": v(-282.9, 0.16) * mm});
            skLineSegment(sketch, "E1411", {"start": v(-282.9, 0.16) * mm, "end": v(-282.57, 0.13) * mm});
            skLineSegment(sketch, "E1412", {"start": v(-282.57, 0.13) * mm, "end": v(-282.22, 0.1) * mm});
            skLineSegment(sketch, "E1413", {"start": v(-282.22, 0.1) * mm, "end": v(-281.87, 0.13) * mm});
            skLineSegment(sketch, "E1414", {"start": v(-281.87, 0.13) * mm, "end": v(-281.55, 0.16) * mm});
            skLineSegment(sketch, "E1415", {"start": v(-281.55, 0.16) * mm, "end": v(-281.23, 0.26) * mm});
            skLineSegment(sketch, "E1416", {"start": v(-281.23, 0.26) * mm, "end": v(-280.93, 0.36) * mm});
            skLineSegment(sketch, "E1417", {"start": v(-280.93, 0.36) * mm, "end": v(-280.63, 0.5) * mm});
            skLineSegment(sketch, "E1418", {"start": v(-280.63, 0.5) * mm, "end": v(-280.36, 0.65) * mm});
            skLineSegment(sketch, "E1419", {"start": v(-280.36, 0.65) * mm, "end": v(-280.09, 0.88) * mm});
            skLineSegment(sketch, "E1420", {"start": v(-280.09, 0.88) * mm, "end": v(-279.82, 1.1) * mm});
            skLineSegment(sketch, "E1421", {"start": v(-279.82, 1.1) * mm, "end": v(-279.6, 1.35) * mm});
            skLineSegment(sketch, "E1422", {"start": v(-279.6, 1.35) * mm, "end": v(-279.4, 1.62) * mm});
            skLineSegment(sketch, "E1423", {"start": v(-279.4, 1.62) * mm, "end": v(-279.22, 1.9) * mm});
            skLineSegment(sketch, "E1424", {"start": v(-279.22, 1.9) * mm, "end": v(-279.07, 2.2) * mm});
            skLineSegment(sketch, "E1425", {"start": v(-279.07, 2.2) * mm, "end": v(-278.97, 2.49) * mm});
            skLineSegment(sketch, "E1426", {"start": v(-278.97, 2.49) * mm, "end": v(-278.9, 2.81) * mm});
            skLineSegment(sketch, "E1427", {"start": v(-278.9, 2.81) * mm, "end": v(-278.85, 3.16) * mm});
            skLineSegment(sketch, "E1428", {"start": v(-278.85, 3.16) * mm, "end": v(-278.82, 3.5) * mm});
            skLineSegment(sketch, "E1429", {"start": v(-278.82, 3.5) * mm, "end": v(-278.82, 10.25) * mm});
            skLineSegment(sketch, "E1430", {"start": v(-278.82, 10.25) * mm, "end": v(-278.82, 10.43) * mm});
            skLineSegment(sketch, "E1431", {"start": v(-278.82, 10.43) * mm, "end": v(-278.8, 10.62) * mm});
            skLineSegment(sketch, "E1432", {"start": v(-278.8, 10.62) * mm, "end": v(-278.75, 10.8) * mm});
            skLineSegment(sketch, "E1433", {"start": v(-278.75, 10.8) * mm, "end": v(-278.7, 10.97) * mm});
            skLineSegment(sketch, "E1434", {"start": v(-278.7, 10.97) * mm, "end": v(-278.63, 11.15) * mm});
            skLineSegment(sketch, "E1435", {"start": v(-278.63, 11.15) * mm, "end": v(-278.53, 11.32) * mm});
            skLineSegment(sketch, "E1436", {"start": v(-278.53, 11.32) * mm, "end": v(-278.4, 11.47) * mm});
            skLineSegment(sketch, "E1437", {"start": v(-278.4, 11.47) * mm, "end": v(-278.28, 11.62) * mm});
            skLineSegment(sketch, "E1438", {"start": v(-278.28, 11.62) * mm, "end": v(-278.13, 11.74) * mm});
            skLineSegment(sketch, "E1439", {"start": v(-278.13, 11.74) * mm, "end": v(-277.98, 11.87) * mm});
            skLineSegment(sketch, "E1440", {"start": v(-277.98, 11.87) * mm, "end": v(-277.8, 11.96) * mm});
            skLineSegment(sketch, "E1441", {"start": v(-277.8, 11.96) * mm, "end": v(-277.63, 12.04) * mm});
            skLineSegment(sketch, "E1442", {"start": v(-277.63, 12.04) * mm, "end": v(-277.46, 12.09) * mm});
            skLineSegment(sketch, "E1443", {"start": v(-277.46, 12.09) * mm, "end": v(-277.29, 12.14) * mm});
            skLineSegment(sketch, "E1444", {"start": v(-277.29, 12.14) * mm, "end": v(-277.09, 12.16) * mm});
            skLineSegment(sketch, "E1445", {"start": v(-277.09, 12.16) * mm, "end": v(-276.89, 12.19) * mm});
            skLineSegment(sketch, "E1446", {"start": v(-276.89, 12.19) * mm, "end": v(-276.72, 12.16) * mm});
            skLineSegment(sketch, "E1447", {"start": v(-276.72, 12.16) * mm, "end": v(-276.52, 12.14) * mm});
            skLineSegment(sketch, "E1448", {"start": v(-276.52, 12.14) * mm, "end": v(-276.34, 12.09) * mm});
            skLineSegment(sketch, "E1449", {"start": v(-276.34, 12.09) * mm, "end": v(-276.17, 12.04) * mm});
            skLineSegment(sketch, "E1450", {"start": v(-276.17, 12.04) * mm, "end": v(-276, 11.96) * mm});
            skLineSegment(sketch, "E1451", {"start": v(-276, 11.96) * mm, "end": v(-275.82, 11.87) * mm});
            skLineSegment(sketch, "E1452", {"start": v(-275.82, 11.87) * mm, "end": v(-275.67, 11.74) * mm});
            skLineSegment(sketch, "E1453", {"start": v(-275.67, 11.74) * mm, "end": v(-275.52, 11.62) * mm});
            skLineSegment(sketch, "E1454", {"start": v(-275.52, 11.62) * mm, "end": v(-275.4, 11.47) * mm});
            skLineSegment(sketch, "E1455", {"start": v(-275.4, 11.47) * mm, "end": v(-275.28, 11.32) * mm});
            skLineSegment(sketch, "E1456", {"start": v(-275.28, 11.32) * mm, "end": v(-275.18, 11.15) * mm});
            skLineSegment(sketch, "E1457", {"start": v(-275.18, 11.15) * mm, "end": v(-275.1, 10.97) * mm});
            skLineSegment(sketch, "E1458", {"start": v(-275.1, 10.97) * mm, "end": v(-275.05, 10.8) * mm});
            skLineSegment(sketch, "E1459", {"start": v(-275.05, 10.8) * mm, "end": v(-275, 10.62) * mm});
            skLineSegment(sketch, "E1460", {"start": v(-275, 10.62) * mm, "end": v(-274.98, 10.43) * mm});
            skLineSegment(sketch, "E1461", {"start": v(-274.98, 10.43) * mm, "end": v(-274.95, 10.25) * mm});
            skLineSegment(sketch, "E1462", {"start": v(-274.95, 10.25) * mm, "end": v(-274.95, 3.5) * mm});
            skLineSegment(sketch, "E1463", {"start": v(-274.95, 3.5) * mm, "end": v(-275, 2.76) * mm});
            skLineSegment(sketch, "E1464", {"start": v(-275, 2.76) * mm, "end": v(-275.1, 2.04) * mm});
            skLineSegment(sketch, "E1465", {"start": v(-275.1, 2.04) * mm, "end": v(-275.28, 1.37) * mm});
            skLineSegment(sketch, "E1466", {"start": v(-275.28, 1.37) * mm, "end": v(-275.5, 0.7) * mm});
            skLineSegment(sketch, "E1467", {"start": v(-275.5, 0.7) * mm, "end": v(-275.8, 0.08) * mm});
            skLineSegment(sketch, "E1468", {"start": v(-275.8, 0.08) * mm, "end": v(-276.17, -0.51) * mm});
            skLineSegment(sketch, "E1469", {"start": v(-276.17, -0.51) * mm, "end": v(-276.6, -1.08) * mm});
            skLineSegment(sketch, "E1470", {"start": v(-276.6, -1.08) * mm, "end": v(-277.09, -1.63) * mm});
            skLineSegment(sketch, "E1471", {"start": v(-277.09, -1.63) * mm, "end": v(-277.63, -2.12) * mm});
            skLineSegment(sketch, "E1472", {"start": v(-277.63, -2.12) * mm, "end": v(-278.2, -2.57) * mm});
            skLineSegment(sketch, "E1473", {"start": v(-278.2, -2.57) * mm, "end": v(-278.82, -2.92) * mm});
            skLineSegment(sketch, "E1474", {"start": v(-278.82, -2.92) * mm, "end": v(-279.44, -3.24) * mm});
            skLineSegment(sketch, "E1475", {"start": v(-279.44, -3.24) * mm, "end": v(-280.09, -3.46) * mm});
            skLineSegment(sketch, "E1476", {"start": v(-280.09, -3.46) * mm, "end": v(-280.78, -3.64) * mm});
            skLineSegment(sketch, "E1477", {"start": v(-280.78, -3.64) * mm, "end": v(-281.48, -3.74) * mm});
            skLineSegment(sketch, "E1478", {"start": v(-281.48, -3.74) * mm, "end": v(-282.22, -3.76) * mm});
            skLineSegment(sketch, "E1479", {"start": v(-282.22, -3.76) * mm, "end": v(-282.97, -3.74) * mm});
            skLineSegment(sketch, "E1480", {"start": v(-282.97, -3.74) * mm, "end": v(-283.66, -3.64) * mm});
            skLineSegment(sketch, "E1481", {"start": v(-283.66, -3.64) * mm, "end": v(-284.35, -3.46) * mm});
            skLineSegment(sketch, "E1482", {"start": v(-284.35, -3.46) * mm, "end": v(-285, -3.24) * mm});
            skLineSegment(sketch, "E1483", {"start": v(-285, -3.24) * mm, "end": v(-285.62, -2.92) * mm});
            skLineSegment(sketch, "E1484", {"start": v(-285.62, -2.92) * mm, "end": v(-286.24, -2.57) * mm});
            skLineSegment(sketch, "E1485", {"start": v(-286.24, -2.57) * mm, "end": v(-286.81, -2.12) * mm});
            skLineSegment(sketch, "E1486", {"start": v(-286.81, -2.12) * mm, "end": v(-287.36, -1.63) * mm});
            skLineSegment(sketch, "E1487", {"start": v(-287.36, -1.63) * mm, "end": v(-287.85, -1.08) * mm});
            skLineSegment(sketch, "E1488", {"start": v(-287.85, -1.08) * mm, "end": v(-288.27, -0.51) * mm});
            skLineSegment(sketch, "E1489", {"start": v(-288.27, -0.51) * mm, "end": v(-288.65, 0.08) * mm});
            skLineSegment(sketch, "E1490", {"start": v(-288.65, 0.08) * mm, "end": v(-288.94, 0.7) * mm});
            skLineSegment(sketch, "E1491", {"start": v(-288.94, 0.7) * mm, "end": v(-289.17, 1.37) * mm});
            skLineSegment(sketch, "E1492", {"start": v(-289.17, 1.37) * mm, "end": v(-289.34, 2.04) * mm});
            skLineSegment(sketch, "E1493", {"start": v(-289.34, 2.04) * mm, "end": v(-289.44, 2.76) * mm});
            skLineSegment(sketch, "E1494", {"start": v(-289.44, 23.6) * mm, "end": v(-289.34, 24.32) * mm});
            skLineSegment(sketch, "E1495", {"start": v(-289.34, 24.32) * mm, "end": v(-289.17, 24.99) * mm});
            skLineSegment(sketch, "E1496", {"start": v(-289.17, 24.99) * mm, "end": v(-288.94, 25.66) * mm});
            skLineSegment(sketch, "E1497", {"start": v(-288.94, 25.66) * mm, "end": v(-288.65, 26.28) * mm});
            skLineSegment(sketch, "E1498", {"start": v(-288.65, 26.28) * mm, "end": v(-288.27, 26.87) * mm});
            skLineSegment(sketch, "E1499", {"start": v(-288.27, 26.87) * mm, "end": v(-287.85, 27.44) * mm});
            skLineSegment(sketch, "E1500", {"start": v(-287.85, 27.44) * mm, "end": v(-287.36, 27.99) * mm});
            skLineSegment(sketch, "E1501", {"start": v(-287.36, 27.99) * mm, "end": v(-286.81, 28.48) * mm});
            skLineSegment(sketch, "E1502", {"start": v(-286.81, 28.48) * mm, "end": v(-286.24, 28.93) * mm});
            skLineSegment(sketch, "E1503", {"start": v(-286.24, 28.93) * mm, "end": v(-285.62, 29.28) * mm});
            skLineSegment(sketch, "E1504", {"start": v(-285.62, 29.28) * mm, "end": v(-285, 29.6) * mm});
            skLineSegment(sketch, "E1505", {"start": v(-285, 29.6) * mm, "end": v(-284.35, 29.82) * mm});
            skLineSegment(sketch, "E1506", {"start": v(-284.35, 29.82) * mm, "end": v(-283.66, 30) * mm});
            skLineSegment(sketch, "E1507", {"start": v(-283.66, 30) * mm, "end": v(-282.97, 30.1) * mm});
            skLineSegment(sketch, "E1508", {"start": v(-282.97, 30.1) * mm, "end": v(-282.22, 30.12) * mm});
            skLineSegment(sketch, "E1509", {"start": v(-282.22, 30.12) * mm, "end": v(-281.48, 30.1) * mm});
            skLineSegment(sketch, "E1510", {"start": v(-281.48, 30.1) * mm, "end": v(-280.78, 30) * mm});
            skLineSegment(sketch, "E1511", {"start": v(-280.78, 30) * mm, "end": v(-280.09, 29.82) * mm});
            skLineSegment(sketch, "E1512", {"start": v(-280.09, 29.82) * mm, "end": v(-279.44, 29.6) * mm});
            skLineSegment(sketch, "E1513", {"start": v(-279.44, 29.6) * mm, "end": v(-278.82, 29.28) * mm});
            skLineSegment(sketch, "E1514", {"start": v(-278.82, 29.28) * mm, "end": v(-278.2, 28.93) * mm});
            skLineSegment(sketch, "E1515", {"start": v(-278.2, 28.93) * mm, "end": v(-277.63, 28.48) * mm});
            skLineSegment(sketch, "E1516", {"start": v(-277.63, 28.48) * mm, "end": v(-277.09, 27.99) * mm});
            skLineSegment(sketch, "E1517", {"start": v(-277.09, 27.99) * mm, "end": v(-276.6, 27.44) * mm});
            skLineSegment(sketch, "E1518", {"start": v(-276.6, 27.44) * mm, "end": v(-276.17, 26.87) * mm});
            skLineSegment(sketch, "E1519", {"start": v(-276.17, 26.87) * mm, "end": v(-275.8, 26.28) * mm});
            skLineSegment(sketch, "E1520", {"start": v(-275.8, 26.28) * mm, "end": v(-275.5, 25.66) * mm});
            skLineSegment(sketch, "E1521", {"start": v(-275.5, 25.66) * mm, "end": v(-275.28, 24.99) * mm});
            skLineSegment(sketch, "E1522", {"start": v(-275.28, 24.99) * mm, "end": v(-275.1, 24.32) * mm});
            skLineSegment(sketch, "E1523", {"start": v(-275.1, 24.32) * mm, "end": v(-275, 23.6) * mm});
            skLineSegment(sketch, "E1524", {"start": v(-275, 23.6) * mm, "end": v(-274.95, 22.85) * mm});
            skLineSegment(sketch, "E1525", {"start": v(-274.95, 22.85) * mm, "end": v(-274.95, 16.1) * mm});
            skLineSegment(sketch, "E1526", {"start": v(-274.95, 16.1) * mm, "end": v(-274.98, 15.93) * mm});
            skLineSegment(sketch, "E1527", {"start": v(-274.98, 15.93) * mm, "end": v(-275, 15.73) * mm});
            skLineSegment(sketch, "E1528", {"start": v(-275, 15.73) * mm, "end": v(-275.05, 15.56) * mm});
            skLineSegment(sketch, "E1529", {"start": v(-275.05, 15.56) * mm, "end": v(-275.1, 15.39) * mm});
            skLineSegment(sketch, "E1530", {"start": v(-275.1, 15.39) * mm, "end": v(-275.18, 15.21) * mm});
            skLineSegment(sketch, "E1531", {"start": v(-275.18, 15.21) * mm, "end": v(-275.28, 15.04) * mm});
            skLineSegment(sketch, "E1532", {"start": v(-275.28, 15.04) * mm, "end": v(-275.4, 14.9) * mm});
            skLineSegment(sketch, "E1533", {"start": v(-275.4, 14.9) * mm, "end": v(-275.52, 14.74) * mm});
            skLineSegment(sketch, "E1534", {"start": v(-275.52, 14.74) * mm, "end": v(-275.67, 14.62) * mm});
            skLineSegment(sketch, "E1535", {"start": v(-275.67, 14.62) * mm, "end": v(-275.82, 14.5) * mm});
            skLineSegment(sketch, "E1536", {"start": v(-275.82, 14.5) * mm, "end": v(-276, 14.4) * mm});
            skLineSegment(sketch, "E1537", {"start": v(-276, 14.4) * mm, "end": v(-276.17, 14.32) * mm});
            skLineSegment(sketch, "E1538", {"start": v(-276.17, 14.32) * mm, "end": v(-276.34, 14.27) * mm});
            skLineSegment(sketch, "E1539", {"start": v(-276.34, 14.27) * mm, "end": v(-276.52, 14.22) * mm});
            skLineSegment(sketch, "E1540", {"start": v(-276.52, 14.22) * mm, "end": v(-276.72, 14.2) * mm});
            skLineSegment(sketch, "E1541", {"start": v(-276.72, 14.2) * mm, "end": v(-276.89, 14.17) * mm});
            skLineSegment(sketch, "E1542", {"start": v(-276.89, 14.17) * mm, "end": v(-277.09, 14.2) * mm});
            skLineSegment(sketch, "E1543", {"start": v(-277.09, 14.2) * mm, "end": v(-277.29, 14.22) * mm});
            skLineSegment(sketch, "E1544", {"start": v(-277.29, 14.22) * mm, "end": v(-277.46, 14.27) * mm});
            skLineSegment(sketch, "E1545", {"start": v(-277.46, 14.27) * mm, "end": v(-277.63, 14.32) * mm});
            skLineSegment(sketch, "E1546", {"start": v(-277.63, 14.32) * mm, "end": v(-277.8, 14.4) * mm});
            skLineSegment(sketch, "E1547", {"start": v(-277.8, 14.4) * mm, "end": v(-277.98, 14.5) * mm});
            skLineSegment(sketch, "E1548", {"start": v(-277.98, 14.5) * mm, "end": v(-278.13, 14.62) * mm});
            skLineSegment(sketch, "E1549", {"start": v(-278.13, 14.62) * mm, "end": v(-278.28, 14.74) * mm});
            skLineSegment(sketch, "E1550", {"start": v(-278.28, 14.74) * mm, "end": v(-278.4, 14.9) * mm});
            skLineSegment(sketch, "E1551", {"start": v(-278.4, 14.9) * mm, "end": v(-278.53, 15.04) * mm});
            skLineSegment(sketch, "E1552", {"start": v(-278.53, 15.04) * mm, "end": v(-278.63, 15.21) * mm});
            skLineSegment(sketch, "E1553", {"start": v(-278.63, 15.21) * mm, "end": v(-278.7, 15.39) * mm});
            skLineSegment(sketch, "E1554", {"start": v(-278.7, 15.39) * mm, "end": v(-278.75, 15.56) * mm});
            skLineSegment(sketch, "E1555", {"start": v(-278.75, 15.56) * mm, "end": v(-278.8, 15.73) * mm});
            skLineSegment(sketch, "E1556", {"start": v(-278.8, 15.73) * mm, "end": v(-278.82, 15.93) * mm});
            skLineSegment(sketch, "E1557", {"start": v(-278.82, 15.93) * mm, "end": v(-278.82, 16.1) * mm});
            skLineSegment(sketch, "E1558", {"start": v(-278.82, 16.1) * mm, "end": v(-278.82, 22.85) * mm});
            skLineSegment(sketch, "E1559", {"start": v(-278.82, 22.85) * mm, "end": v(-278.85, 23.2) * mm});
            skLineSegment(sketch, "E1560", {"start": v(-278.85, 23.2) * mm, "end": v(-278.9, 23.55) * mm});
            skLineSegment(sketch, "E1561", {"start": v(-278.9, 23.55) * mm, "end": v(-278.97, 23.87) * mm});
            skLineSegment(sketch, "E1562", {"start": v(-278.97, 23.87) * mm, "end": v(-279.07, 24.17) * mm});
            skLineSegment(sketch, "E1563", {"start": v(-279.07, 24.17) * mm, "end": v(-279.22, 24.47) * mm});
            skLineSegment(sketch, "E1564", {"start": v(-279.22, 24.47) * mm, "end": v(-279.4, 24.74) * mm});
            skLineSegment(sketch, "E1565", {"start": v(-279.4, 24.74) * mm, "end": v(-279.6, 25.01) * mm});
            skLineSegment(sketch, "E1566", {"start": v(-279.6, 25.01) * mm, "end": v(-279.82, 25.26) * mm});
            skLineSegment(sketch, "E1567", {"start": v(-279.82, 25.26) * mm, "end": v(-280.09, 25.48) * mm});
            skLineSegment(sketch, "E1568", {"start": v(-280.09, 25.48) * mm, "end": v(-280.36, 25.68) * mm});
            skLineSegment(sketch, "E1569", {"start": v(-280.36, 25.68) * mm, "end": v(-280.63, 25.86) * mm});
            skLineSegment(sketch, "E1570", {"start": v(-280.63, 25.86) * mm, "end": v(-280.93, 26) * mm});
            skLineSegment(sketch, "E1571", {"start": v(-280.93, 26) * mm, "end": v(-281.23, 26.1) * mm});
            skLineSegment(sketch, "E1572", {"start": v(-281.23, 26.1) * mm, "end": v(-281.55, 26.18) * mm});
            skLineSegment(sketch, "E1573", {"start": v(-281.55, 26.18) * mm, "end": v(-281.87, 26.23) * mm});
            skLineSegment(sketch, "E1574", {"start": v(-281.87, 26.23) * mm, "end": v(-282.22, 26.25) * mm});
            skLineSegment(sketch, "E1575", {"start": v(-282.22, 26.25) * mm, "end": v(-282.57, 26.23) * mm});
            skLineSegment(sketch, "E1576", {"start": v(-282.57, 26.23) * mm, "end": v(-282.9, 26.18) * mm});
            skLineSegment(sketch, "E1577", {"start": v(-282.9, 26.18) * mm, "end": v(-283.21, 26.1) * mm});
            skLineSegment(sketch, "E1578", {"start": v(-283.21, 26.1) * mm, "end": v(-283.51, 26) * mm});
            skLineSegment(sketch, "E1579", {"start": v(-283.51, 26) * mm, "end": v(-283.8, 25.86) * mm});
            skLineSegment(sketch, "E1580", {"start": v(-283.8, 25.86) * mm, "end": v(-284.08, 25.68) * mm});
            skLineSegment(sketch, "E1581", {"start": v(-284.08, 25.68) * mm, "end": v(-284.35, 25.48) * mm});
            skLineSegment(sketch, "E1582", {"start": v(-284.35, 25.48) * mm, "end": v(-284.63, 25.26) * mm});
            skLineSegment(sketch, "E1583", {"start": v(-284.63, 25.26) * mm, "end": v(-284.85, 25.01) * mm});
            skLineSegment(sketch, "E1584", {"start": v(-284.85, 25.01) * mm, "end": v(-285.05, 24.74) * mm});
            skLineSegment(sketch, "E1585", {"start": v(-285.05, 24.74) * mm, "end": v(-285.22, 24.47) * mm});
            skLineSegment(sketch, "E1586", {"start": v(-285.22, 24.47) * mm, "end": v(-285.37, 24.17) * mm});
            skLineSegment(sketch, "E1587", {"start": v(-285.37, 24.17) * mm, "end": v(-285.47, 23.87) * mm});
            skLineSegment(sketch, "E1588", {"start": v(-285.47, 23.87) * mm, "end": v(-285.55, 23.55) * mm});
            skLineSegment(sketch, "E1589", {"start": v(-285.55, 23.55) * mm, "end": v(-285.6, 23.2) * mm});
            skLineSegment(sketch, "E1590", {"start": v(-285.6, 23.2) * mm, "end": v(-285.62, 22.85) * mm});
            skLineSegment(sketch, "E1591", {"start": v(-285.62, 22.85) * mm, "end": v(-285.62, 16.1) * mm});
            skLineSegment(sketch, "E1592", {"start": v(-285.62, 16.1) * mm, "end": v(-285.62, 15.93) * mm});
            skLineSegment(sketch, "E1593", {"start": v(-285.62, 15.93) * mm, "end": v(-285.64, 15.73) * mm});
            skLineSegment(sketch, "E1594", {"start": v(-285.64, 15.73) * mm, "end": v(-285.7, 15.56) * mm});
            skLineSegment(sketch, "E1595", {"start": v(-285.7, 15.56) * mm, "end": v(-285.74, 15.39) * mm});
            skLineSegment(sketch, "E1596", {"start": v(-285.74, 15.39) * mm, "end": v(-285.82, 15.21) * mm});
            skLineSegment(sketch, "E1597", {"start": v(-285.82, 15.21) * mm, "end": v(-285.92, 15.04) * mm});
            skLineSegment(sketch, "E1598", {"start": v(-285.92, 15.04) * mm, "end": v(-286.04, 14.9) * mm});
            skLineSegment(sketch, "E1599", {"start": v(-286.04, 14.9) * mm, "end": v(-286.17, 14.74) * mm});
            skLineSegment(sketch, "E1600", {"start": v(-286.17, 14.74) * mm, "end": v(-286.31, 14.62) * mm});
            skLineSegment(sketch, "E1601", {"start": v(-286.31, 14.62) * mm, "end": v(-286.46, 14.5) * mm});
            skLineSegment(sketch, "E1602", {"start": v(-286.46, 14.5) * mm, "end": v(-286.64, 14.4) * mm});
            skLineSegment(sketch, "E1603", {"start": v(-286.64, 14.4) * mm, "end": v(-286.81, 14.32) * mm});
            skLineSegment(sketch, "E1604", {"start": v(-286.81, 14.32) * mm, "end": v(-286.98, 14.27) * mm});
            skLineSegment(sketch, "E1605", {"start": v(-286.98, 14.27) * mm, "end": v(-287.16, 14.22) * mm});
            skLineSegment(sketch, "E1606", {"start": v(-287.16, 14.22) * mm, "end": v(-287.36, 14.2) * mm});
            skLineSegment(sketch, "E1607", {"start": v(-287.36, 14.2) * mm, "end": v(-287.55, 14.17) * mm});
            skLineSegment(sketch, "E1608", {"start": v(-287.55, 14.17) * mm, "end": v(-287.73, 14.2) * mm});
            skLineSegment(sketch, "E1609", {"start": v(-287.73, 14.2) * mm, "end": v(-287.93, 14.22) * mm});
            skLineSegment(sketch, "E1610", {"start": v(-287.93, 14.22) * mm, "end": v(-288.1, 14.27) * mm});
            skLineSegment(sketch, "E1611", {"start": v(-288.1, 14.27) * mm, "end": v(-288.27, 14.32) * mm});
            skLineSegment(sketch, "E1612", {"start": v(-288.27, 14.32) * mm, "end": v(-288.45, 14.4) * mm});
            skLineSegment(sketch, "E1613", {"start": v(-288.45, 14.4) * mm, "end": v(-288.62, 14.5) * mm});
            skLineSegment(sketch, "E1614", {"start": v(-288.62, 14.5) * mm, "end": v(-288.77, 14.62) * mm});
            skLineSegment(sketch, "E1615", {"start": v(-288.77, 14.62) * mm, "end": v(-288.92, 14.74) * mm});
            skLineSegment(sketch, "E1616", {"start": v(-288.92, 14.74) * mm, "end": v(-289.04, 14.9) * mm});
            skLineSegment(sketch, "E1617", {"start": v(-289.04, 14.9) * mm, "end": v(-289.17, 15.04) * mm});
            skLineSegment(sketch, "E1618", {"start": v(-289.17, 15.04) * mm, "end": v(-289.27, 15.21) * mm});
            skLineSegment(sketch, "E1619", {"start": v(-289.27, 15.21) * mm, "end": v(-289.34, 15.39) * mm});
            skLineSegment(sketch, "E1620", {"start": v(-289.34, 15.39) * mm, "end": v(-289.4, 15.56) * mm});
            skLineSegment(sketch, "E1621", {"start": v(-289.4, 15.56) * mm, "end": v(-289.44, 15.73) * mm});
            skLineSegment(sketch, "E1622", {"start": v(-289.44, 15.73) * mm, "end": v(-289.46, 15.93) * mm});
            skLineSegment(sketch, "E1623", {"start": v(-289.46, 15.93) * mm, "end": v(-289.49, 16.1) * mm});
            skLineSegment(sketch, "E1624", {"start": v(-289.49, 16.1) * mm, "end": v(-289.49, 22.85) * mm});
            skLineSegment(sketch, "E1625", {"start": v(-289.49, 22.85) * mm, "end": v(-289.44, 23.6) * mm});
            skLineSegment(sketch, "E1626", {"start": v(-271.06, 6.95) * mm, "end": v(-271.08, 7.15) * mm});
            skLineSegment(sketch, "E1627", {"start": v(-271.08, 7.15) * mm, "end": v(-271.08, 7.35) * mm});
            skLineSegment(sketch, "E1628", {"start": v(-271.08, 7.35) * mm, "end": v(-271.08, 7.43) * mm});
            skLineSegment(sketch, "E1629", {"start": v(-271.08, 7.43) * mm, "end": v(-271.08, 7.5) * mm});
            skLineSegment(sketch, "E1630", {"start": v(-271.08, 7.5) * mm, "end": v(-271.08, 7.57) * mm});
            skLineSegment(sketch, "E1631", {"start": v(-271.08, 7.57) * mm, "end": v(-271.08, 7.65) * mm});
            skLineSegment(sketch, "E1632", {"start": v(-271.08, 7.65) * mm, "end": v(-271.06, 7.72) * mm});
            skLineSegment(sketch, "E1633", {"start": v(-271.06, 7.72) * mm, "end": v(-271.03, 7.77) * mm});
            skLineSegment(sketch, "E1634", {"start": v(-271.03, 7.77) * mm, "end": v(-271.03, 7.85) * mm});
            skLineSegment(sketch, "E1635", {"start": v(-271.03, 7.85) * mm, "end": v(-271, 7.9) * mm});
            skLineSegment(sketch, "E1636", {"start": v(-271, 7.9) * mm, "end": v(-267.21, 27.7) * mm});
            skLineSegment(sketch, "E1637", {"start": v(-267.21, 27.7) * mm, "end": v(-267.2, 27.89) * mm});
            skLineSegment(sketch, "E1638", {"start": v(-267.2, 27.89) * mm, "end": v(-267.14, 28.09) * mm});
            skLineSegment(sketch, "E1639", {"start": v(-267.14, 28.09) * mm, "end": v(-267.1, 28.26) * mm});
            skLineSegment(sketch, "E1640", {"start": v(-267.1, 28.26) * mm, "end": v(-267.02, 28.43) * mm});
            skLineSegment(sketch, "E1641", {"start": v(-267.02, 28.43) * mm, "end": v(-266.94, 28.6) * mm});
            skLineSegment(sketch, "E1642", {"start": v(-266.94, 28.6) * mm, "end": v(-266.84, 28.76) * mm});
            skLineSegment(sketch, "E1643", {"start": v(-266.84, 28.76) * mm, "end": v(-266.74, 28.9) * mm});
            skLineSegment(sketch, "E1644", {"start": v(-266.74, 28.9) * mm, "end": v(-266.62, 29.05) * mm});
            skLineSegment(sketch, "E1645", {"start": v(-266.62, 29.05) * mm, "end": v(-266.47, 29.18) * mm});
            skLineSegment(sketch, "E1646", {"start": v(-266.47, 29.18) * mm, "end": v(-266.32, 29.3) * mm});
            skLineSegment(sketch, "E1647", {"start": v(-266.32, 29.3) * mm, "end": v(-266.17, 29.4) * mm});
            skLineSegment(sketch, "E1648", {"start": v(-266.17, 29.4) * mm, "end": v(-266.02, 29.48) * mm});
            skLineSegment(sketch, "E1649", {"start": v(-266.02, 29.48) * mm, "end": v(-265.85, 29.53) * mm});
            skLineSegment(sketch, "E1650", {"start": v(-265.85, 29.53) * mm, "end": v(-265.68, 29.58) * mm});
            skLineSegment(sketch, "E1651", {"start": v(-265.68, 29.58) * mm, "end": v(-265.48, 29.6) * mm});
            skLineSegment(sketch, "E1652", {"start": v(-265.48, 29.6) * mm, "end": v(-265.28, 29.6) * mm});
            skLineSegment(sketch, "E1653", {"start": v(-265.28, 29.6) * mm, "end": v(-265.1, 29.6) * mm});
            skLineSegment(sketch, "E1654", {"start": v(-265.1, 29.6) * mm, "end": v(-264.9, 29.58) * mm});
            skLineSegment(sketch, "E1655", {"start": v(-264.9, 29.58) * mm, "end": v(-264.73, 29.53) * mm});
            skLineSegment(sketch, "E1656", {"start": v(-264.73, 29.53) * mm, "end": v(-264.56, 29.48) * mm});
            skLineSegment(sketch, "E1657", {"start": v(-264.56, 29.48) * mm, "end": v(-264.39, 29.4) * mm});
            skLineSegment(sketch, "E1658", {"start": v(-264.39, 29.4) * mm, "end": v(-264.21, 29.3) * mm});
            skLineSegment(sketch, "E1659", {"start": v(-264.21, 29.3) * mm, "end": v(-264.06, 29.18) * mm});
            skLineSegment(sketch, "E1660", {"start": v(-264.06, 29.18) * mm, "end": v(-263.92, 29.05) * mm});
            skLineSegment(sketch, "E1661", {"start": v(-263.92, 29.05) * mm, "end": v(-263.8, 28.9) * mm});
            skLineSegment(sketch, "E1662", {"start": v(-263.8, 28.9) * mm, "end": v(-263.67, 28.76) * mm});
            skLineSegment(sketch, "E1663", {"start": v(-263.67, 28.76) * mm, "end": v(-263.57, 28.58) * mm});
            skLineSegment(sketch, "E1664", {"start": v(-263.57, 28.58) * mm, "end": v(-263.5, 28.4) * mm});
            skLineSegment(sketch, "E1665", {"start": v(-263.5, 28.4) * mm, "end": v(-263.44, 28.24) * mm});
            skLineSegment(sketch, "E1666", {"start": v(-263.44, 28.24) * mm, "end": v(-263.4, 28.06) * mm});
            skLineSegment(sketch, "E1667", {"start": v(-263.4, 28.06) * mm, "end": v(-263.37, 27.86) * mm});
            skLineSegment(sketch, "E1668", {"start": v(-263.37, 27.86) * mm, "end": v(-263.35, 27.67) * mm});
            skLineSegment(sketch, "E1669", {"start": v(-263.35, 27.67) * mm, "end": v(-263.37, 27.62) * mm});
            skLineSegment(sketch, "E1670", {"start": v(-263.37, 27.62) * mm, "end": v(-263.37, 27.54) * mm});
            skLineSegment(sketch, "E1671", {"start": v(-263.37, 27.54) * mm, "end": v(-263.37, 27.47) * mm});
            skLineSegment(sketch, "E1672", {"start": v(-263.37, 27.47) * mm, "end": v(-263.37, 27.4) * mm});
            skLineSegment(sketch, "E1673", {"start": v(-263.37, 27.4) * mm, "end": v(-263.37, 27.32) * mm});
            skLineSegment(sketch, "E1674", {"start": v(-263.37, 27.32) * mm, "end": v(-263.4, 27.24) * mm});
            skLineSegment(sketch, "E1675", {"start": v(-263.4, 27.24) * mm, "end": v(-263.4, 27.2) * mm});
            skLineSegment(sketch, "E1676", {"start": v(-263.4, 27.2) * mm, "end": v(-263.4, 27.12) * mm});
            skLineSegment(sketch, "E1677", {"start": v(-263.4, 27.12) * mm, "end": v(-266.82, 9.29) * mm});
            skLineSegment(sketch, "E1678", {"start": v(-266.82, 9.29) * mm, "end": v(-259.97, 9.29) * mm});
            skLineSegment(sketch, "E1679", {"start": v(-259.97, 9.29) * mm, "end": v(-259.97, 21.86) * mm});
            skLineSegment(sketch, "E1680", {"start": v(-259.97, 21.86) * mm, "end": v(-259.97, 22.04) * mm});
            skLineSegment(sketch, "E1681", {"start": v(-259.97, 22.04) * mm, "end": v(-259.95, 22.23) * mm});
            skLineSegment(sketch, "E1682", {"start": v(-259.95, 22.23) * mm, "end": v(-259.9, 22.4) * mm});
            skLineSegment(sketch, "E1683", {"start": v(-259.9, 22.4) * mm, "end": v(-259.82, 22.58) * mm});
            skLineSegment(sketch, "E1684", {"start": v(-259.82, 22.58) * mm, "end": v(-259.75, 22.75) * mm});
            skLineSegment(sketch, "E1685", {"start": v(-259.75, 22.75) * mm, "end": v(-259.65, 22.93) * mm});
            skLineSegment(sketch, "E1686", {"start": v(-259.65, 22.93) * mm, "end": v(-259.53, 23.08) * mm});
            skLineSegment(sketch, "E1687", {"start": v(-259.53, 23.08) * mm, "end": v(-259.4, 23.23) * mm});
            skLineSegment(sketch, "E1688", {"start": v(-259.4, 23.23) * mm, "end": v(-259.25, 23.35) * mm});
            skLineSegment(sketch, "E1689", {"start": v(-259.25, 23.35) * mm, "end": v(-259.1, 23.47) * mm});
            skLineSegment(sketch, "E1690", {"start": v(-259.1, 23.47) * mm, "end": v(-258.95, 23.57) * mm});
            skLineSegment(sketch, "E1691", {"start": v(-258.95, 23.57) * mm, "end": v(-258.78, 23.65) * mm});
            skLineSegment(sketch, "E1692", {"start": v(-258.78, 23.65) * mm, "end": v(-258.6, 23.7) * mm});
            skLineSegment(sketch, "E1693", {"start": v(-258.6, 23.7) * mm, "end": v(-258.43, 23.75) * mm});
            skLineSegment(sketch, "E1694", {"start": v(-258.43, 23.75) * mm, "end": v(-258.24, 23.77) * mm});
            skLineSegment(sketch, "E1695", {"start": v(-258.24, 23.77) * mm, "end": v(-258.04, 23.8) * mm});
            skLineSegment(sketch, "E1696", {"start": v(-258.04, 23.8) * mm, "end": v(-257.84, 23.77) * mm});
            skLineSegment(sketch, "E1697", {"start": v(-257.84, 23.77) * mm, "end": v(-257.64, 23.75) * mm});
            skLineSegment(sketch, "E1698", {"start": v(-257.64, 23.75) * mm, "end": v(-257.47, 23.7) * mm});
            skLineSegment(sketch, "E1699", {"start": v(-257.47, 23.7) * mm, "end": v(-257.3, 23.65) * mm});
            skLineSegment(sketch, "E1700", {"start": v(-257.3, 23.65) * mm, "end": v(-257.12, 23.57) * mm});
            skLineSegment(sketch, "E1701", {"start": v(-257.12, 23.57) * mm, "end": v(-256.97, 23.47) * mm});
            skLineSegment(sketch, "E1702", {"start": v(-256.97, 23.47) * mm, "end": v(-256.82, 23.35) * mm});
            skLineSegment(sketch, "E1703", {"start": v(-256.82, 23.35) * mm, "end": v(-256.67, 23.23) * mm});
            skLineSegment(sketch, "E1704", {"start": v(-256.67, 23.23) * mm, "end": v(-256.55, 23.08) * mm});
            skLineSegment(sketch, "E1705", {"start": v(-256.55, 23.08) * mm, "end": v(-256.42, 22.93) * mm});
            skLineSegment(sketch, "E1706", {"start": v(-256.42, 22.93) * mm, "end": v(-256.33, 22.75) * mm});
            skLineSegment(sketch, "E1707", {"start": v(-256.33, 22.75) * mm, "end": v(-256.25, 22.58) * mm});
            skLineSegment(sketch, "E1708", {"start": v(-256.25, 22.58) * mm, "end": v(-256.18, 22.4) * mm});
            skLineSegment(sketch, "E1709", {"start": v(-256.18, 22.4) * mm, "end": v(-256.13, 22.23) * mm});
            skLineSegment(sketch, "E1710", {"start": v(-256.13, 22.23) * mm, "end": v(-256.1, 22.04) * mm});
            skLineSegment(sketch, "E1711", {"start": v(-256.1, 22.04) * mm, "end": v(-256.1, 21.86) * mm});
            skLineSegment(sketch, "E1712", {"start": v(-256.1, 21.86) * mm, "end": v(-256.1, -1.36) * mm});
            skLineSegment(sketch, "E1713", {"start": v(-256.1, -1.36) * mm, "end": v(-256.1, -1.55) * mm});
            skLineSegment(sketch, "E1714", {"start": v(-256.1, -1.55) * mm, "end": v(-256.13, -1.75) * mm});
            skLineSegment(sketch, "E1715", {"start": v(-256.13, -1.75) * mm, "end": v(-256.18, -1.93) * mm});
            skLineSegment(sketch, "E1716", {"start": v(-256.18, -1.93) * mm, "end": v(-256.25, -2.1) * mm});
            skLineSegment(sketch, "E1717", {"start": v(-256.25, -2.1) * mm, "end": v(-256.33, -2.27) * mm});
            skLineSegment(sketch, "E1718", {"start": v(-256.33, -2.27) * mm, "end": v(-256.42, -2.45) * mm});
            skLineSegment(sketch, "E1719", {"start": v(-256.42, -2.45) * mm, "end": v(-256.55, -2.6) * mm});
            skLineSegment(sketch, "E1720", {"start": v(-256.55, -2.6) * mm, "end": v(-256.67, -2.74) * mm});
            skLineSegment(sketch, "E1721", {"start": v(-256.67, -2.74) * mm, "end": v(-256.82, -2.87) * mm});
            skLineSegment(sketch, "E1722", {"start": v(-256.82, -2.87) * mm, "end": v(-256.97, -3) * mm});
            skLineSegment(sketch, "E1723", {"start": v(-256.97, -3) * mm, "end": v(-257.12, -3.1) * mm});
            skLineSegment(sketch, "E1724", {"start": v(-257.12, -3.1) * mm, "end": v(-257.3, -3.17) * mm});
            skLineSegment(sketch, "E1725", {"start": v(-257.3, -3.17) * mm, "end": v(-257.47, -3.22) * mm});
            skLineSegment(sketch, "E1726", {"start": v(-257.47, -3.22) * mm, "end": v(-257.64, -3.27) * mm});
            skLineSegment(sketch, "E1727", {"start": v(-257.64, -3.27) * mm, "end": v(-257.84, -3.3) * mm});
            skLineSegment(sketch, "E1728", {"start": v(-257.84, -3.3) * mm, "end": v(-258.04, -3.3) * mm});
            skLineSegment(sketch, "E1729", {"start": v(-258.04, -3.3) * mm, "end": v(-258.24, -3.3) * mm});
            skLineSegment(sketch, "E1730", {"start": v(-258.24, -3.3) * mm, "end": v(-258.43, -3.27) * mm});
            skLineSegment(sketch, "E1731", {"start": v(-258.43, -3.27) * mm, "end": v(-258.6, -3.22) * mm});
            skLineSegment(sketch, "E1732", {"start": v(-258.6, -3.22) * mm, "end": v(-258.78, -3.17) * mm});
            skLineSegment(sketch, "E1733", {"start": v(-258.78, -3.17) * mm, "end": v(-258.95, -3.1) * mm});
            skLineSegment(sketch, "E1734", {"start": v(-258.95, -3.1) * mm, "end": v(-259.1, -3) * mm});
            skLineSegment(sketch, "E1735", {"start": v(-259.1, -3) * mm, "end": v(-259.25, -2.87) * mm});
            skLineSegment(sketch, "E1736", {"start": v(-259.25, -2.87) * mm, "end": v(-259.4, -2.74) * mm});
            skLineSegment(sketch, "E1737", {"start": v(-259.4, -2.74) * mm, "end": v(-259.53, -2.6) * mm});
            skLineSegment(sketch, "E1738", {"start": v(-259.53, -2.6) * mm, "end": v(-259.65, -2.45) * mm});
            skLineSegment(sketch, "E1739", {"start": v(-259.65, -2.45) * mm, "end": v(-259.75, -2.27) * mm});
            skLineSegment(sketch, "E1740", {"start": v(-259.75, -2.27) * mm, "end": v(-259.82, -2.1) * mm});
            skLineSegment(sketch, "E1741", {"start": v(-259.82, -2.1) * mm, "end": v(-259.9, -1.93) * mm});
            skLineSegment(sketch, "E1742", {"start": v(-259.9, -1.93) * mm, "end": v(-259.95, -1.75) * mm});
            skLineSegment(sketch, "E1743", {"start": v(-259.95, -1.75) * mm, "end": v(-259.97, -1.55) * mm});
            skLineSegment(sketch, "E1744", {"start": v(-259.97, -1.55) * mm, "end": v(-259.97, -1.36) * mm});
            skLineSegment(sketch, "E1745", {"start": v(-259.97, -1.36) * mm, "end": v(-259.97, 5.42) * mm});
            skLineSegment(sketch, "E1746", {"start": v(-259.97, 5.42) * mm, "end": v(-269.15, 5.42) * mm});
            skLineSegment(sketch, "E1747", {"start": v(-269.15, 5.42) * mm, "end": v(-269.35, 5.42) * mm});
            skLineSegment(sketch, "E1748", {"start": v(-269.35, 5.42) * mm, "end": v(-269.55, 5.44) * mm});
            skLineSegment(sketch, "E1749", {"start": v(-269.55, 5.44) * mm, "end": v(-269.72, 5.5) * mm});
            skLineSegment(sketch, "E1750", {"start": v(-269.72, 5.5) * mm, "end": v(-269.9, 5.54) * mm});
            skLineSegment(sketch, "E1751", {"start": v(-269.9, 5.54) * mm, "end": v(-270.07, 5.64) * mm});
            skLineSegment(sketch, "E1752", {"start": v(-270.07, 5.64) * mm, "end": v(-270.24, 5.74) * mm});
            skLineSegment(sketch, "E1753", {"start": v(-270.24, 5.74) * mm, "end": v(-270.39, 5.84) * mm});
            skLineSegment(sketch, "E1754", {"start": v(-270.39, 5.84) * mm, "end": v(-270.54, 5.99) * mm});
            skLineSegment(sketch, "E1755", {"start": v(-270.54, 5.99) * mm, "end": v(-270.66, 6.14) * mm});
            skLineSegment(sketch, "E1756", {"start": v(-270.66, 6.14) * mm, "end": v(-270.79, 6.28) * mm});
            skLineSegment(sketch, "E1757", {"start": v(-270.79, 6.28) * mm, "end": v(-270.89, 6.46) * mm});
            skLineSegment(sketch, "E1758", {"start": v(-270.89, 6.46) * mm, "end": v(-270.96, 6.6) * mm});
            skLineSegment(sketch, "E1759", {"start": v(-270.96, 6.6) * mm, "end": v(-271, 6.78) * mm});
            skLineSegment(sketch, "E1760", {"start": v(-271, 6.78) * mm, "end": v(-271.06, 6.95) * mm});
            skSolve(sketch);
        }
        {
            var Q0;
            Q0=makeQuery(id+"F0.imprint","IMPRINT",FACE,{"disambiguationData":[TD([[makeQuery(id+"F0.imprint","IMPRINT",EDGE,{"derivedFrom":sQuery(id+"F0.wireOp",EDGE,"E0.bottom")}),-1.0]])]});
            extrude(context, id + "F1", {"entities" : qUnion([Q0]), "depth" : 2.03 * mm, "offsetDistance" : 25.4 * mm});
        }
    });
